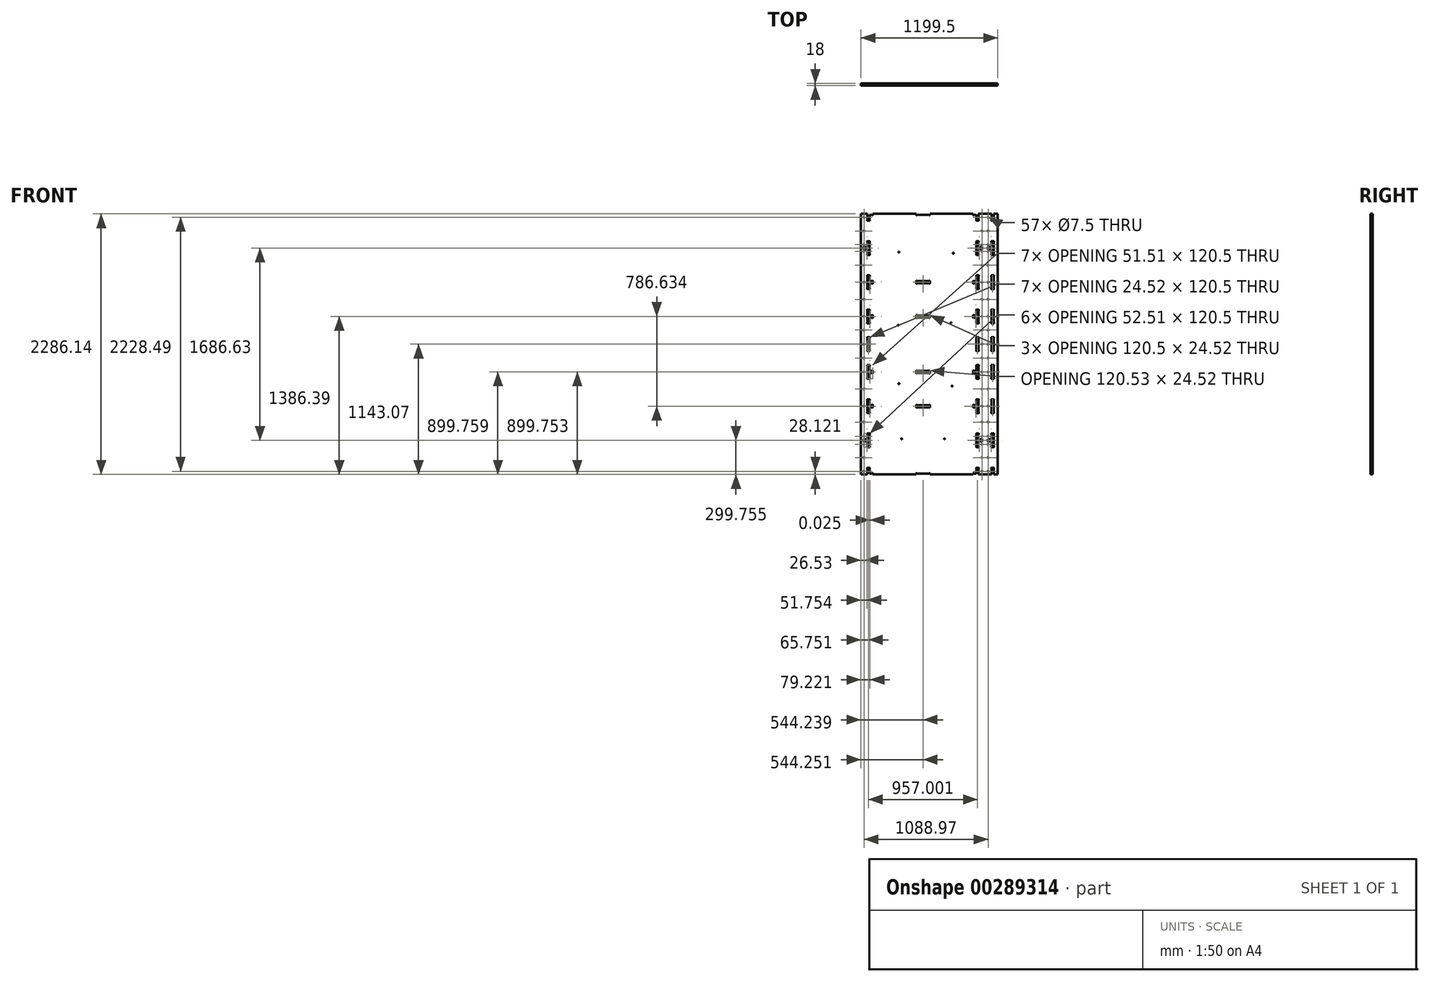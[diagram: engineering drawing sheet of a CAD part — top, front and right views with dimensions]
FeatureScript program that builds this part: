
annotation { "Feature Type Name" : "Feature", "Feature Type Description" : "" }
export const myFeature = defineFeature(function(context is Context, id is Id, definition is map)
    precondition{}
    {
        {
            var Q0;
            Q0=qCreatedBy(makeId("Front.planeOp"),FACE);
            var sketch = newSketch(context, id + "F0", { "sketchPlane" : qUnion([Q0])});
            skLineSegment(sketch, "E0", {"start": v(-600, -1200) * mm, "end": v(600, -1200) * mm});
            skLineSegment(sketch, "E1", {"start": v(600, -1200) * mm, "end": v(600, 1200) * mm});
            skLineSegment(sketch, "E2", {"start": v(600, 1200) * mm, "end": v(-600, 1200) * mm});
            skLineSegment(sketch, "E3", {"start": v(-600, 1200) * mm, "end": v(-600, -1200) * mm});
            skLineSegment(sketch, "E4", {"start": v(-600, -1086.14) * mm, "end": v(-543.5, -1086.14) * mm});
            skLineSegment(sketch, "E5", {"start": v(-543.5, -1086.14) * mm, "end": v(-543.5, -1032.4) * mm});
            skLineSegment(sketch, "E6", {"start": v(-543.5, -1032.4) * mm, "end": v(-543.5, -1032.17) * mm});
            skLineSegment(sketch, "E7", {"start": v(-543.5, -1032.17) * mm, "end": v(-543.73, -1032.16) * mm});
            skArc(sketch, "E8", {"start": v(-543.73, -1032.16) * mm, "mid": v(-546.5, -1029.04) * mm, "end": v(-543.5, -1026.14) * mm});
            skLineSegment(sketch, "E9", {"start": v(-543.5, -1026.14) * mm, "end": v(-525, -1026.14) * mm});
            skArc(sketch, "E10", {"start": v(-525, -1026.14) * mm, "mid": v(-521.98, -1029.03) * mm, "end": v(-524.77, -1032.16) * mm});
            skLineSegment(sketch, "E11", {"start": v(-524.77, -1032.16) * mm, "end": v(-525, -1032.17) * mm});
            skLineSegment(sketch, "E12", {"start": v(-525, -1032.17) * mm, "end": v(-525, -1032.4) * mm});
            skLineSegment(sketch, "E13", {"start": v(-525, -1032.4) * mm, "end": v(-525, -1077.14) * mm});
            skLineSegment(sketch, "E14", {"start": v(-525, -1077.14) * mm, "end": v(-501.27, -1077.14) * mm});
            skLineSegment(sketch, "E15", {"start": v(-501.27, -1077.14) * mm, "end": v(-501.04, -1077.14) * mm});
            skLineSegment(sketch, "E16", {"start": v(-501.04, -1077.14) * mm, "end": v(-501.02, -1076.9) * mm});
            skArc(sketch, "E17", {"start": v(-501.02, -1076.9) * mm, "mid": v(-497.9, -1074.13) * mm, "end": v(-495, -1077.14) * mm});
            skLineSegment(sketch, "E18", {"start": v(-495, -1077.14) * mm, "end": v(-495, -1086.14) * mm});
            skLineSegment(sketch, "E19", {"start": v(-495, -1086.14) * mm, "end": v(-116, -1086.14) * mm});
            skLineSegment(sketch, "E20", {"start": v(-116, -1086.14) * mm, "end": v(-116, -1077.14) * mm});
            skArc(sketch, "E21", {"start": v(-116, -1077.14) * mm, "mid": v(-113.1, -1074.12) * mm, "end": v(-109.98, -1076.9) * mm});
            skLineSegment(sketch, "E22", {"start": v(-109.98, -1076.9) * mm, "end": v(-109.96, -1077.14) * mm});
            skLineSegment(sketch, "E23", {"start": v(-109.96, -1077.14) * mm, "end": v(-109.73, -1077.14) * mm});
            skLineSegment(sketch, "E24", {"start": v(-109.73, -1077.14) * mm, "end": v(-1.77, -1077.14) * mm});
            skLineSegment(sketch, "E25", {"start": v(-1.77, -1077.14) * mm, "end": v(-1.54, -1077.14) * mm});
            skLineSegment(sketch, "E26", {"start": v(-1.54, -1077.14) * mm, "end": v(-1.52, -1076.9) * mm});
            skArc(sketch, "E27", {"start": v(-1.52, -1076.9) * mm, "mid": v(1.6, -1074.13) * mm, "end": v(4.5, -1077.14) * mm});
            skLineSegment(sketch, "E28", {"start": v(4.5, -1077.14) * mm, "end": v(4.5, -1086.14) * mm});
            skLineSegment(sketch, "E29", {"start": v(4.5, -1086.14) * mm, "end": v(383.5, -1086.14) * mm});
            skLineSegment(sketch, "E30", {"start": v(383.5, -1086.14) * mm, "end": v(383.5, -1077.14) * mm});
            skArc(sketch, "E31", {"start": v(383.5, -1077.14) * mm, "mid": v(386.4, -1074.12) * mm, "end": v(389.52, -1076.9) * mm});
            skLineSegment(sketch, "E32", {"start": v(389.52, -1076.9) * mm, "end": v(389.54, -1077.14) * mm});
            skLineSegment(sketch, "E33", {"start": v(389.54, -1077.14) * mm, "end": v(389.77, -1077.14) * mm});
            skLineSegment(sketch, "E34", {"start": v(389.77, -1077.14) * mm, "end": v(413.5, -1077.14) * mm});
            skLineSegment(sketch, "E35", {"start": v(413.5, -1077.14) * mm, "end": v(413.5, -1032.4) * mm});
            skLineSegment(sketch, "E36", {"start": v(413.5, -1032.4) * mm, "end": v(413.5, -1032.18) * mm});
            skLineSegment(sketch, "E37", {"start": v(413.5, -1032.18) * mm, "end": v(413.27, -1032.16) * mm});
            skArc(sketch, "E38", {"start": v(413.27, -1032.16) * mm, "mid": v(410.5, -1029.04) * mm, "end": v(413.5, -1026.14) * mm});
            skLineSegment(sketch, "E39", {"start": v(413.5, -1026.14) * mm, "end": v(432, -1026.14) * mm});
            skArc(sketch, "E40", {"start": v(432, -1026.14) * mm, "mid": v(435.02, -1029.04) * mm, "end": v(432.23, -1032.16) * mm});
            skLineSegment(sketch, "E41", {"start": v(432.23, -1032.16) * mm, "end": v(432, -1032.18) * mm});
            skLineSegment(sketch, "E42", {"start": v(432, -1032.18) * mm, "end": v(432, -1032.4) * mm});
            skLineSegment(sketch, "E43", {"start": v(432, -1032.4) * mm, "end": v(432, -1086.14) * mm});
            skLineSegment(sketch, "E44", {"start": v(432, -1086.14) * mm, "end": v(545.5, -1086.14) * mm});
            skLineSegment(sketch, "E45", {"start": v(545.5, -1086.14) * mm, "end": v(545.5, -1032.4) * mm});
            skLineSegment(sketch, "E46", {"start": v(545.5, -1032.4) * mm, "end": v(545.5, -1032.18) * mm});
            skLineSegment(sketch, "E47", {"start": v(545.5, -1032.18) * mm, "end": v(545.27, -1032.16) * mm});
            skArc(sketch, "E48", {"start": v(545.27, -1032.16) * mm, "mid": v(542.5, -1029.04) * mm, "end": v(545.5, -1026.14) * mm});
            skLineSegment(sketch, "E49", {"start": v(545.5, -1026.14) * mm, "end": v(564, -1026.14) * mm});
            skArc(sketch, "E50", {"start": v(564, -1026.14) * mm, "mid": v(567.02, -1029.04) * mm, "end": v(564.23, -1032.16) * mm});
            skLineSegment(sketch, "E51", {"start": v(564.23, -1032.16) * mm, "end": v(564, -1032.18) * mm});
            skLineSegment(sketch, "E52", {"start": v(564, -1032.18) * mm, "end": v(564, -1032.4) * mm});
            skLineSegment(sketch, "E53", {"start": v(564, -1032.4) * mm, "end": v(564, -1086.14) * mm});
            skLineSegment(sketch, "E54", {"start": v(564, -1086.14) * mm, "end": v(599.5, -1086.14) * mm});
            skLineSegment(sketch, "E55", {"start": v(599.5, -1086.14) * mm, "end": v(599.48, -336.39) * mm});
            skLineSegment(sketch, "E56", {"start": v(599.48, -336.39) * mm, "end": v(599.5, -336.28) * mm});
            skLineSegment(sketch, "E57", {"start": v(599.5, -336.28) * mm, "end": v(599.48, -64.75) * mm});
            skLineSegment(sketch, "E58", {"start": v(599.48, -64.75) * mm, "end": v(599.5, -64.64) * mm});
            skLineSegment(sketch, "E59", {"start": v(599.5, -64.64) * mm, "end": v(599.5, 1200) * mm});
            skLineSegment(sketch, "E60", {"start": v(599.5, 1200) * mm, "end": v(564, 1200) * mm});
            skLineSegment(sketch, "E61", {"start": v(564, 1200) * mm, "end": v(564, 1146.27) * mm});
            skLineSegment(sketch, "E62", {"start": v(564, 1146.27) * mm, "end": v(564, 1146.04) * mm});
            skLineSegment(sketch, "E63", {"start": v(564, 1146.04) * mm, "end": v(564.23, 1146.02) * mm});
            skArc(sketch, "E64", {"start": v(564.23, 1146.02) * mm, "mid": v(567, 1142.9) * mm, "end": v(564, 1140) * mm});
            skLineSegment(sketch, "E65", {"start": v(564, 1140) * mm, "end": v(545.5, 1140) * mm});
            skArc(sketch, "E66", {"start": v(545.5, 1140) * mm, "mid": v(542.48, 1142.9) * mm, "end": v(545.27, 1146.02) * mm});
            skLineSegment(sketch, "E67", {"start": v(545.27, 1146.02) * mm, "end": v(545.5, 1146.04) * mm});
            skLineSegment(sketch, "E68", {"start": v(545.5, 1146.04) * mm, "end": v(545.5, 1146.27) * mm});
            skLineSegment(sketch, "E69", {"start": v(545.5, 1146.27) * mm, "end": v(545.5, 1200) * mm});
            skLineSegment(sketch, "E70", {"start": v(545.5, 1200) * mm, "end": v(432, 1200) * mm});
            skLineSegment(sketch, "E71", {"start": v(432, 1200) * mm, "end": v(432, 1146.27) * mm});
            skLineSegment(sketch, "E72", {"start": v(432, 1146.27) * mm, "end": v(432, 1146.04) * mm});
            skLineSegment(sketch, "E73", {"start": v(432, 1146.04) * mm, "end": v(432.23, 1146.02) * mm});
            skArc(sketch, "E74", {"start": v(432.23, 1146.02) * mm, "mid": v(435, 1142.9) * mm, "end": v(432, 1140) * mm});
            skLineSegment(sketch, "E75", {"start": v(432, 1140) * mm, "end": v(413.5, 1140) * mm});
            skArc(sketch, "E76", {"start": v(413.5, 1140) * mm, "mid": v(410.48, 1142.9) * mm, "end": v(413.27, 1146.02) * mm});
            skLineSegment(sketch, "E77", {"start": v(413.27, 1146.02) * mm, "end": v(413.5, 1146.04) * mm});
            skLineSegment(sketch, "E78", {"start": v(413.5, 1146.04) * mm, "end": v(413.5, 1146.27) * mm});
            skLineSegment(sketch, "E79", {"start": v(413.5, 1146.27) * mm, "end": v(413.5, 1191) * mm});
            skLineSegment(sketch, "E80", {"start": v(413.5, 1191) * mm, "end": v(389.77, 1191) * mm});
            skLineSegment(sketch, "E81", {"start": v(389.77, 1191) * mm, "end": v(389.54, 1191) * mm});
            skLineSegment(sketch, "E82", {"start": v(389.54, 1191) * mm, "end": v(389.52, 1190.77) * mm});
            skArc(sketch, "E83", {"start": v(389.52, 1190.77) * mm, "mid": v(386.4, 1188) * mm, "end": v(383.5, 1191) * mm});
            skLineSegment(sketch, "E84", {"start": v(383.5, 1191) * mm, "end": v(383.5, 1200) * mm});
            skLineSegment(sketch, "E85", {"start": v(383.5, 1200) * mm, "end": v(4.5, 1200) * mm});
            skLineSegment(sketch, "E86", {"start": v(4.5, 1200) * mm, "end": v(4.5, 1191) * mm});
            skArc(sketch, "E87", {"start": v(4.5, 1191) * mm, "mid": v(1.6, 1187.98) * mm, "end": v(-1.52, 1190.77) * mm});
            skLineSegment(sketch, "E88", {"start": v(-1.52, 1190.77) * mm, "end": v(-1.54, 1191) * mm});
            skLineSegment(sketch, "E89", {"start": v(-1.54, 1191) * mm, "end": v(-1.77, 1191) * mm});
            skLineSegment(sketch, "E90", {"start": v(-1.77, 1191) * mm, "end": v(-109.73, 1191) * mm});
            skLineSegment(sketch, "E91", {"start": v(-109.73, 1191) * mm, "end": v(-109.96, 1191) * mm});
            skLineSegment(sketch, "E92", {"start": v(-109.96, 1191) * mm, "end": v(-109.98, 1190.77) * mm});
            skArc(sketch, "E93", {"start": v(-109.98, 1190.77) * mm, "mid": v(-113.1, 1188) * mm, "end": v(-116, 1191) * mm});
            skLineSegment(sketch, "E94", {"start": v(-116, 1191) * mm, "end": v(-116, 1200) * mm});
            skLineSegment(sketch, "E95", {"start": v(-116, 1200) * mm, "end": v(-495, 1200) * mm});
            skLineSegment(sketch, "E96", {"start": v(-495, 1200) * mm, "end": v(-495, 1191) * mm});
            skArc(sketch, "E97", {"start": v(-495, 1191) * mm, "mid": v(-497.9, 1187.98) * mm, "end": v(-501.02, 1190.77) * mm});
            skLineSegment(sketch, "E98", {"start": v(-501.02, 1190.77) * mm, "end": v(-501.04, 1191) * mm});
            skLineSegment(sketch, "E99", {"start": v(-501.04, 1191) * mm, "end": v(-501.27, 1191) * mm});
            skLineSegment(sketch, "E100", {"start": v(-501.27, 1191) * mm, "end": v(-525, 1191) * mm});
            skLineSegment(sketch, "E101", {"start": v(-525, 1191) * mm, "end": v(-525, 1146.27) * mm});
            skLineSegment(sketch, "E102", {"start": v(-525, 1146.27) * mm, "end": v(-525, 1146.04) * mm});
            skLineSegment(sketch, "E103", {"start": v(-525, 1146.04) * mm, "end": v(-524.77, 1146.02) * mm});
            skArc(sketch, "E104", {"start": v(-524.77, 1146.02) * mm, "mid": v(-522, 1142.9) * mm, "end": v(-525, 1140) * mm});
            skLineSegment(sketch, "E105", {"start": v(-525, 1140) * mm, "end": v(-543.5, 1140) * mm});
            skArc(sketch, "E106", {"start": v(-543.5, 1140) * mm, "mid": v(-546.52, 1142.9) * mm, "end": v(-543.73, 1146.02) * mm});
            skLineSegment(sketch, "E107", {"start": v(-543.73, 1146.02) * mm, "end": v(-543.5, 1146.04) * mm});
            skLineSegment(sketch, "E108", {"start": v(-543.5, 1146.04) * mm, "end": v(-543.5, 1146.27) * mm});
            skLineSegment(sketch, "E109", {"start": v(-543.5, 1146.27) * mm, "end": v(-543.5, 1200) * mm});
            skLineSegment(sketch, "E110", {"start": v(545.5, 2.7) * mm, "end": v(545.5, 111.16) * mm});
            skArc(sketch, "E111", {"start": v(545.5, 111.16) * mm, "mid": v(542.5, 114.17) * mm, "end": v(545.5, 117.18) * mm});
            skLineSegment(sketch, "E112", {"start": v(545.5, 117.18) * mm, "end": v(564, 117.18) * mm});
            skArc(sketch, "E113", {"start": v(564, 117.18) * mm, "mid": v(567.01, 114.17) * mm, "end": v(564, 111.16) * mm});
            skLineSegment(sketch, "E114", {"start": v(564, 111.16) * mm, "end": v(564, 2.7) * mm});
            skArc(sketch, "E115", {"start": v(564, 2.7) * mm, "mid": v(567.01, -0.3) * mm, "end": v(564, -3.32) * mm});
            skLineSegment(sketch, "E116", {"start": v(564, -3.32) * mm, "end": v(545.5, -3.32) * mm});
            skArc(sketch, "E117", {"start": v(545.5, -3.32) * mm, "mid": v(542.5, -0.3) * mm, "end": v(545.5, 2.7) * mm});
            skLineSegment(sketch, "E118", {"start": v(563.98, -132.16) * mm, "end": v(564, -240.62) * mm});
            skArc(sketch, "E119", {"start": v(564, -240.62) * mm, "mid": v(567.01, -243.63) * mm, "end": v(564, -246.64) * mm});
            skLineSegment(sketch, "E120", {"start": v(564, -246.64) * mm, "end": v(545.5, -246.63) * mm});
            skArc(sketch, "E121", {"start": v(545.5, -246.63) * mm, "mid": v(542.5, -243.62) * mm, "end": v(545.5, -240.61) * mm});
            skLineSegment(sketch, "E122", {"start": v(545.5, -240.61) * mm, "end": v(545.5, -132.16) * mm});
            skArc(sketch, "E123", {"start": v(545.5, -132.16) * mm, "mid": v(542.5, -129.15) * mm, "end": v(545.5, -126.14) * mm});
            skLineSegment(sketch, "E124", {"start": v(545.5, -126.14) * mm, "end": v(563.98, -126.14) * mm});
            skArc(sketch, "E125", {"start": v(563.98, -126.14) * mm, "mid": v(566.99, -129.15) * mm, "end": v(563.98, -132.16) * mm});
            skLineSegment(sketch, "E126", {"start": v(564, -432.15) * mm, "end": v(564, -540.61) * mm});
            skArc(sketch, "E127", {"start": v(564, -540.61) * mm, "mid": v(567.01, -543.62) * mm, "end": v(564, -546.63) * mm});
            skLineSegment(sketch, "E128", {"start": v(564, -546.63) * mm, "end": v(545.5, -546.63) * mm});
            skArc(sketch, "E129", {"start": v(545.5, -546.63) * mm, "mid": v(542.5, -543.62) * mm, "end": v(545.5, -540.61) * mm});
            skLineSegment(sketch, "E130", {"start": v(545.5, -540.61) * mm, "end": v(545.5, -432.15) * mm});
            skArc(sketch, "E131", {"start": v(545.5, -432.15) * mm, "mid": v(542.5, -429.14) * mm, "end": v(545.5, -426.13) * mm});
            skLineSegment(sketch, "E132", {"start": v(545.5, -426.13) * mm, "end": v(564, -426.13) * mm});
            skArc(sketch, "E133", {"start": v(564, -426.13) * mm, "mid": v(567.01, -429.14) * mm, "end": v(564, -432.15) * mm});
            skLineSegment(sketch, "E134", {"start": v(514.5, -795.63) * mm, "end": v(514.5, -777.13) * mm});
            skArc(sketch, "E135", {"start": v(514.5, -777.13) * mm, "mid": v(517.5, -774.12) * mm, "end": v(520.52, -777.13) * mm});
            skLineSegment(sketch, "E136", {"start": v(520.52, -777.13) * mm, "end": v(545.5, -777.13) * mm});
            skLineSegment(sketch, "E137", {"start": v(545.5, -777.13) * mm, "end": v(545.5, -732.15) * mm});
            skArc(sketch, "E138", {"start": v(545.5, -732.15) * mm, "mid": v(542.49, -729.14) * mm, "end": v(545.5, -726.13) * mm});
            skLineSegment(sketch, "E139", {"start": v(545.5, -726.13) * mm, "end": v(564, -726.13) * mm});
            skArc(sketch, "E140", {"start": v(564, -726.13) * mm, "mid": v(567, -729.14) * mm, "end": v(564, -732.15) * mm});
            skLineSegment(sketch, "E141", {"start": v(564, -732.15) * mm, "end": v(564, -840.61) * mm});
            skArc(sketch, "E142", {"start": v(564, -840.61) * mm, "mid": v(567, -843.62) * mm, "end": v(564, -846.63) * mm});
            skLineSegment(sketch, "E143", {"start": v(564, -846.63) * mm, "end": v(545.5, -846.63) * mm});
            skArc(sketch, "E144", {"start": v(545.5, -846.63) * mm, "mid": v(542.49, -843.62) * mm, "end": v(545.5, -840.61) * mm});
            skLineSegment(sketch, "E145", {"start": v(545.5, -840.61) * mm, "end": v(545.5, -795.63) * mm});
            skLineSegment(sketch, "E146", {"start": v(545.5, -795.63) * mm, "end": v(520.52, -795.63) * mm});
            skArc(sketch, "E147", {"start": v(520.52, -795.63) * mm, "mid": v(517.5, -798.64) * mm, "end": v(514.5, -795.63) * mm});
            skLineSegment(sketch, "E148", {"start": v(432, -795.63) * mm, "end": v(432, -840.61) * mm});
            skArc(sketch, "E149", {"start": v(432, -840.61) * mm, "mid": v(435.01, -843.62) * mm, "end": v(432, -846.63) * mm});
            skLineSegment(sketch, "E150", {"start": v(432, -846.63) * mm, "end": v(413.5, -846.63) * mm});
            skArc(sketch, "E151", {"start": v(413.5, -846.63) * mm, "mid": v(410.5, -843.62) * mm, "end": v(413.5, -840.61) * mm});
            skLineSegment(sketch, "E152", {"start": v(413.5, -840.61) * mm, "end": v(413.5, -732.15) * mm});
            skArc(sketch, "E153", {"start": v(413.5, -732.15) * mm, "mid": v(410.5, -729.14) * mm, "end": v(413.5, -726.13) * mm});
            skLineSegment(sketch, "E154", {"start": v(413.5, -726.13) * mm, "end": v(432, -726.13) * mm});
            skArc(sketch, "E155", {"start": v(432, -726.13) * mm, "mid": v(435.01, -729.14) * mm, "end": v(432, -732.15) * mm});
            skLineSegment(sketch, "E156", {"start": v(432, -732.15) * mm, "end": v(432, -777.13) * mm});
            skLineSegment(sketch, "E157", {"start": v(432, -777.13) * mm, "end": v(456.98, -777.13) * mm});
            skArc(sketch, "E158", {"start": v(456.98, -777.13) * mm, "mid": v(459.99, -774.12) * mm, "end": v(463, -777.13) * mm});
            skLineSegment(sketch, "E159", {"start": v(463, -777.13) * mm, "end": v(463, -795.63) * mm});
            skArc(sketch, "E160", {"start": v(463, -795.63) * mm, "mid": v(459.99, -798.64) * mm, "end": v(456.98, -795.63) * mm});
            skLineSegment(sketch, "E161", {"start": v(456.98, -795.63) * mm, "end": v(432, -795.63) * mm});
            skLineSegment(sketch, "E162", {"start": v(432, 840) * mm, "end": v(413.5, 840) * mm});
            skArc(sketch, "E163", {"start": v(413.5, 840) * mm, "mid": v(410.5, 843) * mm, "end": v(413.5, 846.02) * mm});
            skLineSegment(sketch, "E164", {"start": v(413.5, 846.02) * mm, "end": v(413.5, 954.48) * mm});
            skArc(sketch, "E165", {"start": v(413.5, 954.48) * mm, "mid": v(410.5, 957.49) * mm, "end": v(413.5, 960.5) * mm});
            skLineSegment(sketch, "E166", {"start": v(413.5, 960.5) * mm, "end": v(432, 960.5) * mm});
            skArc(sketch, "E167", {"start": v(432, 960.5) * mm, "mid": v(435.01, 957.49) * mm, "end": v(432, 954.48) * mm});
            skLineSegment(sketch, "E168", {"start": v(432, 954.48) * mm, "end": v(432, 909.5) * mm});
            skLineSegment(sketch, "E169", {"start": v(432, 909.5) * mm, "end": v(456.98, 909.5) * mm});
            skArc(sketch, "E170", {"start": v(456.98, 909.5) * mm, "mid": v(459.99, 912.5) * mm, "end": v(463, 909.5) * mm});
            skLineSegment(sketch, "E171", {"start": v(463, 909.5) * mm, "end": v(463, 891) * mm});
            skArc(sketch, "E172", {"start": v(463, 891) * mm, "mid": v(459.99, 887.99) * mm, "end": v(456.98, 891) * mm});
            skLineSegment(sketch, "E173", {"start": v(456.98, 891) * mm, "end": v(432, 891) * mm});
            skLineSegment(sketch, "E174", {"start": v(432, 891) * mm, "end": v(432, 846.02) * mm});
            skArc(sketch, "E175", {"start": v(432, 846.02) * mm, "mid": v(435.01, 843) * mm, "end": v(432, 840) * mm});
            skLineSegment(sketch, "E176", {"start": v(564, 654.48) * mm, "end": v(564, 546.02) * mm});
            skArc(sketch, "E177", {"start": v(564, 546.02) * mm, "mid": v(567.01, 543) * mm, "end": v(564, 540) * mm});
            skLineSegment(sketch, "E178", {"start": v(564, 540) * mm, "end": v(545.5, 540) * mm});
            skArc(sketch, "E179", {"start": v(545.5, 540) * mm, "mid": v(542.5, 543) * mm, "end": v(545.5, 546.02) * mm});
            skLineSegment(sketch, "E180", {"start": v(545.5, 546.02) * mm, "end": v(545.5, 654.48) * mm});
            skArc(sketch, "E181", {"start": v(545.5, 654.48) * mm, "mid": v(542.5, 657.49) * mm, "end": v(545.5, 660.5) * mm});
            skLineSegment(sketch, "E182", {"start": v(545.5, 660.5) * mm, "end": v(564, 660.5) * mm});
            skArc(sketch, "E183", {"start": v(564, 660.5) * mm, "mid": v(567.01, 657.49) * mm, "end": v(564, 654.48) * mm});
            skLineSegment(sketch, "E184", {"start": v(564, 354.48) * mm, "end": v(564, 246.02) * mm});
            skArc(sketch, "E185", {"start": v(564, 246.02) * mm, "mid": v(567.01, 243) * mm, "end": v(564, 240) * mm});
            skLineSegment(sketch, "E186", {"start": v(564, 240) * mm, "end": v(545.5, 240) * mm});
            skArc(sketch, "E187", {"start": v(545.5, 240) * mm, "mid": v(542.5, 243) * mm, "end": v(545.5, 246.02) * mm});
            skLineSegment(sketch, "E188", {"start": v(545.5, 246.02) * mm, "end": v(545.5, 354.48) * mm});
            skArc(sketch, "E189", {"start": v(545.5, 354.48) * mm, "mid": v(542.5, 357.49) * mm, "end": v(545.5, 360.5) * mm});
            skLineSegment(sketch, "E190", {"start": v(545.5, 360.5) * mm, "end": v(564, 360.5) * mm});
            skArc(sketch, "E191", {"start": v(564, 360.5) * mm, "mid": v(567.01, 357.49) * mm, "end": v(564, 354.48) * mm});
            skLineSegment(sketch, "E192", {"start": v(413.5, 309.5) * mm, "end": v(413.5, 354.48) * mm});
            skArc(sketch, "E193", {"start": v(413.5, 354.48) * mm, "mid": v(410.5, 357.49) * mm, "end": v(413.5, 360.5) * mm});
            skLineSegment(sketch, "E194", {"start": v(413.5, 360.5) * mm, "end": v(432, 360.5) * mm});
            skArc(sketch, "E195", {"start": v(432, 360.5) * mm, "mid": v(435.01, 357.49) * mm, "end": v(432, 354.48) * mm});
            skLineSegment(sketch, "E196", {"start": v(432, 354.48) * mm, "end": v(432, 246.02) * mm});
            skArc(sketch, "E197", {"start": v(432, 246.02) * mm, "mid": v(435.01, 243) * mm, "end": v(432, 240) * mm});
            skLineSegment(sketch, "E198", {"start": v(432, 240) * mm, "end": v(413.5, 240) * mm});
            skArc(sketch, "E199", {"start": v(413.5, 240) * mm, "mid": v(410.5, 243) * mm, "end": v(413.5, 246.02) * mm});
            skLineSegment(sketch, "E200", {"start": v(413.5, 246.02) * mm, "end": v(413.5, 291) * mm});
            skLineSegment(sketch, "E201", {"start": v(413.5, 291) * mm, "end": v(389.52, 291) * mm});
            skArc(sketch, "E202", {"start": v(389.52, 291) * mm, "mid": v(386.51, 287.99) * mm, "end": v(383.5, 291) * mm});
            skLineSegment(sketch, "E203", {"start": v(383.5, 291) * mm, "end": v(383.5, 309.5) * mm});
            skArc(sketch, "E204", {"start": v(383.5, 309.5) * mm, "mid": v(386.51, 312.5) * mm, "end": v(389.52, 309.5) * mm});
            skLineSegment(sketch, "E205", {"start": v(389.52, 309.5) * mm, "end": v(413.5, 309.5) * mm});
            skLineSegment(sketch, "E206", {"start": v(432, 111.16) * mm, "end": v(432, 2.7) * mm});
            skArc(sketch, "E207", {"start": v(432, 2.7) * mm, "mid": v(435.01, -0.31) * mm, "end": v(432, -3.32) * mm});
            skLineSegment(sketch, "E208", {"start": v(432, -3.32) * mm, "end": v(413.5, -3.32) * mm});
            skArc(sketch, "E209", {"start": v(413.5, -3.32) * mm, "mid": v(410.5, -0.31) * mm, "end": v(413.5, 2.7) * mm});
            skLineSegment(sketch, "E210", {"start": v(413.5, 2.7) * mm, "end": v(413.5, 111.16) * mm});
            skArc(sketch, "E211", {"start": v(413.5, 111.16) * mm, "mid": v(410.5, 114.17) * mm, "end": v(413.5, 117.18) * mm});
            skLineSegment(sketch, "E212", {"start": v(413.5, 117.18) * mm, "end": v(432, 117.18) * mm});
            skArc(sketch, "E213", {"start": v(432, 117.18) * mm, "mid": v(435.01, 114.17) * mm, "end": v(432, 111.16) * mm});
            skLineSegment(sketch, "E214", {"start": v(413.48, -195.64) * mm, "end": v(389.52, -195.64) * mm});
            skArc(sketch, "E215", {"start": v(389.52, -195.64) * mm, "mid": v(386.51, -198.65) * mm, "end": v(383.5, -195.63) * mm});
            skLineSegment(sketch, "E216", {"start": v(383.5, -195.63) * mm, "end": v(383.5, -177.14) * mm});
            skArc(sketch, "E217", {"start": v(383.5, -177.14) * mm, "mid": v(386.51, -174.13) * mm, "end": v(389.52, -177.14) * mm});
            skLineSegment(sketch, "E218", {"start": v(389.52, -177.14) * mm, "end": v(413.5, -177.14) * mm});
            skLineSegment(sketch, "E219", {"start": v(413.5, -177.14) * mm, "end": v(413.48, -132.15) * mm});
            skArc(sketch, "E220", {"start": v(413.48, -132.15) * mm, "mid": v(410.47, -129.15) * mm, "end": v(413.48, -126.13) * mm});
            skLineSegment(sketch, "E221", {"start": v(413.48, -126.13) * mm, "end": v(431.98, -126.14) * mm});
            skArc(sketch, "E222", {"start": v(431.98, -126.14) * mm, "mid": v(434.99, -129.15) * mm, "end": v(431.98, -132.16) * mm});
            skLineSegment(sketch, "E223", {"start": v(431.98, -132.16) * mm, "end": v(432, -240.62) * mm});
            skArc(sketch, "E224", {"start": v(432, -240.62) * mm, "mid": v(435.01, -243.63) * mm, "end": v(432, -246.64) * mm});
            skLineSegment(sketch, "E225", {"start": v(432, -246.64) * mm, "end": v(413.5, -246.63) * mm});
            skArc(sketch, "E226", {"start": v(413.5, -246.63) * mm, "mid": v(410.49, -243.63) * mm, "end": v(413.5, -240.61) * mm});
            skLineSegment(sketch, "E227", {"start": v(413.5, -240.61) * mm, "end": v(413.48, -195.64) * mm});
            skLineSegment(sketch, "E228", {"start": v(383.5, -495.64) * mm, "end": v(383.5, -477.14) * mm});
            skArc(sketch, "E229", {"start": v(383.5, -477.14) * mm, "mid": v(386.51, -474.13) * mm, "end": v(389.52, -477.14) * mm});
            skLineSegment(sketch, "E230", {"start": v(389.52, -477.14) * mm, "end": v(413.5, -477.14) * mm});
            skLineSegment(sketch, "E231", {"start": v(413.5, -477.14) * mm, "end": v(413.5, -432.15) * mm});
            skArc(sketch, "E232", {"start": v(413.5, -432.15) * mm, "mid": v(410.5, -429.14) * mm, "end": v(413.5, -426.13) * mm});
            skLineSegment(sketch, "E233", {"start": v(413.5, -426.13) * mm, "end": v(432, -426.13) * mm});
            skArc(sketch, "E234", {"start": v(432, -426.13) * mm, "mid": v(435.01, -429.14) * mm, "end": v(432, -432.15) * mm});
            skLineSegment(sketch, "E235", {"start": v(432, -432.15) * mm, "end": v(432, -540.61) * mm});
            skArc(sketch, "E236", {"start": v(432, -540.61) * mm, "mid": v(435.01, -543.62) * mm, "end": v(432, -546.63) * mm});
            skLineSegment(sketch, "E237", {"start": v(432, -546.63) * mm, "end": v(413.5, -546.63) * mm});
            skArc(sketch, "E238", {"start": v(413.5, -546.63) * mm, "mid": v(410.5, -543.62) * mm, "end": v(413.5, -540.61) * mm});
            skLineSegment(sketch, "E239", {"start": v(413.5, -540.61) * mm, "end": v(413.5, -495.64) * mm});
            skLineSegment(sketch, "E240", {"start": v(413.5, -495.64) * mm, "end": v(389.52, -495.64) * mm});
            skArc(sketch, "E241", {"start": v(389.52, -495.64) * mm, "mid": v(386.51, -498.65) * mm, "end": v(383.5, -495.64) * mm});
            skLineSegment(sketch, "E242", {"start": v(-1.52, -495.64) * mm, "end": v(-109.98, -495.64) * mm});
            skArc(sketch, "E243", {"start": v(-109.98, -495.64) * mm, "mid": v(-112.99, -498.65) * mm, "end": v(-116, -495.64) * mm});
            skLineSegment(sketch, "E244", {"start": v(-116, -495.64) * mm, "end": v(-116, -477.14) * mm});
            skArc(sketch, "E245", {"start": v(-116, -477.14) * mm, "mid": v(-112.99, -474.13) * mm, "end": v(-109.98, -477.14) * mm});
            skLineSegment(sketch, "E246", {"start": v(-109.98, -477.14) * mm, "end": v(-1.52, -477.14) * mm});
            skArc(sketch, "E247", {"start": v(-1.52, -477.14) * mm, "mid": v(1.5, -474.13) * mm, "end": v(4.5, -477.14) * mm});
            skLineSegment(sketch, "E248", {"start": v(4.5, -477.14) * mm, "end": v(4.5, -495.64) * mm});
            skArc(sketch, "E249", {"start": v(4.5, -495.64) * mm, "mid": v(1.5, -498.65) * mm, "end": v(-1.52, -495.64) * mm});
            skLineSegment(sketch, "E250", {"start": v(-543.5, -777.13) * mm, "end": v(-543.5, -732.16) * mm});
            skArc(sketch, "E251", {"start": v(-543.5, -732.16) * mm, "mid": v(-546.5, -729.15) * mm, "end": v(-543.5, -726.14) * mm});
            skLineSegment(sketch, "E252", {"start": v(-543.5, -726.14) * mm, "end": v(-525, -726.14) * mm});
            skArc(sketch, "E253", {"start": v(-525, -726.14) * mm, "mid": v(-521.99, -729.15) * mm, "end": v(-525, -732.16) * mm});
            skLineSegment(sketch, "E254", {"start": v(-525, -732.16) * mm, "end": v(-525, -840.62) * mm});
            skArc(sketch, "E255", {"start": v(-525, -840.62) * mm, "mid": v(-521.99, -843.63) * mm, "end": v(-525, -846.64) * mm});
            skLineSegment(sketch, "E256", {"start": v(-525, -846.64) * mm, "end": v(-543.5, -846.64) * mm});
            skArc(sketch, "E257", {"start": v(-543.5, -846.64) * mm, "mid": v(-546.5, -843.63) * mm, "end": v(-543.5, -840.62) * mm});
            skLineSegment(sketch, "E258", {"start": v(-543.5, -840.62) * mm, "end": v(-543.5, -795.63) * mm});
            skLineSegment(sketch, "E259", {"start": v(-543.5, -795.63) * mm, "end": v(-568.48, -795.63) * mm});
            skArc(sketch, "E260", {"start": v(-568.48, -795.63) * mm, "mid": v(-571.5, -798.64) * mm, "end": v(-574.5, -795.63) * mm});
            skLineSegment(sketch, "E261", {"start": v(-574.5, -795.63) * mm, "end": v(-574.5, -777.13) * mm});
            skArc(sketch, "E262", {"start": v(-574.5, -777.13) * mm, "mid": v(-571.5, -774.12) * mm, "end": v(-568.48, -777.13) * mm});
            skLineSegment(sketch, "E263", {"start": v(-568.48, -777.13) * mm, "end": v(-543.5, -777.13) * mm});
            skLineSegment(sketch, "E264", {"start": v(-543.5, 891) * mm, "end": v(-568.48, 891) * mm});
            skArc(sketch, "E265", {"start": v(-568.48, 891) * mm, "mid": v(-571.5, 887.99) * mm, "end": v(-574.5, 891) * mm});
            skLineSegment(sketch, "E266", {"start": v(-574.5, 891) * mm, "end": v(-574.5, 909.5) * mm});
            skArc(sketch, "E267", {"start": v(-574.5, 909.5) * mm, "mid": v(-571.5, 912.5) * mm, "end": v(-568.48, 909.5) * mm});
            skLineSegment(sketch, "E268", {"start": v(-568.48, 909.5) * mm, "end": v(-543.5, 909.5) * mm});
            skLineSegment(sketch, "E269", {"start": v(-543.5, 909.5) * mm, "end": v(-543.5, 954.48) * mm});
            skArc(sketch, "E270", {"start": v(-543.5, 954.48) * mm, "mid": v(-546.5, 957.5) * mm, "end": v(-543.5, 960.5) * mm});
            skLineSegment(sketch, "E271", {"start": v(-543.5, 960.5) * mm, "end": v(-525, 960.5) * mm});
            skArc(sketch, "E272", {"start": v(-525, 960.5) * mm, "mid": v(-521.99, 957.49) * mm, "end": v(-525, 954.48) * mm});
            skLineSegment(sketch, "E273", {"start": v(-525, 954.48) * mm, "end": v(-525, 846.02) * mm});
            skArc(sketch, "E274", {"start": v(-525, 846.02) * mm, "mid": v(-521.99, 843) * mm, "end": v(-525, 840) * mm});
            skLineSegment(sketch, "E275", {"start": v(-525, 840) * mm, "end": v(-543.5, 840) * mm});
            skArc(sketch, "E276", {"start": v(-543.5, 840) * mm, "mid": v(-546.5, 843) * mm, "end": v(-543.5, 846.02) * mm});
            skLineSegment(sketch, "E277", {"start": v(-543.5, 846.02) * mm, "end": v(-543.5, 891) * mm});
            skLineSegment(sketch, "E278", {"start": v(-1.52, 591) * mm, "end": v(-109.98, 591) * mm});
            skArc(sketch, "E279", {"start": v(-109.98, 591) * mm, "mid": v(-112.99, 587.99) * mm, "end": v(-116, 591) * mm});
            skLineSegment(sketch, "E280", {"start": v(-116, 591) * mm, "end": v(-116, 609.5) * mm});
            skArc(sketch, "E281", {"start": v(-116, 609.5) * mm, "mid": v(-112.99, 612.5) * mm, "end": v(-109.98, 609.5) * mm});
            skLineSegment(sketch, "E282", {"start": v(-109.98, 609.5) * mm, "end": v(-1.52, 609.5) * mm});
            skArc(sketch, "E283", {"start": v(-1.52, 609.5) * mm, "mid": v(1.5, 612.5) * mm, "end": v(4.5, 609.5) * mm});
            skLineSegment(sketch, "E284", {"start": v(4.5, 609.5) * mm, "end": v(4.5, 591) * mm});
            skArc(sketch, "E285", {"start": v(4.5, 591) * mm, "mid": v(1.5, 587.99) * mm, "end": v(-1.52, 591) * mm});
            skLineSegment(sketch, "E286", {"start": v(-109.98, 309.5) * mm, "end": v(-1.52, 309.5) * mm});
            skArc(sketch, "E287", {"start": v(-1.52, 309.5) * mm, "mid": v(1.5, 312.5) * mm, "end": v(4.5, 309.5) * mm});
            skLineSegment(sketch, "E288", {"start": v(4.5, 309.5) * mm, "end": v(4.5, 291) * mm});
            skArc(sketch, "E289", {"start": v(4.5, 291) * mm, "mid": v(1.5, 287.99) * mm, "end": v(-1.52, 291) * mm});
            skLineSegment(sketch, "E290", {"start": v(-1.52, 291) * mm, "end": v(-109.98, 291) * mm});
            skArc(sketch, "E291", {"start": v(-109.98, 291) * mm, "mid": v(-112.99, 287.99) * mm, "end": v(-116, 291) * mm});
            skLineSegment(sketch, "E292", {"start": v(-116, 291) * mm, "end": v(-116, 309.5) * mm});
            skArc(sketch, "E293", {"start": v(-116, 309.5) * mm, "mid": v(-112.99, 312.5) * mm, "end": v(-109.98, 309.5) * mm});
            skLineSegment(sketch, "E294", {"start": v(-116, -195.63) * mm, "end": v(-116.02, -177.13) * mm});
            skArc(sketch, "E295", {"start": v(-116.02, -177.13) * mm, "mid": v(-113.01, -174.12) * mm, "end": v(-110, -177.13) * mm});
            skLineSegment(sketch, "E296", {"start": v(-110, -177.13) * mm, "end": v(-1.54, -177.14) * mm});
            skArc(sketch, "E297", {"start": v(-1.54, -177.14) * mm, "mid": v(1.47, -174.13) * mm, "end": v(4.48, -177.14) * mm});
            skLineSegment(sketch, "E298", {"start": v(4.48, -177.14) * mm, "end": v(4.5, -195.64) * mm});
            skArc(sketch, "E299", {"start": v(4.5, -195.64) * mm, "mid": v(1.5, -198.65) * mm, "end": v(-1.52, -195.64) * mm});
            skLineSegment(sketch, "E300", {"start": v(-1.52, -195.64) * mm, "end": v(-109.98, -195.63) * mm});
            skArc(sketch, "E301", {"start": v(-109.98, -195.63) * mm, "mid": v(-112.99, -198.64) * mm, "end": v(-116, -195.63) * mm});
            skLineSegment(sketch, "E302", {"start": v(-543.5, -540.61) * mm, "end": v(-543.5, -432.15) * mm});
            skArc(sketch, "E303", {"start": v(-543.5, -432.15) * mm, "mid": v(-546.5, -429.14) * mm, "end": v(-543.5, -426.13) * mm});
            skLineSegment(sketch, "E304", {"start": v(-543.5, -426.13) * mm, "end": v(-525, -426.13) * mm});
            skArc(sketch, "E305", {"start": v(-525, -426.13) * mm, "mid": v(-521.99, -429.14) * mm, "end": v(-525, -432.15) * mm});
            skLineSegment(sketch, "E306", {"start": v(-525, -432.15) * mm, "end": v(-525, -477.14) * mm});
            skLineSegment(sketch, "E307", {"start": v(-525, -477.14) * mm, "end": v(-501.02, -477.14) * mm});
            skArc(sketch, "E308", {"start": v(-501.02, -477.14) * mm, "mid": v(-498, -474.13) * mm, "end": v(-495, -477.14) * mm});
            skLineSegment(sketch, "E309", {"start": v(-495, -477.14) * mm, "end": v(-495, -495.63) * mm});
            skArc(sketch, "E310", {"start": v(-495, -495.63) * mm, "mid": v(-498, -498.64) * mm, "end": v(-501.02, -495.63) * mm});
            skLineSegment(sketch, "E311", {"start": v(-501.02, -495.63) * mm, "end": v(-525, -495.63) * mm});
            skLineSegment(sketch, "E312", {"start": v(-525, -495.63) * mm, "end": v(-525, -540.61) * mm});
            skArc(sketch, "E313", {"start": v(-525, -540.61) * mm, "mid": v(-521.99, -543.62) * mm, "end": v(-525, -546.63) * mm});
            skLineSegment(sketch, "E314", {"start": v(-525, -546.63) * mm, "end": v(-543.5, -546.63) * mm});
            skArc(sketch, "E315", {"start": v(-543.5, -546.63) * mm, "mid": v(-546.5, -543.62) * mm, "end": v(-543.5, -540.61) * mm});
            skLineSegment(sketch, "E316", {"start": v(-543.5, 546.02) * mm, "end": v(-543.5, 654.48) * mm});
            skArc(sketch, "E317", {"start": v(-543.5, 654.48) * mm, "mid": v(-546.5, 657.49) * mm, "end": v(-543.5, 660.5) * mm});
            skLineSegment(sketch, "E318", {"start": v(-543.5, 660.5) * mm, "end": v(-525, 660.5) * mm});
            skArc(sketch, "E319", {"start": v(-525, 660.5) * mm, "mid": v(-521.99, 657.49) * mm, "end": v(-525, 654.48) * mm});
            skLineSegment(sketch, "E320", {"start": v(-525, 654.48) * mm, "end": v(-525, 609.5) * mm});
            skLineSegment(sketch, "E321", {"start": v(-525, 609.5) * mm, "end": v(-501.02, 609.5) * mm});
            skArc(sketch, "E322", {"start": v(-501.02, 609.5) * mm, "mid": v(-498, 612.5) * mm, "end": v(-495, 609.5) * mm});
            skLineSegment(sketch, "E323", {"start": v(-495, 609.5) * mm, "end": v(-495, 591) * mm});
            skArc(sketch, "E324", {"start": v(-495, 591) * mm, "mid": v(-498, 587.99) * mm, "end": v(-501.02, 591) * mm});
            skLineSegment(sketch, "E325", {"start": v(-501.02, 591) * mm, "end": v(-525, 591) * mm});
            skLineSegment(sketch, "E326", {"start": v(-525, 591) * mm, "end": v(-525, 546.02) * mm});
            skArc(sketch, "E327", {"start": v(-525, 546.02) * mm, "mid": v(-521.99, 543) * mm, "end": v(-525, 540) * mm});
            skLineSegment(sketch, "E328", {"start": v(-525, 540) * mm, "end": v(-543.5, 540) * mm});
            skArc(sketch, "E329", {"start": v(-543.5, 540) * mm, "mid": v(-546.5, 543) * mm, "end": v(-543.5, 546.02) * mm});
            skLineSegment(sketch, "E330", {"start": v(-543.5, 246.02) * mm, "end": v(-543.5, 354.48) * mm});
            skArc(sketch, "E331", {"start": v(-543.5, 354.48) * mm, "mid": v(-546.5, 357.49) * mm, "end": v(-543.5, 360.5) * mm});
            skLineSegment(sketch, "E332", {"start": v(-543.5, 360.5) * mm, "end": v(-525.27, 360.5) * mm});
            skLineSegment(sketch, "E333", {"start": v(-525.27, 360.5) * mm, "end": v(-525, 360.5) * mm});
            skArc(sketch, "E334", {"start": v(-525, 360.5) * mm, "mid": v(-521.99, 357.49) * mm, "end": v(-525, 354.48) * mm});
            skLineSegment(sketch, "E335", {"start": v(-525, 354.48) * mm, "end": v(-525, 309.5) * mm});
            skLineSegment(sketch, "E336", {"start": v(-525, 309.5) * mm, "end": v(-501.02, 309.5) * mm});
            skArc(sketch, "E337", {"start": v(-501.02, 309.5) * mm, "mid": v(-498, 312.5) * mm, "end": v(-495, 309.5) * mm});
            skLineSegment(sketch, "E338", {"start": v(-495, 309.5) * mm, "end": v(-495, 291) * mm});
            skArc(sketch, "E339", {"start": v(-495, 291) * mm, "mid": v(-498, 287.99) * mm, "end": v(-501.02, 291) * mm});
            skLineSegment(sketch, "E340", {"start": v(-501.02, 291) * mm, "end": v(-525, 291) * mm});
            skLineSegment(sketch, "E341", {"start": v(-525, 291) * mm, "end": v(-525, 246.02) * mm});
            skArc(sketch, "E342", {"start": v(-525, 246.02) * mm, "mid": v(-521.99, 243) * mm, "end": v(-525, 240) * mm});
            skLineSegment(sketch, "E343", {"start": v(-525, 240) * mm, "end": v(-543.5, 240) * mm});
            skArc(sketch, "E344", {"start": v(-543.5, 240) * mm, "mid": v(-546.5, 243) * mm, "end": v(-543.5, 246.02) * mm});
            skLineSegment(sketch, "E345", {"start": v(-543.5, 2.7) * mm, "end": v(-543.5, 111.16) * mm});
            skArc(sketch, "E346", {"start": v(-543.5, 111.16) * mm, "mid": v(-546.5, 114.17) * mm, "end": v(-543.5, 117.18) * mm});
            skLineSegment(sketch, "E347", {"start": v(-543.5, 117.18) * mm, "end": v(-525, 117.18) * mm});
            skArc(sketch, "E348", {"start": v(-525, 117.18) * mm, "mid": v(-521.99, 114.17) * mm, "end": v(-525, 111.16) * mm});
            skLineSegment(sketch, "E349", {"start": v(-525, 111.16) * mm, "end": v(-525, 2.7) * mm});
            skArc(sketch, "E350", {"start": v(-525, 2.7) * mm, "mid": v(-521.99, -0.3) * mm, "end": v(-525, -3.32) * mm});
            skLineSegment(sketch, "E351", {"start": v(-525, -3.32) * mm, "end": v(-543.5, -3.32) * mm});
            skArc(sketch, "E352", {"start": v(-543.5, -3.32) * mm, "mid": v(-546.5, -0.3) * mm, "end": v(-543.5, 2.7) * mm});
            skLineSegment(sketch, "E353", {"start": v(413.5, 591) * mm, "end": v(389.52, 591) * mm});
            skArc(sketch, "E354", {"start": v(389.52, 591) * mm, "mid": v(386.51, 587.99) * mm, "end": v(383.5, 591) * mm});
            skLineSegment(sketch, "E355", {"start": v(383.5, 591) * mm, "end": v(383.5, 609.5) * mm});
            skArc(sketch, "E356", {"start": v(383.5, 609.5) * mm, "mid": v(386.51, 612.5) * mm, "end": v(389.52, 609.5) * mm});
            skLineSegment(sketch, "E357", {"start": v(389.52, 609.5) * mm, "end": v(413.5, 609.5) * mm});
            skLineSegment(sketch, "E358", {"start": v(413.5, 609.5) * mm, "end": v(413.5, 654.48) * mm});
            skArc(sketch, "E359", {"start": v(413.5, 654.48) * mm, "mid": v(410.5, 657.49) * mm, "end": v(413.5, 660.5) * mm});
            skLineSegment(sketch, "E360", {"start": v(413.5, 660.5) * mm, "end": v(432, 660.5) * mm});
            skArc(sketch, "E361", {"start": v(432, 660.5) * mm, "mid": v(435.01, 657.49) * mm, "end": v(432, 654.48) * mm});
            skLineSegment(sketch, "E362", {"start": v(432, 654.48) * mm, "end": v(432, 546.02) * mm});
            skArc(sketch, "E363", {"start": v(432, 546.02) * mm, "mid": v(435.01, 543) * mm, "end": v(432, 540) * mm});
            skLineSegment(sketch, "E364", {"start": v(432, 540) * mm, "end": v(413.5, 540) * mm});
            skArc(sketch, "E365", {"start": v(413.5, 540) * mm, "mid": v(410.5, 543) * mm, "end": v(413.5, 546.02) * mm});
            skLineSegment(sketch, "E366", {"start": v(413.5, 546.02) * mm, "end": v(413.5, 591) * mm});
            skLineSegment(sketch, "E367", {"start": v(-543.5, -240.61) * mm, "end": v(-543.52, -132.15) * mm});
            skArc(sketch, "E368", {"start": v(-543.52, -132.15) * mm, "mid": v(-546.53, -129.14) * mm, "end": v(-543.52, -126.13) * mm});
            skLineSegment(sketch, "E369", {"start": v(-543.52, -126.13) * mm, "end": v(-525.02, -126.14) * mm});
            skArc(sketch, "E370", {"start": v(-525.02, -126.14) * mm, "mid": v(-522.01, -129.15) * mm, "end": v(-525.02, -132.16) * mm});
            skLineSegment(sketch, "E371", {"start": v(-525.02, -132.16) * mm, "end": v(-525, -177.13) * mm});
            skLineSegment(sketch, "E372", {"start": v(-525, -177.13) * mm, "end": v(-501.04, -177.14) * mm});
            skArc(sketch, "E373", {"start": v(-501.04, -177.14) * mm, "mid": v(-498.03, -174.13) * mm, "end": v(-495.02, -177.14) * mm});
            skLineSegment(sketch, "E374", {"start": v(-495.02, -177.14) * mm, "end": v(-495.02, -195.63) * mm});
            skArc(sketch, "E375", {"start": v(-495.02, -195.63) * mm, "mid": v(-498.03, -198.64) * mm, "end": v(-501.04, -195.63) * mm});
            skLineSegment(sketch, "E376", {"start": v(-501.04, -195.63) * mm, "end": v(-525, -195.63) * mm});
            skLineSegment(sketch, "E377", {"start": v(-525, -195.63) * mm, "end": v(-525, -240.61) * mm});
            skArc(sketch, "E378", {"start": v(-525, -240.61) * mm, "mid": v(-521.99, -243.62) * mm, "end": v(-525, -246.63) * mm});
            skLineSegment(sketch, "E379", {"start": v(-525, -246.63) * mm, "end": v(-525.27, -246.63) * mm});
            skLineSegment(sketch, "E380", {"start": v(-525.27, -246.63) * mm, "end": v(-543.5, -246.63) * mm});
            skArc(sketch, "E381", {"start": v(-543.5, -246.63) * mm, "mid": v(-546.51, -243.62) * mm, "end": v(-543.5, -240.61) * mm});
            skLineSegment(sketch, "E382", {"start": v(514.5, 891) * mm, "end": v(514.5, 909.5) * mm});
            skArc(sketch, "E383", {"start": v(514.5, 909.5) * mm, "mid": v(517.5, 912.5) * mm, "end": v(520.52, 909.5) * mm});
            skLineSegment(sketch, "E384", {"start": v(520.52, 909.5) * mm, "end": v(545.5, 909.5) * mm});
            skLineSegment(sketch, "E385", {"start": v(545.5, 909.5) * mm, "end": v(545.5, 954.48) * mm});
            skArc(sketch, "E386", {"start": v(545.5, 954.48) * mm, "mid": v(542.5, 957.49) * mm, "end": v(545.5, 960.5) * mm});
            skLineSegment(sketch, "E387", {"start": v(545.5, 960.5) * mm, "end": v(564, 960.5) * mm});
            skArc(sketch, "E388", {"start": v(564, 960.5) * mm, "mid": v(567.01, 957.49) * mm, "end": v(564, 954.48) * mm});
            skLineSegment(sketch, "E389", {"start": v(564, 954.48) * mm, "end": v(564, 846.02) * mm});
            skArc(sketch, "E390", {"start": v(564, 846.02) * mm, "mid": v(567.01, 843) * mm, "end": v(564, 840) * mm});
            skLineSegment(sketch, "E391", {"start": v(564, 840) * mm, "end": v(545.5, 840) * mm});
            skArc(sketch, "E392", {"start": v(545.5, 840) * mm, "mid": v(542.5, 843) * mm, "end": v(545.5, 846.02) * mm});
            skLineSegment(sketch, "E393", {"start": v(545.5, 846.02) * mm, "end": v(545.5, 891) * mm});
            skLineSegment(sketch, "E394", {"start": v(545.5, 891) * mm, "end": v(520.52, 891) * mm});
            skArc(sketch, "E395", {"start": v(520.52, 891) * mm, "mid": v(517.5, 887.99) * mm, "end": v(514.5, 891) * mm});
            skLineSegment(sketch, "E396", {"start": v(76.75, 77.3) * mm, "end": v(76.75, 37.31) * mm});
            skLineSegment(sketch, "E397", {"start": v(76.75, 37.31) * mm, "end": v(51.88, 37.31) * mm});
            skLineSegment(sketch, "E398", {"start": v(76.75, 56.42) * mm, "end": v(53.68, 56.42) * mm});
            skLineSegment(sketch, "E399", {"start": v(19.59, 77.28) * mm, "end": v(43.08, 77.28) * mm});
            skLineSegment(sketch, "E400", {"start": v(43.08, 77.28) * mm, "end": v(43.08, 37.33) * mm});
            skLineSegment(sketch, "E401", {"start": v(4.43, 77.84) * mm, "end": v(4.85, 77.84) * mm});
            skLineSegment(sketch, "E402", {"start": v(4.85, 77.84) * mm, "end": v(5.26, 77.84) * mm});
            skLineSegment(sketch, "E403", {"start": v(5.26, 77.84) * mm, "end": v(5.68, 77.82) * mm});
            skLineSegment(sketch, "E404", {"start": v(5.68, 77.82) * mm, "end": v(6.1, 77.79) * mm});
            skLineSegment(sketch, "E405", {"start": v(6.1, 77.79) * mm, "end": v(6.51, 77.75) * mm});
            skLineSegment(sketch, "E406", {"start": v(6.51, 77.75) * mm, "end": v(6.93, 77.7) * mm});
            skLineSegment(sketch, "E407", {"start": v(6.93, 77.7) * mm, "end": v(7.34, 77.64) * mm});
            skLineSegment(sketch, "E408", {"start": v(7.34, 77.64) * mm, "end": v(7.75, 77.57) * mm});
            skLineSegment(sketch, "E409", {"start": v(7.75, 77.57) * mm, "end": v(8.16, 77.5) * mm});
            skLineSegment(sketch, "E410", {"start": v(8.16, 77.5) * mm, "end": v(8.56, 77.4) * mm});
            skLineSegment(sketch, "E411", {"start": v(8.56, 77.4) * mm, "end": v(8.96, 77.3) * mm});
            skLineSegment(sketch, "E412", {"start": v(8.96, 77.3) * mm, "end": v(9.36, 77.2) * mm});
            skLineSegment(sketch, "E413", {"start": v(9.36, 77.2) * mm, "end": v(9.76, 77.08) * mm});
            skLineSegment(sketch, "E414", {"start": v(9.76, 77.08) * mm, "end": v(10.15, 76.95) * mm});
            skLineSegment(sketch, "E415", {"start": v(10.15, 76.95) * mm, "end": v(10.54, 76.8) * mm});
            skLineSegment(sketch, "E416", {"start": v(10.54, 76.8) * mm, "end": v(10.93, 76.66) * mm});
            skLineSegment(sketch, "E417", {"start": v(10.93, 76.66) * mm, "end": v(11.31, 76.5) * mm});
            skLineSegment(sketch, "E418", {"start": v(11.31, 76.5) * mm, "end": v(11.69, 76.33) * mm});
            skLineSegment(sketch, "E419", {"start": v(11.69, 76.33) * mm, "end": v(12.06, 76.16) * mm});
            skLineSegment(sketch, "E420", {"start": v(12.06, 76.16) * mm, "end": v(12.43, 75.97) * mm});
            skLineSegment(sketch, "E421", {"start": v(12.43, 75.97) * mm, "end": v(12.8, 75.78) * mm});
            skLineSegment(sketch, "E422", {"start": v(12.8, 75.78) * mm, "end": v(13.16, 75.57) * mm});
            skLineSegment(sketch, "E423", {"start": v(13.16, 75.57) * mm, "end": v(13.51, 75.36) * mm});
            skLineSegment(sketch, "E424", {"start": v(13.51, 75.36) * mm, "end": v(13.86, 75.14) * mm});
            skLineSegment(sketch, "E425", {"start": v(13.86, 75.14) * mm, "end": v(14.21, 74.9) * mm});
            skLineSegment(sketch, "E426", {"start": v(14.21, 74.9) * mm, "end": v(14.55, 74.67) * mm});
            skLineSegment(sketch, "E427", {"start": v(14.55, 74.67) * mm, "end": v(14.88, 74.42) * mm});
            skLineSegment(sketch, "E428", {"start": v(14.88, 74.42) * mm, "end": v(15.21, 74.16) * mm});
            skLineSegment(sketch, "E429", {"start": v(15.21, 74.16) * mm, "end": v(15.53, 73.9) * mm});
            skLineSegment(sketch, "E430", {"start": v(15.53, 73.9) * mm, "end": v(15.85, 73.62) * mm});
            skLineSegment(sketch, "E431", {"start": v(15.85, 73.62) * mm, "end": v(16.16, 73.34) * mm});
            skLineSegment(sketch, "E432", {"start": v(16.16, 73.34) * mm, "end": v(16.46, 73.04) * mm});
            skLineSegment(sketch, "E433", {"start": v(16.46, 73.04) * mm, "end": v(16.81, 72.66) * mm});
            skLineSegment(sketch, "E434", {"start": v(16.81, 72.66) * mm, "end": v(17.15, 72.28) * mm});
            skLineSegment(sketch, "E435", {"start": v(17.15, 72.28) * mm, "end": v(17.48, 71.88) * mm});
            skLineSegment(sketch, "E436", {"start": v(17.48, 71.88) * mm, "end": v(17.8, 71.48) * mm});
            skLineSegment(sketch, "E437", {"start": v(17.8, 71.48) * mm, "end": v(18.1, 71.07) * mm});
            skLineSegment(sketch, "E438", {"start": v(18.1, 71.07) * mm, "end": v(18.4, 70.65) * mm});
            skLineSegment(sketch, "E439", {"start": v(18.4, 70.65) * mm, "end": v(18.69, 70.23) * mm});
            skLineSegment(sketch, "E440", {"start": v(18.69, 70.23) * mm, "end": v(18.96, 69.8) * mm});
            skLineSegment(sketch, "E441", {"start": v(18.96, 69.8) * mm, "end": v(19.23, 69.36) * mm});
            skLineSegment(sketch, "E442", {"start": v(19.23, 69.36) * mm, "end": v(19.48, 68.91) * mm});
            skLineSegment(sketch, "E443", {"start": v(19.48, 68.91) * mm, "end": v(19.73, 68.47) * mm});
            skLineSegment(sketch, "E444", {"start": v(19.73, 68.47) * mm, "end": v(19.96, 68.01) * mm});
            skLineSegment(sketch, "E445", {"start": v(19.96, 68.01) * mm, "end": v(20.18, 67.55) * mm});
            skLineSegment(sketch, "E446", {"start": v(20.18, 67.55) * mm, "end": v(20.39, 67.09) * mm});
            skLineSegment(sketch, "E447", {"start": v(20.39, 67.09) * mm, "end": v(20.58, 66.62) * mm});
            skLineSegment(sketch, "E448", {"start": v(20.58, 66.62) * mm, "end": v(20.77, 66.14) * mm});
            skLineSegment(sketch, "E449", {"start": v(20.77, 66.14) * mm, "end": v(20.94, 65.66) * mm});
            skLineSegment(sketch, "E450", {"start": v(20.94, 65.66) * mm, "end": v(21.1, 65.18) * mm});
            skLineSegment(sketch, "E451", {"start": v(21.1, 65.18) * mm, "end": v(21.25, 64.7) * mm});
            skLineSegment(sketch, "E452", {"start": v(21.25, 64.7) * mm, "end": v(21.4, 64.2) * mm});
            skLineSegment(sketch, "E453", {"start": v(21.4, 64.2) * mm, "end": v(21.52, 63.7) * mm});
            skLineSegment(sketch, "E454", {"start": v(21.52, 63.7) * mm, "end": v(21.63, 63.21) * mm});
            skLineSegment(sketch, "E455", {"start": v(21.63, 63.21) * mm, "end": v(21.73, 62.71) * mm});
            skLineSegment(sketch, "E456", {"start": v(21.73, 62.71) * mm, "end": v(21.82, 62.2) * mm});
            skLineSegment(sketch, "E457", {"start": v(21.82, 62.2) * mm, "end": v(21.9, 61.7) * mm});
            skLineSegment(sketch, "E458", {"start": v(21.9, 61.7) * mm, "end": v(21.97, 61.2) * mm});
            skLineSegment(sketch, "E459", {"start": v(21.97, 61.2) * mm, "end": v(22.02, 60.69) * mm});
            skLineSegment(sketch, "E460", {"start": v(22.02, 60.69) * mm, "end": v(22.06, 60.17) * mm});
            skLineSegment(sketch, "E461", {"start": v(22.06, 60.17) * mm, "end": v(22.08, 59.66) * mm});
            skLineSegment(sketch, "E462", {"start": v(22.08, 59.66) * mm, "end": v(22.1, 59.15) * mm});
            skLineSegment(sketch, "E463", {"start": v(22.1, 59.15) * mm, "end": v(22.1, 58.63) * mm});
            skLineSegment(sketch, "E464", {"start": v(22.1, 58.63) * mm, "end": v(22.09, 58.11) * mm});
            skLineSegment(sketch, "E465", {"start": v(22.09, 58.11) * mm, "end": v(22.1, 57.55) * mm});
            skLineSegment(sketch, "E466", {"start": v(22.1, 57.55) * mm, "end": v(22.1, 57) * mm});
            skLineSegment(sketch, "E467", {"start": v(22.1, 57) * mm, "end": v(22.1, 56.43) * mm});
            skLineSegment(sketch, "E468", {"start": v(22.1, 56.43) * mm, "end": v(22.07, 55.88) * mm});
            skLineSegment(sketch, "E469", {"start": v(22.07, 55.88) * mm, "end": v(22.03, 55.32) * mm});
            skLineSegment(sketch, "E470", {"start": v(22.03, 55.32) * mm, "end": v(21.97, 54.77) * mm});
            skLineSegment(sketch, "E471", {"start": v(21.97, 54.77) * mm, "end": v(21.9, 54.21) * mm});
            skLineSegment(sketch, "E472", {"start": v(21.9, 54.21) * mm, "end": v(21.82, 53.67) * mm});
            skLineSegment(sketch, "E473", {"start": v(21.82, 53.67) * mm, "end": v(21.73, 53.12) * mm});
            skLineSegment(sketch, "E474", {"start": v(21.73, 53.12) * mm, "end": v(21.62, 52.58) * mm});
            skLineSegment(sketch, "E475", {"start": v(21.62, 52.58) * mm, "end": v(21.5, 52.04) * mm});
            skLineSegment(sketch, "E476", {"start": v(21.5, 52.04) * mm, "end": v(21.36, 51.5) * mm});
            skLineSegment(sketch, "E477", {"start": v(21.36, 51.5) * mm, "end": v(21.2, 50.97) * mm});
            skLineSegment(sketch, "E478", {"start": v(21.2, 50.97) * mm, "end": v(21.05, 50.44) * mm});
            skLineSegment(sketch, "E479", {"start": v(21.05, 50.44) * mm, "end": v(20.87, 49.91) * mm});
            skLineSegment(sketch, "E480", {"start": v(20.87, 49.91) * mm, "end": v(20.68, 49.4) * mm});
            skLineSegment(sketch, "E481", {"start": v(20.68, 49.4) * mm, "end": v(20.48, 48.88) * mm});
            skLineSegment(sketch, "E482", {"start": v(20.48, 48.88) * mm, "end": v(20.27, 48.37) * mm});
            skLineSegment(sketch, "E483", {"start": v(20.27, 48.37) * mm, "end": v(20.04, 47.86) * mm});
            skLineSegment(sketch, "E484", {"start": v(20.04, 47.86) * mm, "end": v(19.8, 47.36) * mm});
            skLineSegment(sketch, "E485", {"start": v(19.8, 47.36) * mm, "end": v(19.55, 46.87) * mm});
            skLineSegment(sketch, "E486", {"start": v(19.55, 46.87) * mm, "end": v(19.29, 46.38) * mm});
            skLineSegment(sketch, "E487", {"start": v(19.29, 46.38) * mm, "end": v(19.01, 45.9) * mm});
            skLineSegment(sketch, "E488", {"start": v(19.01, 45.9) * mm, "end": v(18.73, 45.43) * mm});
            skLineSegment(sketch, "E489", {"start": v(18.73, 45.43) * mm, "end": v(18.43, 44.96) * mm});
            skLineSegment(sketch, "E490", {"start": v(18.43, 44.96) * mm, "end": v(18.11, 44.5) * mm});
            skLineSegment(sketch, "E491", {"start": v(18.11, 44.5) * mm, "end": v(17.79, 44.05) * mm});
            skLineSegment(sketch, "E492", {"start": v(17.79, 44.05) * mm, "end": v(17.45, 43.6) * mm});
            skLineSegment(sketch, "E493", {"start": v(17.45, 43.6) * mm, "end": v(17.1, 43.17) * mm});
            skLineSegment(sketch, "E494", {"start": v(17.1, 43.17) * mm, "end": v(16.75, 42.74) * mm});
            skLineSegment(sketch, "E495", {"start": v(16.75, 42.74) * mm, "end": v(16.38, 42.32) * mm});
            skLineSegment(sketch, "E496", {"start": v(16.38, 42.32) * mm, "end": v(16, 41.9) * mm});
            skLineSegment(sketch, "E497", {"start": v(16, 41.9) * mm, "end": v(15.71, 41.62) * mm});
            skLineSegment(sketch, "E498", {"start": v(15.71, 41.62) * mm, "end": v(15.42, 41.33) * mm});
            skLineSegment(sketch, "E499", {"start": v(15.42, 41.33) * mm, "end": v(15.12, 41.06) * mm});
            skLineSegment(sketch, "E500", {"start": v(15.12, 41.06) * mm, "end": v(14.81, 40.8) * mm});
            skLineSegment(sketch, "E501", {"start": v(14.81, 40.8) * mm, "end": v(14.5, 40.54) * mm});
            skLineSegment(sketch, "E502", {"start": v(14.5, 40.54) * mm, "end": v(14.18, 40.29) * mm});
            skLineSegment(sketch, "E503", {"start": v(14.18, 40.29) * mm, "end": v(13.86, 40.05) * mm});
            skLineSegment(sketch, "E504", {"start": v(13.86, 40.05) * mm, "end": v(13.53, 39.82) * mm});
            skLineSegment(sketch, "E505", {"start": v(13.53, 39.82) * mm, "end": v(13.2, 39.6) * mm});
            skLineSegment(sketch, "E506", {"start": v(13.2, 39.6) * mm, "end": v(12.85, 39.38) * mm});
            skLineSegment(sketch, "E507", {"start": v(12.85, 39.38) * mm, "end": v(12.5, 39.17) * mm});
            skLineSegment(sketch, "E508", {"start": v(12.5, 39.17) * mm, "end": v(12.16, 38.98) * mm});
            skLineSegment(sketch, "E509", {"start": v(12.16, 38.98) * mm, "end": v(11.8, 38.8) * mm});
            skLineSegment(sketch, "E510", {"start": v(11.8, 38.8) * mm, "end": v(11.44, 38.61) * mm});
            skLineSegment(sketch, "E511", {"start": v(11.44, 38.61) * mm, "end": v(11.08, 38.44) * mm});
            skLineSegment(sketch, "E512", {"start": v(11.08, 38.44) * mm, "end": v(10.71, 38.29) * mm});
            skLineSegment(sketch, "E513", {"start": v(10.71, 38.29) * mm, "end": v(10.34, 38.14) * mm});
            skLineSegment(sketch, "E514", {"start": v(10.34, 38.14) * mm, "end": v(9.96, 38) * mm});
            skLineSegment(sketch, "E515", {"start": v(9.96, 38) * mm, "end": v(9.58, 37.87) * mm});
            skLineSegment(sketch, "E516", {"start": v(9.58, 37.87) * mm, "end": v(9.2, 37.74) * mm});
            skLineSegment(sketch, "E517", {"start": v(9.2, 37.74) * mm, "end": v(8.81, 37.63) * mm});
            skLineSegment(sketch, "E518", {"start": v(8.81, 37.63) * mm, "end": v(8.43, 37.53) * mm});
            skLineSegment(sketch, "E519", {"start": v(8.43, 37.53) * mm, "end": v(8.03, 37.44) * mm});
            skLineSegment(sketch, "E520", {"start": v(8.03, 37.44) * mm, "end": v(7.64, 37.36) * mm});
            skLineSegment(sketch, "E521", {"start": v(7.64, 37.36) * mm, "end": v(7.24, 37.29) * mm});
            skLineSegment(sketch, "E522", {"start": v(7.24, 37.29) * mm, "end": v(6.84, 37.23) * mm});
            skLineSegment(sketch, "E523", {"start": v(6.84, 37.23) * mm, "end": v(6.44, 37.18) * mm});
            skLineSegment(sketch, "E524", {"start": v(6.44, 37.18) * mm, "end": v(6.04, 37.14) * mm});
            skLineSegment(sketch, "E525", {"start": v(6.04, 37.14) * mm, "end": v(5.64, 37.1) * mm});
            skLineSegment(sketch, "E526", {"start": v(5.64, 37.1) * mm, "end": v(5.23, 37.09) * mm});
            skLineSegment(sketch, "E527", {"start": v(5.23, 37.09) * mm, "end": v(4.83, 37.08) * mm});
            skLineSegment(sketch, "E528", {"start": v(4.83, 37.08) * mm, "end": v(4.42, 37.08) * mm});
            skLineSegment(sketch, "E529", {"start": v(4.42, 37.08) * mm, "end": v(4, 37.08) * mm});
            skLineSegment(sketch, "E530", {"start": v(4, 37.08) * mm, "end": v(3.6, 37.1) * mm});
            skLineSegment(sketch, "E531", {"start": v(3.6, 37.1) * mm, "end": v(3.18, 37.12) * mm});
            skLineSegment(sketch, "E532", {"start": v(3.18, 37.12) * mm, "end": v(2.77, 37.16) * mm});
            skLineSegment(sketch, "E533", {"start": v(2.77, 37.16) * mm, "end": v(2.36, 37.2) * mm});
            skLineSegment(sketch, "E534", {"start": v(2.36, 37.2) * mm, "end": v(1.95, 37.26) * mm});
            skLineSegment(sketch, "E535", {"start": v(1.95, 37.26) * mm, "end": v(1.55, 37.33) * mm});
            skLineSegment(sketch, "E536", {"start": v(1.55, 37.33) * mm, "end": v(1.15, 37.4) * mm});
            skLineSegment(sketch, "E537", {"start": v(1.15, 37.4) * mm, "end": v(0.75, 37.5) * mm});
            skLineSegment(sketch, "E538", {"start": v(0.75, 37.5) * mm, "end": v(0.35, 37.6) * mm});
            skLineSegment(sketch, "E539", {"start": v(0.35, 37.6) * mm, "end": v(-0.04, 37.7) * mm});
            skLineSegment(sketch, "E540", {"start": v(-0.04, 37.7) * mm, "end": v(-0.43, 37.82) * mm});
            skLineSegment(sketch, "E541", {"start": v(-0.43, 37.82) * mm, "end": v(-0.82, 37.94) * mm});
            skLineSegment(sketch, "E542", {"start": v(-0.82, 37.94) * mm, "end": v(-1.2, 38.08) * mm});
            skLineSegment(sketch, "E543", {"start": v(-1.2, 38.08) * mm, "end": v(-1.59, 38.23) * mm});
            skLineSegment(sketch, "E544", {"start": v(-1.59, 38.23) * mm, "end": v(-1.96, 38.39) * mm});
            skLineSegment(sketch, "E545", {"start": v(-1.96, 38.39) * mm, "end": v(-2.34, 38.55) * mm});
            skLineSegment(sketch, "E546", {"start": v(-2.34, 38.55) * mm, "end": v(-2.7, 38.73) * mm});
            skLineSegment(sketch, "E547", {"start": v(-2.7, 38.73) * mm, "end": v(-3.07, 38.91) * mm});
            skLineSegment(sketch, "E548", {"start": v(-3.07, 38.91) * mm, "end": v(-3.43, 39.1) * mm});
            skLineSegment(sketch, "E549", {"start": v(-3.43, 39.1) * mm, "end": v(-3.78, 39.31) * mm});
            skLineSegment(sketch, "E550", {"start": v(-3.78, 39.31) * mm, "end": v(-4.13, 39.52) * mm});
            skLineSegment(sketch, "E551", {"start": v(-4.13, 39.52) * mm, "end": v(-4.47, 39.74) * mm});
            skLineSegment(sketch, "E552", {"start": v(-4.47, 39.74) * mm, "end": v(-4.8, 39.97) * mm});
            skLineSegment(sketch, "E553", {"start": v(-4.8, 39.97) * mm, "end": v(-5.14, 40.21) * mm});
            skLineSegment(sketch, "E554", {"start": v(-5.14, 40.21) * mm, "end": v(-5.47, 40.46) * mm});
            skLineSegment(sketch, "E555", {"start": v(-5.47, 40.46) * mm, "end": v(-5.79, 40.72) * mm});
            skLineSegment(sketch, "E556", {"start": v(-5.79, 40.72) * mm, "end": v(-6.1, 40.98) * mm});
            skLineSegment(sketch, "E557", {"start": v(-6.1, 40.98) * mm, "end": v(-6.4, 41.26) * mm});
            skLineSegment(sketch, "E558", {"start": v(-6.4, 41.26) * mm, "end": v(-6.71, 41.54) * mm});
            skLineSegment(sketch, "E559", {"start": v(-6.71, 41.54) * mm, "end": v(-7, 41.83) * mm});
            skLineSegment(sketch, "E560", {"start": v(-7, 41.83) * mm, "end": v(-7.3, 42.13) * mm});
            skLineSegment(sketch, "E561", {"start": v(-7.3, 42.13) * mm, "end": v(-7.66, 42.54) * mm});
            skLineSegment(sketch, "E562", {"start": v(-7.66, 42.54) * mm, "end": v(-8.02, 42.96) * mm});
            skLineSegment(sketch, "E563", {"start": v(-8.02, 42.96) * mm, "end": v(-8.37, 43.38) * mm});
            skLineSegment(sketch, "E564", {"start": v(-8.37, 43.38) * mm, "end": v(-8.7, 43.82) * mm});
            skLineSegment(sketch, "E565", {"start": v(-8.7, 43.82) * mm, "end": v(-9.03, 44.26) * mm});
            skLineSegment(sketch, "E566", {"start": v(-9.03, 44.26) * mm, "end": v(-9.34, 44.7) * mm});
            skLineSegment(sketch, "E567", {"start": v(-9.34, 44.7) * mm, "end": v(-9.64, 45.16) * mm});
            skLineSegment(sketch, "E568", {"start": v(-9.64, 45.16) * mm, "end": v(-9.93, 45.63) * mm});
            skLineSegment(sketch, "E569", {"start": v(-9.93, 45.63) * mm, "end": v(-10.21, 46.1) * mm});
            skLineSegment(sketch, "E570", {"start": v(-10.21, 46.1) * mm, "end": v(-10.48, 46.57) * mm});
            skLineSegment(sketch, "E571", {"start": v(-10.48, 46.57) * mm, "end": v(-10.73, 47.05) * mm});
            skLineSegment(sketch, "E572", {"start": v(-10.73, 47.05) * mm, "end": v(-10.97, 47.54) * mm});
            skLineSegment(sketch, "E573", {"start": v(-10.97, 47.54) * mm, "end": v(-11.2, 48.04) * mm});
            skLineSegment(sketch, "E574", {"start": v(-11.2, 48.04) * mm, "end": v(-11.42, 48.53) * mm});
            skLineSegment(sketch, "E575", {"start": v(-11.42, 48.53) * mm, "end": v(-11.63, 49.04) * mm});
            skLineSegment(sketch, "E576", {"start": v(-11.63, 49.04) * mm, "end": v(-11.82, 49.55) * mm});
            skLineSegment(sketch, "E577", {"start": v(-11.82, 49.55) * mm, "end": v(-12, 50.06) * mm});
            skLineSegment(sketch, "E578", {"start": v(-12, 50.06) * mm, "end": v(-12.17, 50.58) * mm});
            skLineSegment(sketch, "E579", {"start": v(-12.17, 50.58) * mm, "end": v(-12.32, 51.1) * mm});
            skLineSegment(sketch, "E580", {"start": v(-12.32, 51.1) * mm, "end": v(-12.46, 51.63) * mm});
            skLineSegment(sketch, "E581", {"start": v(-12.46, 51.63) * mm, "end": v(-12.6, 52.15) * mm});
            skLineSegment(sketch, "E582", {"start": v(-12.6, 52.15) * mm, "end": v(-12.7, 52.69) * mm});
            skLineSegment(sketch, "E583", {"start": v(-12.7, 52.69) * mm, "end": v(-12.8, 53.22) * mm});
            skLineSegment(sketch, "E584", {"start": v(-12.8, 53.22) * mm, "end": v(-12.9, 53.76) * mm});
            skLineSegment(sketch, "E585", {"start": v(-12.9, 53.76) * mm, "end": v(-12.97, 54.3) * mm});
            skLineSegment(sketch, "E586", {"start": v(-12.97, 54.3) * mm, "end": v(-13.04, 54.84) * mm});
            skLineSegment(sketch, "E587", {"start": v(-13.04, 54.84) * mm, "end": v(-13.09, 55.4) * mm});
            skLineSegment(sketch, "E588", {"start": v(-13.09, 55.4) * mm, "end": v(-13.12, 55.94) * mm});
            skLineSegment(sketch, "E589", {"start": v(-13.12, 55.94) * mm, "end": v(-13.14, 56.49) * mm});
            skLineSegment(sketch, "E590", {"start": v(-13.14, 56.49) * mm, "end": v(-13.15, 57.04) * mm});
            skLineSegment(sketch, "E591", {"start": v(-13.15, 57.04) * mm, "end": v(-13.15, 57.59) * mm});
            skLineSegment(sketch, "E592", {"start": v(-13.15, 57.59) * mm, "end": v(-13.13, 58.14) * mm});
            skLineSegment(sketch, "E593", {"start": v(-13.13, 58.14) * mm, "end": v(-13.13, 58.65) * mm});
            skLineSegment(sketch, "E594", {"start": v(-13.13, 58.65) * mm, "end": v(-13.13, 59.17) * mm});
            skLineSegment(sketch, "E595", {"start": v(-13.13, 59.17) * mm, "end": v(-13.11, 59.68) * mm});
            skLineSegment(sketch, "E596", {"start": v(-13.11, 59.68) * mm, "end": v(-13.08, 60.2) * mm});
            skLineSegment(sketch, "E597", {"start": v(-13.08, 60.2) * mm, "end": v(-13.04, 60.7) * mm});
            skLineSegment(sketch, "E598", {"start": v(-13.04, 60.7) * mm, "end": v(-12.98, 61.2) * mm});
            skLineSegment(sketch, "E599", {"start": v(-12.98, 61.2) * mm, "end": v(-12.91, 61.71) * mm});
            skLineSegment(sketch, "E600", {"start": v(-12.91, 61.71) * mm, "end": v(-12.83, 62.22) * mm});
            skLineSegment(sketch, "E601", {"start": v(-12.83, 62.22) * mm, "end": v(-12.74, 62.72) * mm});
            skLineSegment(sketch, "E602", {"start": v(-12.74, 62.72) * mm, "end": v(-12.63, 63.21) * mm});
            skLineSegment(sketch, "E603", {"start": v(-12.63, 63.21) * mm, "end": v(-12.51, 63.7) * mm});
            skLineSegment(sketch, "E604", {"start": v(-12.51, 63.7) * mm, "end": v(-12.38, 64.2) * mm});
            skLineSegment(sketch, "E605", {"start": v(-12.38, 64.2) * mm, "end": v(-12.24, 64.69) * mm});
            skLineSegment(sketch, "E606", {"start": v(-12.24, 64.69) * mm, "end": v(-12.09, 65.17) * mm});
            skLineSegment(sketch, "E607", {"start": v(-12.09, 65.17) * mm, "end": v(-11.92, 65.65) * mm});
            skLineSegment(sketch, "E608", {"start": v(-11.92, 65.65) * mm, "end": v(-11.74, 66.12) * mm});
            skLineSegment(sketch, "E609", {"start": v(-11.74, 66.12) * mm, "end": v(-11.55, 66.6) * mm});
            skLineSegment(sketch, "E610", {"start": v(-11.55, 66.6) * mm, "end": v(-11.35, 67.06) * mm});
            skLineSegment(sketch, "E611", {"start": v(-11.35, 67.06) * mm, "end": v(-11.14, 67.52) * mm});
            skLineSegment(sketch, "E612", {"start": v(-11.14, 67.52) * mm, "end": v(-10.91, 67.97) * mm});
            skLineSegment(sketch, "E613", {"start": v(-10.91, 67.97) * mm, "end": v(-10.68, 68.42) * mm});
            skLineSegment(sketch, "E614", {"start": v(-10.68, 68.42) * mm, "end": v(-10.43, 68.87) * mm});
            skLineSegment(sketch, "E615", {"start": v(-10.43, 68.87) * mm, "end": v(-10.17, 69.3) * mm});
            skLineSegment(sketch, "E616", {"start": v(-10.17, 69.3) * mm, "end": v(-9.9, 69.74) * mm});
            skLineSegment(sketch, "E617", {"start": v(-9.9, 69.74) * mm, "end": v(-9.62, 70.16) * mm});
            skLineSegment(sketch, "E618", {"start": v(-9.62, 70.16) * mm, "end": v(-9.33, 70.58) * mm});
            skLineSegment(sketch, "E619", {"start": v(-9.33, 70.58) * mm, "end": v(-9.03, 71) * mm});
            skLineSegment(sketch, "E620", {"start": v(-9.03, 71) * mm, "end": v(-8.72, 71.4) * mm});
            skLineSegment(sketch, "E621", {"start": v(-8.72, 71.4) * mm, "end": v(-8.4, 71.8) * mm});
            skLineSegment(sketch, "E622", {"start": v(-8.4, 71.8) * mm, "end": v(-8.06, 72.19) * mm});
            skLineSegment(sketch, "E623", {"start": v(-8.06, 72.19) * mm, "end": v(-7.72, 72.57) * mm});
            skLineSegment(sketch, "E624", {"start": v(-7.72, 72.57) * mm, "end": v(-7.36, 72.94) * mm});
            skLineSegment(sketch, "E625", {"start": v(-7.36, 72.94) * mm, "end": v(-7.07, 73.23) * mm});
            skLineSegment(sketch, "E626", {"start": v(-7.07, 73.23) * mm, "end": v(-6.77, 73.52) * mm});
            skLineSegment(sketch, "E627", {"start": v(-6.77, 73.52) * mm, "end": v(-6.46, 73.8) * mm});
            skLineSegment(sketch, "E628", {"start": v(-6.46, 73.8) * mm, "end": v(-6.15, 74.06) * mm});
            skLineSegment(sketch, "E629", {"start": v(-6.15, 74.06) * mm, "end": v(-5.83, 74.31) * mm});
            skLineSegment(sketch, "E630", {"start": v(-5.83, 74.31) * mm, "end": v(-5.5, 74.56) * mm});
            skLineSegment(sketch, "E631", {"start": v(-5.5, 74.56) * mm, "end": v(-5.17, 74.8) * mm});
            skLineSegment(sketch, "E632", {"start": v(-5.17, 74.8) * mm, "end": v(-4.84, 75.04) * mm});
            skLineSegment(sketch, "E633", {"start": v(-4.84, 75.04) * mm, "end": v(-4.5, 75.26) * mm});
            skLineSegment(sketch, "E634", {"start": v(-4.5, 75.26) * mm, "end": v(-4.15, 75.48) * mm});
            skLineSegment(sketch, "E635", {"start": v(-4.15, 75.48) * mm, "end": v(-3.8, 75.68) * mm});
            skLineSegment(sketch, "E636", {"start": v(-3.8, 75.68) * mm, "end": v(-3.44, 75.88) * mm});
            skLineSegment(sketch, "E637", {"start": v(-3.44, 75.88) * mm, "end": v(-3.07, 76.07) * mm});
            skLineSegment(sketch, "E638", {"start": v(-3.07, 76.07) * mm, "end": v(-2.7, 76.25) * mm});
            skLineSegment(sketch, "E639", {"start": v(-2.7, 76.25) * mm, "end": v(-2.34, 76.42) * mm});
            skLineSegment(sketch, "E640", {"start": v(-2.34, 76.42) * mm, "end": v(-1.96, 76.58) * mm});
            skLineSegment(sketch, "E641", {"start": v(-1.96, 76.58) * mm, "end": v(-1.59, 76.73) * mm});
            skLineSegment(sketch, "E642", {"start": v(-1.59, 76.73) * mm, "end": v(-1.2, 76.88) * mm});
            skLineSegment(sketch, "E643", {"start": v(-1.2, 76.88) * mm, "end": v(-0.82, 77) * mm});
            skLineSegment(sketch, "E644", {"start": v(-0.82, 77) * mm, "end": v(-0.43, 77.13) * mm});
            skLineSegment(sketch, "E645", {"start": v(-0.43, 77.13) * mm, "end": v(-0.04, 77.25) * mm});
            skLineSegment(sketch, "E646", {"start": v(-0.04, 77.25) * mm, "end": v(0.36, 77.35) * mm});
            skLineSegment(sketch, "E647", {"start": v(0.36, 77.35) * mm, "end": v(0.76, 77.44) * mm});
            skLineSegment(sketch, "E648", {"start": v(0.76, 77.44) * mm, "end": v(1.16, 77.53) * mm});
            skLineSegment(sketch, "E649", {"start": v(1.16, 77.53) * mm, "end": v(1.56, 77.6) * mm});
            skLineSegment(sketch, "E650", {"start": v(1.56, 77.6) * mm, "end": v(1.96, 77.67) * mm});
            skLineSegment(sketch, "E651", {"start": v(1.96, 77.67) * mm, "end": v(2.37, 77.72) * mm});
            skLineSegment(sketch, "E652", {"start": v(2.37, 77.72) * mm, "end": v(2.78, 77.77) * mm});
            skLineSegment(sketch, "E653", {"start": v(2.78, 77.77) * mm, "end": v(3.19, 77.8) * mm});
            skLineSegment(sketch, "E654", {"start": v(3.19, 77.8) * mm, "end": v(3.6, 77.82) * mm});
            skLineSegment(sketch, "E655", {"start": v(3.6, 77.82) * mm, "end": v(4.01, 77.84) * mm});
            skLineSegment(sketch, "E656", {"start": v(4.01, 77.84) * mm, "end": v(4.43, 77.84) * mm});
            skLineSegment(sketch, "E657", {"start": v(-39.82, 77.84) * mm, "end": v(-39.4, 77.84) * mm});
            skLineSegment(sketch, "E658", {"start": v(-39.4, 77.84) * mm, "end": v(-38.98, 77.84) * mm});
            skLineSegment(sketch, "E659", {"start": v(-38.98, 77.84) * mm, "end": v(-38.56, 77.82) * mm});
            skLineSegment(sketch, "E660", {"start": v(-38.56, 77.82) * mm, "end": v(-38.15, 77.79) * mm});
            skLineSegment(sketch, "E661", {"start": v(-38.15, 77.79) * mm, "end": v(-37.73, 77.75) * mm});
            skLineSegment(sketch, "E662", {"start": v(-37.73, 77.75) * mm, "end": v(-37.32, 77.7) * mm});
            skLineSegment(sketch, "E663", {"start": v(-37.32, 77.7) * mm, "end": v(-36.9, 77.64) * mm});
            skLineSegment(sketch, "E664", {"start": v(-36.9, 77.64) * mm, "end": v(-36.5, 77.57) * mm});
            skLineSegment(sketch, "E665", {"start": v(-36.5, 77.57) * mm, "end": v(-36.09, 77.5) * mm});
            skLineSegment(sketch, "E666", {"start": v(-36.09, 77.5) * mm, "end": v(-35.68, 77.4) * mm});
            skLineSegment(sketch, "E667", {"start": v(-35.68, 77.4) * mm, "end": v(-35.28, 77.3) * mm});
            skLineSegment(sketch, "E668", {"start": v(-35.28, 77.3) * mm, "end": v(-34.88, 77.2) * mm});
            skLineSegment(sketch, "E669", {"start": v(-34.88, 77.2) * mm, "end": v(-34.49, 77.08) * mm});
            skLineSegment(sketch, "E670", {"start": v(-34.49, 77.08) * mm, "end": v(-34.1, 76.95) * mm});
            skLineSegment(sketch, "E671", {"start": v(-34.1, 76.95) * mm, "end": v(-33.7, 76.8) * mm});
            skLineSegment(sketch, "E672", {"start": v(-33.7, 76.8) * mm, "end": v(-33.32, 76.66) * mm});
            skLineSegment(sketch, "E673", {"start": v(-33.32, 76.66) * mm, "end": v(-32.93, 76.5) * mm});
            skLineSegment(sketch, "E674", {"start": v(-32.93, 76.5) * mm, "end": v(-32.56, 76.33) * mm});
            skLineSegment(sketch, "E675", {"start": v(-32.56, 76.33) * mm, "end": v(-32.18, 76.16) * mm});
            skLineSegment(sketch, "E676", {"start": v(-32.18, 76.16) * mm, "end": v(-31.81, 75.97) * mm});
            skLineSegment(sketch, "E677", {"start": v(-31.81, 75.97) * mm, "end": v(-31.45, 75.78) * mm});
            skLineSegment(sketch, "E678", {"start": v(-31.45, 75.78) * mm, "end": v(-31.09, 75.57) * mm});
            skLineSegment(sketch, "E679", {"start": v(-31.09, 75.57) * mm, "end": v(-30.73, 75.36) * mm});
            skLineSegment(sketch, "E680", {"start": v(-30.73, 75.36) * mm, "end": v(-30.38, 75.14) * mm});
            skLineSegment(sketch, "E681", {"start": v(-30.38, 75.14) * mm, "end": v(-30.04, 74.9) * mm});
            skLineSegment(sketch, "E682", {"start": v(-30.04, 74.9) * mm, "end": v(-29.7, 74.67) * mm});
            skLineSegment(sketch, "E683", {"start": v(-29.7, 74.67) * mm, "end": v(-29.36, 74.42) * mm});
            skLineSegment(sketch, "E684", {"start": v(-29.36, 74.42) * mm, "end": v(-29.03, 74.16) * mm});
            skLineSegment(sketch, "E685", {"start": v(-29.03, 74.16) * mm, "end": v(-28.71, 73.9) * mm});
            skLineSegment(sketch, "E686", {"start": v(-28.71, 73.9) * mm, "end": v(-28.4, 73.62) * mm});
            skLineSegment(sketch, "E687", {"start": v(-28.4, 73.62) * mm, "end": v(-28.09, 73.34) * mm});
            skLineSegment(sketch, "E688", {"start": v(-28.09, 73.34) * mm, "end": v(-27.78, 73.04) * mm});
            skLineSegment(sketch, "E689", {"start": v(-27.78, 73.04) * mm, "end": v(-27.43, 72.66) * mm});
            skLineSegment(sketch, "E690", {"start": v(-27.43, 72.66) * mm, "end": v(-27.1, 72.28) * mm});
            skLineSegment(sketch, "E691", {"start": v(-27.1, 72.28) * mm, "end": v(-26.77, 71.88) * mm});
            skLineSegment(sketch, "E692", {"start": v(-26.77, 71.88) * mm, "end": v(-26.45, 71.48) * mm});
            skLineSegment(sketch, "E693", {"start": v(-26.45, 71.48) * mm, "end": v(-26.14, 71.07) * mm});
            skLineSegment(sketch, "E694", {"start": v(-26.14, 71.07) * mm, "end": v(-25.84, 70.65) * mm});
            skLineSegment(sketch, "E695", {"start": v(-25.84, 70.65) * mm, "end": v(-25.56, 70.23) * mm});
            skLineSegment(sketch, "E696", {"start": v(-25.56, 70.23) * mm, "end": v(-25.28, 69.8) * mm});
            skLineSegment(sketch, "E697", {"start": v(-25.28, 69.8) * mm, "end": v(-25.02, 69.36) * mm});
            skLineSegment(sketch, "E698", {"start": v(-25.02, 69.36) * mm, "end": v(-24.76, 68.91) * mm});
            skLineSegment(sketch, "E699", {"start": v(-24.76, 68.91) * mm, "end": v(-24.52, 68.47) * mm});
            skLineSegment(sketch, "E700", {"start": v(-24.52, 68.47) * mm, "end": v(-24.29, 68.01) * mm});
            skLineSegment(sketch, "E701", {"start": v(-24.29, 68.01) * mm, "end": v(-24.07, 67.55) * mm});
            skLineSegment(sketch, "E702", {"start": v(-24.07, 67.55) * mm, "end": v(-23.86, 67.09) * mm});
            skLineSegment(sketch, "E703", {"start": v(-23.86, 67.09) * mm, "end": v(-23.66, 66.62) * mm});
            skLineSegment(sketch, "E704", {"start": v(-23.66, 66.62) * mm, "end": v(-23.48, 66.14) * mm});
            skLineSegment(sketch, "E705", {"start": v(-23.48, 66.14) * mm, "end": v(-23.3, 65.66) * mm});
            skLineSegment(sketch, "E706", {"start": v(-23.3, 65.66) * mm, "end": v(-23.14, 65.18) * mm});
            skLineSegment(sketch, "E707", {"start": v(-23.14, 65.18) * mm, "end": v(-23, 64.7) * mm});
            skLineSegment(sketch, "E708", {"start": v(-23, 64.7) * mm, "end": v(-22.85, 64.2) * mm});
            skLineSegment(sketch, "E709", {"start": v(-22.85, 64.2) * mm, "end": v(-22.73, 63.7) * mm});
            skLineSegment(sketch, "E710", {"start": v(-22.73, 63.7) * mm, "end": v(-22.61, 63.21) * mm});
            skLineSegment(sketch, "E711", {"start": v(-22.61, 63.21) * mm, "end": v(-22.51, 62.71) * mm});
            skLineSegment(sketch, "E712", {"start": v(-22.51, 62.71) * mm, "end": v(-22.42, 62.2) * mm});
            skLineSegment(sketch, "E713", {"start": v(-22.42, 62.2) * mm, "end": v(-22.34, 61.7) * mm});
            skLineSegment(sketch, "E714", {"start": v(-22.34, 61.7) * mm, "end": v(-22.28, 61.2) * mm});
            skLineSegment(sketch, "E715", {"start": v(-22.28, 61.2) * mm, "end": v(-22.23, 60.69) * mm});
            skLineSegment(sketch, "E716", {"start": v(-22.23, 60.69) * mm, "end": v(-22.19, 60.17) * mm});
            skLineSegment(sketch, "E717", {"start": v(-22.19, 60.17) * mm, "end": v(-22.16, 59.66) * mm});
            skLineSegment(sketch, "E718", {"start": v(-22.16, 59.66) * mm, "end": v(-22.15, 59.15) * mm});
            skLineSegment(sketch, "E719", {"start": v(-22.15, 59.15) * mm, "end": v(-22.15, 58.63) * mm});
            skLineSegment(sketch, "E720", {"start": v(-22.15, 58.63) * mm, "end": v(-22.16, 58.11) * mm});
            skLineSegment(sketch, "E721", {"start": v(-22.16, 58.11) * mm, "end": v(-22.14, 57.55) * mm});
            skLineSegment(sketch, "E722", {"start": v(-22.14, 57.55) * mm, "end": v(-22.14, 57) * mm});
            skLineSegment(sketch, "E723", {"start": v(-22.14, 57) * mm, "end": v(-22.15, 56.43) * mm});
            skLineSegment(sketch, "E724", {"start": v(-22.15, 56.43) * mm, "end": v(-22.18, 55.88) * mm});
            skLineSegment(sketch, "E725", {"start": v(-22.18, 55.88) * mm, "end": v(-22.22, 55.32) * mm});
            skLineSegment(sketch, "E726", {"start": v(-22.22, 55.32) * mm, "end": v(-22.27, 54.77) * mm});
            skLineSegment(sketch, "E727", {"start": v(-22.27, 54.77) * mm, "end": v(-22.34, 54.21) * mm});
            skLineSegment(sketch, "E728", {"start": v(-22.34, 54.21) * mm, "end": v(-22.42, 53.67) * mm});
            skLineSegment(sketch, "E729", {"start": v(-22.42, 53.67) * mm, "end": v(-22.52, 53.12) * mm});
            skLineSegment(sketch, "E730", {"start": v(-22.52, 53.12) * mm, "end": v(-22.63, 52.58) * mm});
            skLineSegment(sketch, "E731", {"start": v(-22.63, 52.58) * mm, "end": v(-22.75, 52.04) * mm});
            skLineSegment(sketch, "E732", {"start": v(-22.75, 52.04) * mm, "end": v(-22.89, 51.5) * mm});
            skLineSegment(sketch, "E733", {"start": v(-22.89, 51.5) * mm, "end": v(-23.04, 50.97) * mm});
            skLineSegment(sketch, "E734", {"start": v(-23.04, 50.97) * mm, "end": v(-23.2, 50.44) * mm});
            skLineSegment(sketch, "E735", {"start": v(-23.2, 50.44) * mm, "end": v(-23.37, 49.91) * mm});
            skLineSegment(sketch, "E736", {"start": v(-23.37, 49.91) * mm, "end": v(-23.56, 49.4) * mm});
            skLineSegment(sketch, "E737", {"start": v(-23.56, 49.4) * mm, "end": v(-23.76, 48.88) * mm});
            skLineSegment(sketch, "E738", {"start": v(-23.76, 48.88) * mm, "end": v(-23.98, 48.37) * mm});
            skLineSegment(sketch, "E739", {"start": v(-23.98, 48.37) * mm, "end": v(-24.2, 47.86) * mm});
            skLineSegment(sketch, "E740", {"start": v(-24.2, 47.86) * mm, "end": v(-24.44, 47.36) * mm});
            skLineSegment(sketch, "E741", {"start": v(-24.44, 47.36) * mm, "end": v(-24.7, 46.87) * mm});
            skLineSegment(sketch, "E742", {"start": v(-24.7, 46.87) * mm, "end": v(-24.96, 46.38) * mm});
            skLineSegment(sketch, "E743", {"start": v(-24.96, 46.38) * mm, "end": v(-25.23, 45.9) * mm});
            skLineSegment(sketch, "E744", {"start": v(-25.23, 45.9) * mm, "end": v(-25.52, 45.43) * mm});
            skLineSegment(sketch, "E745", {"start": v(-25.52, 45.43) * mm, "end": v(-25.82, 44.96) * mm});
            skLineSegment(sketch, "E746", {"start": v(-25.82, 44.96) * mm, "end": v(-26.13, 44.5) * mm});
            skLineSegment(sketch, "E747", {"start": v(-26.13, 44.5) * mm, "end": v(-26.46, 44.05) * mm});
            skLineSegment(sketch, "E748", {"start": v(-26.46, 44.05) * mm, "end": v(-26.8, 43.6) * mm});
            skLineSegment(sketch, "E749", {"start": v(-26.8, 43.6) * mm, "end": v(-27.14, 43.17) * mm});
            skLineSegment(sketch, "E750", {"start": v(-27.14, 43.17) * mm, "end": v(-27.5, 42.74) * mm});
            skLineSegment(sketch, "E751", {"start": v(-27.5, 42.74) * mm, "end": v(-27.87, 42.32) * mm});
            skLineSegment(sketch, "E752", {"start": v(-27.87, 42.32) * mm, "end": v(-28.25, 41.9) * mm});
            skLineSegment(sketch, "E753", {"start": v(-28.25, 41.9) * mm, "end": v(-28.53, 41.62) * mm});
            skLineSegment(sketch, "E754", {"start": v(-28.53, 41.62) * mm, "end": v(-28.83, 41.33) * mm});
            skLineSegment(sketch, "E755", {"start": v(-28.83, 41.33) * mm, "end": v(-29.13, 41.06) * mm});
            skLineSegment(sketch, "E756", {"start": v(-29.13, 41.06) * mm, "end": v(-29.43, 40.8) * mm});
            skLineSegment(sketch, "E757", {"start": v(-29.43, 40.8) * mm, "end": v(-29.74, 40.54) * mm});
            skLineSegment(sketch, "E758", {"start": v(-29.74, 40.54) * mm, "end": v(-30.06, 40.29) * mm});
            skLineSegment(sketch, "E759", {"start": v(-30.06, 40.29) * mm, "end": v(-30.39, 40.05) * mm});
            skLineSegment(sketch, "E760", {"start": v(-30.39, 40.05) * mm, "end": v(-30.72, 39.82) * mm});
            skLineSegment(sketch, "E761", {"start": v(-30.72, 39.82) * mm, "end": v(-31.05, 39.6) * mm});
            skLineSegment(sketch, "E762", {"start": v(-31.05, 39.6) * mm, "end": v(-31.4, 39.38) * mm});
            skLineSegment(sketch, "E763", {"start": v(-31.4, 39.38) * mm, "end": v(-31.74, 39.17) * mm});
            skLineSegment(sketch, "E764", {"start": v(-31.74, 39.17) * mm, "end": v(-32.09, 38.98) * mm});
            skLineSegment(sketch, "E765", {"start": v(-32.09, 38.98) * mm, "end": v(-32.44, 38.8) * mm});
            skLineSegment(sketch, "E766", {"start": v(-32.44, 38.8) * mm, "end": v(-32.8, 38.61) * mm});
            skLineSegment(sketch, "E767", {"start": v(-32.8, 38.61) * mm, "end": v(-33.17, 38.44) * mm});
            skLineSegment(sketch, "E768", {"start": v(-33.17, 38.44) * mm, "end": v(-33.54, 38.29) * mm});
            skLineSegment(sketch, "E769", {"start": v(-33.54, 38.29) * mm, "end": v(-33.9, 38.14) * mm});
            skLineSegment(sketch, "E770", {"start": v(-33.9, 38.14) * mm, "end": v(-34.28, 38) * mm});
            skLineSegment(sketch, "E771", {"start": v(-34.28, 38) * mm, "end": v(-34.66, 37.87) * mm});
            skLineSegment(sketch, "E772", {"start": v(-34.66, 37.87) * mm, "end": v(-35.05, 37.74) * mm});
            skLineSegment(sketch, "E773", {"start": v(-35.05, 37.74) * mm, "end": v(-35.43, 37.63) * mm});
            skLineSegment(sketch, "E774", {"start": v(-35.43, 37.63) * mm, "end": v(-35.82, 37.53) * mm});
            skLineSegment(sketch, "E775", {"start": v(-35.82, 37.53) * mm, "end": v(-36.21, 37.44) * mm});
            skLineSegment(sketch, "E776", {"start": v(-36.21, 37.44) * mm, "end": v(-36.6, 37.36) * mm});
            skLineSegment(sketch, "E777", {"start": v(-36.6, 37.36) * mm, "end": v(-37, 37.29) * mm});
            skLineSegment(sketch, "E778", {"start": v(-37, 37.29) * mm, "end": v(-37.4, 37.23) * mm});
            skLineSegment(sketch, "E779", {"start": v(-37.4, 37.23) * mm, "end": v(-37.8, 37.18) * mm});
            skLineSegment(sketch, "E780", {"start": v(-37.8, 37.18) * mm, "end": v(-38.2, 37.14) * mm});
            skLineSegment(sketch, "E781", {"start": v(-38.2, 37.14) * mm, "end": v(-38.6, 37.1) * mm});
            skLineSegment(sketch, "E782", {"start": v(-38.6, 37.1) * mm, "end": v(-39.01, 37.09) * mm});
            skLineSegment(sketch, "E783", {"start": v(-39.01, 37.09) * mm, "end": v(-39.42, 37.08) * mm});
            skLineSegment(sketch, "E784", {"start": v(-39.42, 37.08) * mm, "end": v(-39.83, 37.08) * mm});
            skLineSegment(sketch, "E785", {"start": v(-39.83, 37.08) * mm, "end": v(-40.24, 37.08) * mm});
            skLineSegment(sketch, "E786", {"start": v(-40.24, 37.08) * mm, "end": v(-40.65, 37.1) * mm});
            skLineSegment(sketch, "E787", {"start": v(-40.65, 37.1) * mm, "end": v(-41.07, 37.12) * mm});
            skLineSegment(sketch, "E788", {"start": v(-41.07, 37.12) * mm, "end": v(-41.48, 37.16) * mm});
            skLineSegment(sketch, "E789", {"start": v(-41.48, 37.16) * mm, "end": v(-41.89, 37.2) * mm});
            skLineSegment(sketch, "E790", {"start": v(-41.89, 37.2) * mm, "end": v(-42.3, 37.26) * mm});
            skLineSegment(sketch, "E791", {"start": v(-42.3, 37.26) * mm, "end": v(-42.7, 37.33) * mm});
            skLineSegment(sketch, "E792", {"start": v(-42.7, 37.33) * mm, "end": v(-43.1, 37.4) * mm});
            skLineSegment(sketch, "E793", {"start": v(-43.1, 37.4) * mm, "end": v(-43.5, 37.5) * mm});
            skLineSegment(sketch, "E794", {"start": v(-43.5, 37.5) * mm, "end": v(-43.9, 37.6) * mm});
            skLineSegment(sketch, "E795", {"start": v(-43.9, 37.6) * mm, "end": v(-44.29, 37.7) * mm});
            skLineSegment(sketch, "E796", {"start": v(-44.29, 37.7) * mm, "end": v(-44.68, 37.82) * mm});
            skLineSegment(sketch, "E797", {"start": v(-44.68, 37.82) * mm, "end": v(-45.07, 37.94) * mm});
            skLineSegment(sketch, "E798", {"start": v(-45.07, 37.94) * mm, "end": v(-45.45, 38.08) * mm});
            skLineSegment(sketch, "E799", {"start": v(-45.45, 38.08) * mm, "end": v(-45.83, 38.23) * mm});
            skLineSegment(sketch, "E800", {"start": v(-45.83, 38.23) * mm, "end": v(-46.2, 38.39) * mm});
            skLineSegment(sketch, "E801", {"start": v(-46.2, 38.39) * mm, "end": v(-46.58, 38.55) * mm});
            skLineSegment(sketch, "E802", {"start": v(-46.58, 38.55) * mm, "end": v(-46.95, 38.73) * mm});
            skLineSegment(sketch, "E803", {"start": v(-46.95, 38.73) * mm, "end": v(-47.31, 38.91) * mm});
            skLineSegment(sketch, "E804", {"start": v(-47.31, 38.91) * mm, "end": v(-47.67, 39.1) * mm});
            skLineSegment(sketch, "E805", {"start": v(-47.67, 39.1) * mm, "end": v(-48.02, 39.31) * mm});
            skLineSegment(sketch, "E806", {"start": v(-48.02, 39.31) * mm, "end": v(-48.37, 39.52) * mm});
            skLineSegment(sketch, "E807", {"start": v(-48.37, 39.52) * mm, "end": v(-48.72, 39.74) * mm});
            skLineSegment(sketch, "E808", {"start": v(-48.72, 39.74) * mm, "end": v(-49.05, 39.97) * mm});
            skLineSegment(sketch, "E809", {"start": v(-49.05, 39.97) * mm, "end": v(-49.39, 40.21) * mm});
            skLineSegment(sketch, "E810", {"start": v(-49.39, 40.21) * mm, "end": v(-49.71, 40.46) * mm});
            skLineSegment(sketch, "E811", {"start": v(-49.71, 40.46) * mm, "end": v(-50.03, 40.72) * mm});
            skLineSegment(sketch, "E812", {"start": v(-50.03, 40.72) * mm, "end": v(-50.35, 40.98) * mm});
            skLineSegment(sketch, "E813", {"start": v(-50.35, 40.98) * mm, "end": v(-50.66, 41.26) * mm});
            skLineSegment(sketch, "E814", {"start": v(-50.66, 41.26) * mm, "end": v(-50.96, 41.54) * mm});
            skLineSegment(sketch, "E815", {"start": v(-50.96, 41.54) * mm, "end": v(-51.25, 41.83) * mm});
            skLineSegment(sketch, "E816", {"start": v(-51.25, 41.83) * mm, "end": v(-51.54, 42.13) * mm});
            skLineSegment(sketch, "E817", {"start": v(-51.54, 42.13) * mm, "end": v(-51.9, 42.54) * mm});
            skLineSegment(sketch, "E818", {"start": v(-51.9, 42.54) * mm, "end": v(-52.27, 42.96) * mm});
            skLineSegment(sketch, "E819", {"start": v(-52.27, 42.96) * mm, "end": v(-52.61, 43.38) * mm});
            skLineSegment(sketch, "E820", {"start": v(-52.61, 43.38) * mm, "end": v(-52.95, 43.82) * mm});
            skLineSegment(sketch, "E821", {"start": v(-52.95, 43.82) * mm, "end": v(-53.27, 44.26) * mm});
            skLineSegment(sketch, "E822", {"start": v(-53.27, 44.26) * mm, "end": v(-53.59, 44.7) * mm});
            skLineSegment(sketch, "E823", {"start": v(-53.59, 44.7) * mm, "end": v(-53.89, 45.16) * mm});
            skLineSegment(sketch, "E824", {"start": v(-53.89, 45.16) * mm, "end": v(-54.18, 45.63) * mm});
            skLineSegment(sketch, "E825", {"start": v(-54.18, 45.63) * mm, "end": v(-54.46, 46.1) * mm});
            skLineSegment(sketch, "E826", {"start": v(-54.46, 46.1) * mm, "end": v(-54.72, 46.57) * mm});
            skLineSegment(sketch, "E827", {"start": v(-54.72, 46.57) * mm, "end": v(-54.98, 47.05) * mm});
            skLineSegment(sketch, "E828", {"start": v(-54.98, 47.05) * mm, "end": v(-55.22, 47.54) * mm});
            skLineSegment(sketch, "E829", {"start": v(-55.22, 47.54) * mm, "end": v(-55.45, 48.04) * mm});
            skLineSegment(sketch, "E830", {"start": v(-55.45, 48.04) * mm, "end": v(-55.67, 48.53) * mm});
            skLineSegment(sketch, "E831", {"start": v(-55.67, 48.53) * mm, "end": v(-55.87, 49.04) * mm});
            skLineSegment(sketch, "E832", {"start": v(-55.87, 49.04) * mm, "end": v(-56.06, 49.55) * mm});
            skLineSegment(sketch, "E833", {"start": v(-56.06, 49.55) * mm, "end": v(-56.24, 50.06) * mm});
            skLineSegment(sketch, "E834", {"start": v(-56.24, 50.06) * mm, "end": v(-56.41, 50.58) * mm});
            skLineSegment(sketch, "E835", {"start": v(-56.41, 50.58) * mm, "end": v(-56.57, 51.1) * mm});
            skLineSegment(sketch, "E836", {"start": v(-56.57, 51.1) * mm, "end": v(-56.7, 51.63) * mm});
            skLineSegment(sketch, "E837", {"start": v(-56.7, 51.63) * mm, "end": v(-56.84, 52.15) * mm});
            skLineSegment(sketch, "E838", {"start": v(-56.84, 52.15) * mm, "end": v(-56.95, 52.69) * mm});
            skLineSegment(sketch, "E839", {"start": v(-56.95, 52.69) * mm, "end": v(-57.05, 53.22) * mm});
            skLineSegment(sketch, "E840", {"start": v(-57.05, 53.22) * mm, "end": v(-57.14, 53.76) * mm});
            skLineSegment(sketch, "E841", {"start": v(-57.14, 53.76) * mm, "end": v(-57.22, 54.3) * mm});
            skLineSegment(sketch, "E842", {"start": v(-57.22, 54.3) * mm, "end": v(-57.28, 54.84) * mm});
            skLineSegment(sketch, "E843", {"start": v(-57.28, 54.84) * mm, "end": v(-57.33, 55.4) * mm});
            skLineSegment(sketch, "E844", {"start": v(-57.33, 55.4) * mm, "end": v(-57.37, 55.94) * mm});
            skLineSegment(sketch, "E845", {"start": v(-57.37, 55.94) * mm, "end": v(-57.39, 56.49) * mm});
            skLineSegment(sketch, "E846", {"start": v(-57.39, 56.49) * mm, "end": v(-57.4, 57.04) * mm});
            skLineSegment(sketch, "E847", {"start": v(-57.4, 57.04) * mm, "end": v(-57.4, 57.59) * mm});
            skLineSegment(sketch, "E848", {"start": v(-57.4, 57.59) * mm, "end": v(-57.37, 58.14) * mm});
            skLineSegment(sketch, "E849", {"start": v(-57.37, 58.14) * mm, "end": v(-57.38, 58.65) * mm});
            skLineSegment(sketch, "E850", {"start": v(-57.38, 58.65) * mm, "end": v(-57.38, 59.17) * mm});
            skLineSegment(sketch, "E851", {"start": v(-57.38, 59.17) * mm, "end": v(-57.36, 59.68) * mm});
            skLineSegment(sketch, "E852", {"start": v(-57.36, 59.68) * mm, "end": v(-57.33, 60.2) * mm});
            skLineSegment(sketch, "E853", {"start": v(-57.33, 60.2) * mm, "end": v(-57.28, 60.7) * mm});
            skLineSegment(sketch, "E854", {"start": v(-57.28, 60.7) * mm, "end": v(-57.23, 61.2) * mm});
            skLineSegment(sketch, "E855", {"start": v(-57.23, 61.2) * mm, "end": v(-57.16, 61.71) * mm});
            skLineSegment(sketch, "E856", {"start": v(-57.16, 61.71) * mm, "end": v(-57.08, 62.22) * mm});
            skLineSegment(sketch, "E857", {"start": v(-57.08, 62.22) * mm, "end": v(-56.98, 62.72) * mm});
            skLineSegment(sketch, "E858", {"start": v(-56.98, 62.72) * mm, "end": v(-56.88, 63.21) * mm});
            skLineSegment(sketch, "E859", {"start": v(-56.88, 63.21) * mm, "end": v(-56.76, 63.7) * mm});
            skLineSegment(sketch, "E860", {"start": v(-56.76, 63.7) * mm, "end": v(-56.63, 64.2) * mm});
            skLineSegment(sketch, "E861", {"start": v(-56.63, 64.2) * mm, "end": v(-56.49, 64.69) * mm});
            skLineSegment(sketch, "E862", {"start": v(-56.49, 64.69) * mm, "end": v(-56.33, 65.17) * mm});
            skLineSegment(sketch, "E863", {"start": v(-56.33, 65.17) * mm, "end": v(-56.17, 65.65) * mm});
            skLineSegment(sketch, "E864", {"start": v(-56.17, 65.65) * mm, "end": v(-55.99, 66.12) * mm});
            skLineSegment(sketch, "E865", {"start": v(-55.99, 66.12) * mm, "end": v(-55.8, 66.6) * mm});
            skLineSegment(sketch, "E866", {"start": v(-55.8, 66.6) * mm, "end": v(-55.6, 67.06) * mm});
            skLineSegment(sketch, "E867", {"start": v(-55.6, 67.06) * mm, "end": v(-55.38, 67.52) * mm});
            skLineSegment(sketch, "E868", {"start": v(-55.38, 67.52) * mm, "end": v(-55.16, 67.97) * mm});
            skLineSegment(sketch, "E869", {"start": v(-55.16, 67.97) * mm, "end": v(-54.92, 68.42) * mm});
            skLineSegment(sketch, "E870", {"start": v(-54.92, 68.42) * mm, "end": v(-54.68, 68.87) * mm});
            skLineSegment(sketch, "E871", {"start": v(-54.68, 68.87) * mm, "end": v(-54.42, 69.3) * mm});
            skLineSegment(sketch, "E872", {"start": v(-54.42, 69.3) * mm, "end": v(-54.15, 69.74) * mm});
            skLineSegment(sketch, "E873", {"start": v(-54.15, 69.74) * mm, "end": v(-53.87, 70.16) * mm});
            skLineSegment(sketch, "E874", {"start": v(-53.87, 70.16) * mm, "end": v(-53.58, 70.58) * mm});
            skLineSegment(sketch, "E875", {"start": v(-53.58, 70.58) * mm, "end": v(-53.28, 71) * mm});
            skLineSegment(sketch, "E876", {"start": v(-53.28, 71) * mm, "end": v(-52.96, 71.4) * mm});
            skLineSegment(sketch, "E877", {"start": v(-52.96, 71.4) * mm, "end": v(-52.64, 71.8) * mm});
            skLineSegment(sketch, "E878", {"start": v(-52.64, 71.8) * mm, "end": v(-52.3, 72.19) * mm});
            skLineSegment(sketch, "E879", {"start": v(-52.3, 72.19) * mm, "end": v(-51.96, 72.57) * mm});
            skLineSegment(sketch, "E880", {"start": v(-51.96, 72.57) * mm, "end": v(-51.6, 72.94) * mm});
            skLineSegment(sketch, "E881", {"start": v(-51.6, 72.94) * mm, "end": v(-51.31, 73.23) * mm});
            skLineSegment(sketch, "E882", {"start": v(-51.31, 73.23) * mm, "end": v(-51.01, 73.52) * mm});
            skLineSegment(sketch, "E883", {"start": v(-51.01, 73.52) * mm, "end": v(-50.7, 73.8) * mm});
            skLineSegment(sketch, "E884", {"start": v(-50.7, 73.8) * mm, "end": v(-50.4, 74.06) * mm});
            skLineSegment(sketch, "E885", {"start": v(-50.4, 74.06) * mm, "end": v(-50.07, 74.31) * mm});
            skLineSegment(sketch, "E886", {"start": v(-50.07, 74.31) * mm, "end": v(-49.75, 74.56) * mm});
            skLineSegment(sketch, "E887", {"start": v(-49.75, 74.56) * mm, "end": v(-49.42, 74.8) * mm});
            skLineSegment(sketch, "E888", {"start": v(-49.42, 74.8) * mm, "end": v(-49.08, 75.04) * mm});
            skLineSegment(sketch, "E889", {"start": v(-49.08, 75.04) * mm, "end": v(-48.74, 75.26) * mm});
            skLineSegment(sketch, "E890", {"start": v(-48.74, 75.26) * mm, "end": v(-48.4, 75.48) * mm});
            skLineSegment(sketch, "E891", {"start": v(-48.4, 75.48) * mm, "end": v(-48.04, 75.68) * mm});
            skLineSegment(sketch, "E892", {"start": v(-48.04, 75.68) * mm, "end": v(-47.68, 75.88) * mm});
            skLineSegment(sketch, "E893", {"start": v(-47.68, 75.88) * mm, "end": v(-47.32, 76.07) * mm});
            skLineSegment(sketch, "E894", {"start": v(-47.32, 76.07) * mm, "end": v(-46.95, 76.25) * mm});
            skLineSegment(sketch, "E895", {"start": v(-46.95, 76.25) * mm, "end": v(-46.58, 76.42) * mm});
            skLineSegment(sketch, "E896", {"start": v(-46.58, 76.42) * mm, "end": v(-46.2, 76.58) * mm});
            skLineSegment(sketch, "E897", {"start": v(-46.2, 76.58) * mm, "end": v(-45.83, 76.73) * mm});
            skLineSegment(sketch, "E898", {"start": v(-45.83, 76.73) * mm, "end": v(-45.45, 76.88) * mm});
            skLineSegment(sketch, "E899", {"start": v(-45.45, 76.88) * mm, "end": v(-45.06, 77) * mm});
            skLineSegment(sketch, "E900", {"start": v(-45.06, 77) * mm, "end": v(-44.67, 77.13) * mm});
            skLineSegment(sketch, "E901", {"start": v(-44.67, 77.13) * mm, "end": v(-44.28, 77.25) * mm});
            skLineSegment(sketch, "E902", {"start": v(-44.28, 77.25) * mm, "end": v(-43.89, 77.35) * mm});
            skLineSegment(sketch, "E903", {"start": v(-43.89, 77.35) * mm, "end": v(-43.5, 77.44) * mm});
            skLineSegment(sketch, "E904", {"start": v(-43.5, 77.44) * mm, "end": v(-43.09, 77.53) * mm});
            skLineSegment(sketch, "E905", {"start": v(-43.09, 77.53) * mm, "end": v(-42.69, 77.6) * mm});
            skLineSegment(sketch, "E906", {"start": v(-42.69, 77.6) * mm, "end": v(-42.28, 77.67) * mm});
            skLineSegment(sketch, "E907", {"start": v(-42.28, 77.67) * mm, "end": v(-41.88, 77.72) * mm});
            skLineSegment(sketch, "E908", {"start": v(-41.88, 77.72) * mm, "end": v(-41.47, 77.77) * mm});
            skLineSegment(sketch, "E909", {"start": v(-41.47, 77.77) * mm, "end": v(-41.06, 77.8) * mm});
            skLineSegment(sketch, "E910", {"start": v(-41.06, 77.8) * mm, "end": v(-40.65, 77.82) * mm});
            skLineSegment(sketch, "E911", {"start": v(-40.65, 77.82) * mm, "end": v(-40.23, 77.84) * mm});
            skLineSegment(sketch, "E912", {"start": v(-40.23, 77.84) * mm, "end": v(-39.82, 77.84) * mm});
            skLineSegment(sketch, "E913", {"start": v(-66.4, 77.28) * mm, "end": v(-66.4, 37.32) * mm});
            skLineSegment(sketch, "E914", {"start": v(-66.4, 37.32) * mm, "end": v(-83.95, 37.32) * mm});
            skLineSegment(sketch, "E915", {"start": v(-83.95, 37.32) * mm, "end": v(-84.45, 37.32) * mm});
            skLineSegment(sketch, "E916", {"start": v(-84.45, 37.32) * mm, "end": v(-84.94, 37.35) * mm});
            skLineSegment(sketch, "E917", {"start": v(-84.94, 37.35) * mm, "end": v(-85.43, 37.4) * mm});
            skLineSegment(sketch, "E918", {"start": v(-85.43, 37.4) * mm, "end": v(-85.9, 37.48) * mm});
            skLineSegment(sketch, "E919", {"start": v(-85.9, 37.48) * mm, "end": v(-86.39, 37.59) * mm});
            skLineSegment(sketch, "E920", {"start": v(-86.39, 37.59) * mm, "end": v(-86.86, 37.72) * mm});
            skLineSegment(sketch, "E921", {"start": v(-86.86, 37.72) * mm, "end": v(-87.32, 37.87) * mm});
            skLineSegment(sketch, "E922", {"start": v(-87.32, 37.87) * mm, "end": v(-87.78, 38.04) * mm});
            skLineSegment(sketch, "E923", {"start": v(-87.78, 38.04) * mm, "end": v(-88.22, 38.24) * mm});
            skLineSegment(sketch, "E924", {"start": v(-88.22, 38.24) * mm, "end": v(-88.66, 38.46) * mm});
            skLineSegment(sketch, "E925", {"start": v(-88.66, 38.46) * mm, "end": v(-89.08, 38.7) * mm});
            skLineSegment(sketch, "E926", {"start": v(-89.08, 38.7) * mm, "end": v(-89.5, 38.96) * mm});
            skLineSegment(sketch, "E927", {"start": v(-89.5, 38.96) * mm, "end": v(-89.89, 39.24) * mm});
            skLineSegment(sketch, "E928", {"start": v(-89.89, 39.24) * mm, "end": v(-90.27, 39.55) * mm});
            skLineSegment(sketch, "E929", {"start": v(-90.27, 39.55) * mm, "end": v(-90.64, 39.88) * mm});
            skLineSegment(sketch, "E930", {"start": v(-90.64, 39.88) * mm, "end": v(-91, 40.22) * mm});
            skLineSegment(sketch, "E931", {"start": v(-91, 40.22) * mm, "end": v(-91.34, 40.57) * mm});
            skLineSegment(sketch, "E932", {"start": v(-91.34, 40.57) * mm, "end": v(-91.66, 40.94) * mm});
            skLineSegment(sketch, "E933", {"start": v(-91.66, 40.94) * mm, "end": v(-91.96, 41.32) * mm});
            skLineSegment(sketch, "E934", {"start": v(-91.96, 41.32) * mm, "end": v(-92.24, 41.72) * mm});
            skLineSegment(sketch, "E935", {"start": v(-92.24, 41.72) * mm, "end": v(-92.5, 42.12) * mm});
            skLineSegment(sketch, "E936", {"start": v(-92.5, 42.12) * mm, "end": v(-92.74, 42.54) * mm});
            skLineSegment(sketch, "E937", {"start": v(-92.74, 42.54) * mm, "end": v(-92.96, 42.97) * mm});
            skLineSegment(sketch, "E938", {"start": v(-92.96, 42.97) * mm, "end": v(-93.16, 43.41) * mm});
            skLineSegment(sketch, "E939", {"start": v(-93.16, 43.41) * mm, "end": v(-93.33, 43.86) * mm});
            skLineSegment(sketch, "E940", {"start": v(-93.33, 43.86) * mm, "end": v(-93.48, 44.32) * mm});
            skLineSegment(sketch, "E941", {"start": v(-93.48, 44.32) * mm, "end": v(-93.61, 44.79) * mm});
            skLineSegment(sketch, "E942", {"start": v(-93.61, 44.79) * mm, "end": v(-93.72, 45.26) * mm});
            skLineSegment(sketch, "E943", {"start": v(-93.72, 45.26) * mm, "end": v(-93.8, 45.74) * mm});
            skLineSegment(sketch, "E944", {"start": v(-93.8, 45.74) * mm, "end": v(-93.87, 46.22) * mm});
            skLineSegment(sketch, "E945", {"start": v(-93.87, 46.22) * mm, "end": v(-93.9, 46.7) * mm});
            skLineSegment(sketch, "E946", {"start": v(-93.9, 46.7) * mm, "end": v(-93.91, 47.2) * mm});
            skLineSegment(sketch, "E947", {"start": v(-93.91, 47.2) * mm, "end": v(-93.92, 47.7) * mm});
            skLineSegment(sketch, "E948", {"start": v(-93.92, 47.7) * mm, "end": v(-93.9, 48.2) * mm});
            skLineSegment(sketch, "E949", {"start": v(-93.9, 48.2) * mm, "end": v(-93.84, 48.7) * mm});
            skLineSegment(sketch, "E950", {"start": v(-93.84, 48.7) * mm, "end": v(-93.77, 49.18) * mm});
            skLineSegment(sketch, "E951", {"start": v(-93.77, 49.18) * mm, "end": v(-93.67, 49.67) * mm});
            skLineSegment(sketch, "E952", {"start": v(-93.67, 49.67) * mm, "end": v(-93.55, 50.15) * mm});
            skLineSegment(sketch, "E953", {"start": v(-93.55, 50.15) * mm, "end": v(-93.4, 50.62) * mm});
            skLineSegment(sketch, "E954", {"start": v(-93.4, 50.62) * mm, "end": v(-93.24, 51.09) * mm});
            skLineSegment(sketch, "E955", {"start": v(-93.24, 51.09) * mm, "end": v(-93.04, 51.54) * mm});
            skLineSegment(sketch, "E956", {"start": v(-93.04, 51.54) * mm, "end": v(-92.83, 51.99) * mm});
            skLineSegment(sketch, "E957", {"start": v(-92.83, 51.99) * mm, "end": v(-92.59, 52.42) * mm});
            skLineSegment(sketch, "E958", {"start": v(-92.59, 52.42) * mm, "end": v(-92.33, 52.84) * mm});
            skLineSegment(sketch, "E959", {"start": v(-92.33, 52.84) * mm, "end": v(-92.05, 53.25) * mm});
            skLineSegment(sketch, "E960", {"start": v(-92.05, 53.25) * mm, "end": v(-91.74, 53.65) * mm});
            skLineSegment(sketch, "E961", {"start": v(-91.74, 53.65) * mm, "end": v(-91.42, 54.03) * mm});
            skLineSegment(sketch, "E962", {"start": v(-91.42, 54.03) * mm, "end": v(-91.08, 54.4) * mm});
            skLineSegment(sketch, "E963", {"start": v(-91.08, 54.4) * mm, "end": v(-90.72, 54.74) * mm});
            skLineSegment(sketch, "E964", {"start": v(-90.72, 54.74) * mm, "end": v(-90.34, 55.06) * mm});
            skLineSegment(sketch, "E965", {"start": v(-90.34, 55.06) * mm, "end": v(-89.95, 55.36) * mm});
            skLineSegment(sketch, "E966", {"start": v(-89.95, 55.36) * mm, "end": v(-89.54, 55.65) * mm});
            skLineSegment(sketch, "E967", {"start": v(-89.54, 55.65) * mm, "end": v(-89.13, 55.9) * mm});
            skLineSegment(sketch, "E968", {"start": v(-89.13, 55.9) * mm, "end": v(-88.7, 56.15) * mm});
            skLineSegment(sketch, "E969", {"start": v(-88.7, 56.15) * mm, "end": v(-88.26, 56.37) * mm});
            skLineSegment(sketch, "E970", {"start": v(-88.26, 56.37) * mm, "end": v(-87.8, 56.56) * mm});
            skLineSegment(sketch, "E971", {"start": v(-87.8, 56.56) * mm, "end": v(-87.35, 56.74) * mm});
            skLineSegment(sketch, "E972", {"start": v(-87.35, 56.74) * mm, "end": v(-86.88, 56.89) * mm});
            skLineSegment(sketch, "E973", {"start": v(-86.88, 56.89) * mm, "end": v(-86.4, 57.02) * mm});
            skLineSegment(sketch, "E974", {"start": v(-86.4, 57.02) * mm, "end": v(-85.92, 57.12) * mm});
            skLineSegment(sketch, "E975", {"start": v(-85.92, 57.12) * mm, "end": v(-85.44, 57.2) * mm});
            skLineSegment(sketch, "E976", {"start": v(-85.44, 57.2) * mm, "end": v(-84.95, 57.25) * mm});
            skLineSegment(sketch, "E977", {"start": v(-84.95, 57.25) * mm, "end": v(-84.45, 57.28) * mm});
            skLineSegment(sketch, "E978", {"start": v(-84.45, 57.28) * mm, "end": v(-83.95, 57.3) * mm});
            skLineSegment(sketch, "E979", {"start": v(-83.95, 57.3) * mm, "end": v(-66.4, 57.3) * mm});
            skLineSegment(sketch, "E980", {"start": v(-83.95, 57.3) * mm, "end": v(-84.36, 57.3) * mm});
            skLineSegment(sketch, "E981", {"start": v(-84.36, 57.3) * mm, "end": v(-84.77, 57.31) * mm});
            skLineSegment(sketch, "E982", {"start": v(-84.77, 57.31) * mm, "end": v(-85.17, 57.36) * mm});
            skLineSegment(sketch, "E983", {"start": v(-85.17, 57.36) * mm, "end": v(-85.57, 57.42) * mm});
            skLineSegment(sketch, "E984", {"start": v(-85.57, 57.42) * mm, "end": v(-85.97, 57.5) * mm});
            skLineSegment(sketch, "E985", {"start": v(-85.97, 57.5) * mm, "end": v(-86.36, 57.61) * mm});
            skLineSegment(sketch, "E986", {"start": v(-86.36, 57.61) * mm, "end": v(-86.75, 57.73) * mm});
            skLineSegment(sketch, "E987", {"start": v(-86.75, 57.73) * mm, "end": v(-87.12, 57.88) * mm});
            skLineSegment(sketch, "E988", {"start": v(-87.12, 57.88) * mm, "end": v(-87.5, 58.04) * mm});
            skLineSegment(sketch, "E989", {"start": v(-87.5, 58.04) * mm, "end": v(-87.86, 58.22) * mm});
            skLineSegment(sketch, "E990", {"start": v(-87.86, 58.22) * mm, "end": v(-88.2, 58.42) * mm});
            skLineSegment(sketch, "E991", {"start": v(-88.2, 58.42) * mm, "end": v(-88.55, 58.63) * mm});
            skLineSegment(sketch, "E992", {"start": v(-88.55, 58.63) * mm, "end": v(-88.88, 58.87) * mm});
            skLineSegment(sketch, "E993", {"start": v(-88.88, 58.87) * mm, "end": v(-89.2, 59.12) * mm});
            skLineSegment(sketch, "E994", {"start": v(-89.2, 59.12) * mm, "end": v(-89.5, 59.39) * mm});
            skLineSegment(sketch, "E995", {"start": v(-89.5, 59.39) * mm, "end": v(-89.8, 59.67) * mm});
            skLineSegment(sketch, "E996", {"start": v(-89.8, 59.67) * mm, "end": v(-90.14, 60.17) * mm});
            skLineSegment(sketch, "E997", {"start": v(-90.14, 60.17) * mm, "end": v(-90.46, 60.69) * mm});
            skLineSegment(sketch, "E998", {"start": v(-90.46, 60.69) * mm, "end": v(-90.76, 61.21) * mm});
            skLineSegment(sketch, "E999", {"start": v(-90.76, 61.21) * mm, "end": v(-91.02, 61.75) * mm});
            skLineSegment(sketch, "E1000", {"start": v(-91.02, 61.75) * mm, "end": v(-91.27, 62.3) * mm});
            skLineSegment(sketch, "E1001", {"start": v(-91.27, 62.3) * mm, "end": v(-91.49, 62.85) * mm});
            skLineSegment(sketch, "E1002", {"start": v(-91.49, 62.85) * mm, "end": v(-91.68, 63.42) * mm});
            skLineSegment(sketch, "E1003", {"start": v(-91.68, 63.42) * mm, "end": v(-91.85, 64) * mm});
            skLineSegment(sketch, "E1004", {"start": v(-91.85, 64) * mm, "end": v(-92, 64.58) * mm});
            skLineSegment(sketch, "E1005", {"start": v(-92, 64.58) * mm, "end": v(-92.11, 65.16) * mm});
            skLineSegment(sketch, "E1006", {"start": v(-92.11, 65.16) * mm, "end": v(-92.2, 65.76) * mm});
            skLineSegment(sketch, "E1007", {"start": v(-92.2, 65.76) * mm, "end": v(-92.27, 66.35) * mm});
            skLineSegment(sketch, "E1008", {"start": v(-92.27, 66.35) * mm, "end": v(-92.3, 66.95) * mm});
            skLineSegment(sketch, "E1009", {"start": v(-92.3, 66.95) * mm, "end": v(-92.32, 67.55) * mm});
            skLineSegment(sketch, "E1010", {"start": v(-92.32, 67.55) * mm, "end": v(-92.3, 68.16) * mm});
            skLineSegment(sketch, "E1011", {"start": v(-92.3, 68.16) * mm, "end": v(-92.26, 68.76) * mm});
            skLineSegment(sketch, "E1012", {"start": v(-92.26, 68.76) * mm, "end": v(-92.26, 69.3) * mm});
            skLineSegment(sketch, "E1013", {"start": v(-92.26, 69.3) * mm, "end": v(-92.26, 69.84) * mm});
            skLineSegment(sketch, "E1014", {"start": v(-92.26, 69.84) * mm, "end": v(-92.27, 70.37) * mm});
            skLineSegment(sketch, "E1015", {"start": v(-92.27, 70.37) * mm, "end": v(-92.3, 70.91) * mm});
            skLineSegment(sketch, "E1016", {"start": v(-92.3, 70.91) * mm, "end": v(-92.32, 71.45) * mm});
            skLineSegment(sketch, "E1017", {"start": v(-92.32, 71.45) * mm, "end": v(-92.36, 71.99) * mm});
            skLineSegment(sketch, "E1018", {"start": v(-92.36, 71.99) * mm, "end": v(-92.41, 72.52) * mm});
            skLineSegment(sketch, "E1019", {"start": v(-92.41, 72.52) * mm, "end": v(-92.47, 73.06) * mm});
            skLineSegment(sketch, "E1020", {"start": v(-92.47, 73.06) * mm, "end": v(-92.54, 73.6) * mm});
            skLineSegment(sketch, "E1021", {"start": v(-92.54, 73.6) * mm, "end": v(-92.62, 74.12) * mm});
            skLineSegment(sketch, "E1022", {"start": v(-92.62, 74.12) * mm, "end": v(-92.71, 74.65) * mm});
            skLineSegment(sketch, "E1023", {"start": v(-92.71, 74.65) * mm, "end": v(-92.8, 75.18) * mm});
            skLineSegment(sketch, "E1024", {"start": v(-92.8, 75.18) * mm, "end": v(-92.92, 75.71) * mm});
            skLineSegment(sketch, "E1025", {"start": v(-92.92, 75.71) * mm, "end": v(-93.03, 76.24) * mm});
            skLineSegment(sketch, "E1026", {"start": v(-93.03, 76.24) * mm, "end": v(-93.16, 76.76) * mm});
            skLineSegment(sketch, "E1027", {"start": v(-93.16, 76.76) * mm, "end": v(-93.3, 77.28) * mm});
            skLineSegment(sketch, "E1028", {"start": v(-131.3, 45.92) * mm, "end": v(-131.46, 45.4) * mm});
            skLineSegment(sketch, "E1029", {"start": v(-131.46, 45.4) * mm, "end": v(-131.64, 44.9) * mm});
            skLineSegment(sketch, "E1030", {"start": v(-131.64, 44.9) * mm, "end": v(-131.85, 44.4) * mm});
            skLineSegment(sketch, "E1031", {"start": v(-131.85, 44.4) * mm, "end": v(-132.07, 43.9) * mm});
            skLineSegment(sketch, "E1032", {"start": v(-132.07, 43.9) * mm, "end": v(-132.3, 43.43) * mm});
            skLineSegment(sketch, "E1033", {"start": v(-132.3, 43.43) * mm, "end": v(-132.57, 42.97) * mm});
            skLineSegment(sketch, "E1034", {"start": v(-132.57, 42.97) * mm, "end": v(-132.84, 42.52) * mm});
            skLineSegment(sketch, "E1035", {"start": v(-132.84, 42.52) * mm, "end": v(-133.14, 42.08) * mm});
            skLineSegment(sketch, "E1036", {"start": v(-133.14, 42.08) * mm, "end": v(-133.45, 41.65) * mm});
            skLineSegment(sketch, "E1037", {"start": v(-133.45, 41.65) * mm, "end": v(-133.77, 41.24) * mm});
            skLineSegment(sketch, "E1038", {"start": v(-133.77, 41.24) * mm, "end": v(-134.11, 40.85) * mm});
            skLineSegment(sketch, "E1039", {"start": v(-134.11, 40.85) * mm, "end": v(-134.47, 40.46) * mm});
            skLineSegment(sketch, "E1040", {"start": v(-134.47, 40.46) * mm, "end": v(-134.84, 40.1) * mm});
            skLineSegment(sketch, "E1041", {"start": v(-134.84, 40.1) * mm, "end": v(-135.23, 39.75) * mm});
            skLineSegment(sketch, "E1042", {"start": v(-135.23, 39.75) * mm, "end": v(-135.63, 39.4) * mm});
            skLineSegment(sketch, "E1043", {"start": v(-135.63, 39.4) * mm, "end": v(-136.04, 39.09) * mm});
            skLineSegment(sketch, "E1044", {"start": v(-136.04, 39.09) * mm, "end": v(-136.46, 38.79) * mm});
            skLineSegment(sketch, "E1045", {"start": v(-136.46, 38.79) * mm, "end": v(-136.9, 38.5) * mm});
            skLineSegment(sketch, "E1046", {"start": v(-136.9, 38.5) * mm, "end": v(-137.34, 38.23) * mm});
            skLineSegment(sketch, "E1047", {"start": v(-137.34, 38.23) * mm, "end": v(-137.8, 37.98) * mm});
            skLineSegment(sketch, "E1048", {"start": v(-137.8, 37.98) * mm, "end": v(-138.27, 37.74) * mm});
            skLineSegment(sketch, "E1049", {"start": v(-138.27, 37.74) * mm, "end": v(-138.75, 37.53) * mm});
            skLineSegment(sketch, "E1050", {"start": v(-138.75, 37.53) * mm, "end": v(-139.23, 37.33) * mm});
            skLineSegment(sketch, "E1051", {"start": v(-139.23, 37.33) * mm, "end": v(-139.73, 37.16) * mm});
            skLineSegment(sketch, "E1052", {"start": v(-139.73, 37.16) * mm, "end": v(-140.23, 37) * mm});
            skLineSegment(sketch, "E1053", {"start": v(-140.23, 37) * mm, "end": v(-140.74, 36.86) * mm});
            skLineSegment(sketch, "E1054", {"start": v(-140.74, 36.86) * mm, "end": v(-141.26, 36.74) * mm});
            skLineSegment(sketch, "E1055", {"start": v(-141.26, 36.74) * mm, "end": v(-141.78, 36.65) * mm});
            skLineSegment(sketch, "E1056", {"start": v(-141.78, 36.65) * mm, "end": v(-142.31, 36.57) * mm});
            skLineSegment(sketch, "E1057", {"start": v(-142.31, 36.57) * mm, "end": v(-142.85, 36.52) * mm});
            skLineSegment(sketch, "E1058", {"start": v(-142.85, 36.52) * mm, "end": v(-143.4, 36.49) * mm});
            skLineSegment(sketch, "E1059", {"start": v(-143.4, 36.49) * mm, "end": v(-143.94, 36.48) * mm});
            skLineSegment(sketch, "E1060", {"start": v(-143.94, 36.48) * mm, "end": v(-144.58, 36.5) * mm});
            skLineSegment(sketch, "E1061", {"start": v(-144.58, 36.5) * mm, "end": v(-145.21, 36.53) * mm});
            skLineSegment(sketch, "E1062", {"start": v(-145.21, 36.53) * mm, "end": v(-145.83, 36.59) * mm});
            skLineSegment(sketch, "E1063", {"start": v(-145.83, 36.59) * mm, "end": v(-146.45, 36.67) * mm});
            skLineSegment(sketch, "E1064", {"start": v(-146.45, 36.67) * mm, "end": v(-147.05, 36.77) * mm});
            skLineSegment(sketch, "E1065", {"start": v(-147.05, 36.77) * mm, "end": v(-147.64, 36.9) * mm});
            skLineSegment(sketch, "E1066", {"start": v(-147.64, 36.9) * mm, "end": v(-148.22, 37.04) * mm});
            skLineSegment(sketch, "E1067", {"start": v(-148.22, 37.04) * mm, "end": v(-148.78, 37.2) * mm});
            skLineSegment(sketch, "E1068", {"start": v(-148.78, 37.2) * mm, "end": v(-149.34, 37.4) * mm});
            skLineSegment(sketch, "E1069", {"start": v(-149.34, 37.4) * mm, "end": v(-149.87, 37.6) * mm});
            skLineSegment(sketch, "E1070", {"start": v(-149.87, 37.6) * mm, "end": v(-150.4, 37.82) * mm});
            skLineSegment(sketch, "E1071", {"start": v(-150.4, 37.82) * mm, "end": v(-150.9, 38.06) * mm});
            skLineSegment(sketch, "E1072", {"start": v(-150.9, 38.06) * mm, "end": v(-151.39, 38.32) * mm});
            skLineSegment(sketch, "E1073", {"start": v(-151.39, 38.32) * mm, "end": v(-151.86, 38.6) * mm});
            skLineSegment(sketch, "E1074", {"start": v(-151.86, 38.6) * mm, "end": v(-152.31, 38.9) * mm});
            skLineSegment(sketch, "E1075", {"start": v(-152.31, 38.9) * mm, "end": v(-152.74, 39.2) * mm});
            skLineSegment(sketch, "E1076", {"start": v(-152.74, 39.2) * mm, "end": v(-153.15, 39.52) * mm});
            skLineSegment(sketch, "E1077", {"start": v(-153.15, 39.52) * mm, "end": v(-153.55, 39.86) * mm});
            skLineSegment(sketch, "E1078", {"start": v(-153.55, 39.86) * mm, "end": v(-153.92, 40.2) * mm});
            skLineSegment(sketch, "E1079", {"start": v(-153.92, 40.2) * mm, "end": v(-154.26, 40.57) * mm});
            skLineSegment(sketch, "E1080", {"start": v(-154.26, 40.57) * mm, "end": v(-154.59, 40.95) * mm});
            skLineSegment(sketch, "E1081", {"start": v(-154.59, 40.95) * mm, "end": v(-154.89, 41.34) * mm});
            skLineSegment(sketch, "E1082", {"start": v(-154.89, 41.34) * mm, "end": v(-155.16, 41.74) * mm});
            skLineSegment(sketch, "E1083", {"start": v(-155.16, 41.74) * mm, "end": v(-155.41, 42.15) * mm});
            skLineSegment(sketch, "E1084", {"start": v(-155.41, 42.15) * mm, "end": v(-155.63, 42.57) * mm});
            skLineSegment(sketch, "E1085", {"start": v(-155.63, 42.57) * mm, "end": v(-155.83, 43) * mm});
            skLineSegment(sketch, "E1086", {"start": v(-155.83, 43) * mm, "end": v(-156, 43.44) * mm});
            skLineSegment(sketch, "E1087", {"start": v(-156, 43.44) * mm, "end": v(-156.07, 43.66) * mm});
            skLineSegment(sketch, "E1088", {"start": v(-156.07, 43.66) * mm, "end": v(-156.14, 43.89) * mm});
            skLineSegment(sketch, "E1089", {"start": v(-156.14, 43.89) * mm, "end": v(-156.2, 44.12) * mm});
            skLineSegment(sketch, "E1090", {"start": v(-156.2, 44.12) * mm, "end": v(-156.25, 44.35) * mm});
            skLineSegment(sketch, "E1091", {"start": v(-156.25, 44.35) * mm, "end": v(-156.3, 44.58) * mm});
            skLineSegment(sketch, "E1092", {"start": v(-156.3, 44.58) * mm, "end": v(-156.33, 44.81) * mm});
            skLineSegment(sketch, "E1093", {"start": v(-156.33, 44.81) * mm, "end": v(-156.35, 45.05) * mm});
            skLineSegment(sketch, "E1094", {"start": v(-156.35, 45.05) * mm, "end": v(-156.37, 45.28) * mm});
            skLineSegment(sketch, "E1095", {"start": v(-156.37, 45.28) * mm, "end": v(-156.39, 45.52) * mm});
            skLineSegment(sketch, "E1096", {"start": v(-156.39, 45.52) * mm, "end": v(-156.4, 45.76) * mm});
            skLineSegment(sketch, "E1097", {"start": v(-156.4, 45.76) * mm, "end": v(-156.39, 46.02) * mm});
            skLineSegment(sketch, "E1098", {"start": v(-156.39, 46.02) * mm, "end": v(-156.37, 46.27) * mm});
            skLineSegment(sketch, "E1099", {"start": v(-156.37, 46.27) * mm, "end": v(-156.35, 46.52) * mm});
            skLineSegment(sketch, "E1100", {"start": v(-156.35, 46.52) * mm, "end": v(-156.32, 46.77) * mm});
            skLineSegment(sketch, "E1101", {"start": v(-156.32, 46.77) * mm, "end": v(-156.28, 47.02) * mm});
            skLineSegment(sketch, "E1102", {"start": v(-156.28, 47.02) * mm, "end": v(-156.23, 47.27) * mm});
            skLineSegment(sketch, "E1103", {"start": v(-156.23, 47.27) * mm, "end": v(-156.18, 47.52) * mm});
            skLineSegment(sketch, "E1104", {"start": v(-156.18, 47.52) * mm, "end": v(-156.11, 47.76) * mm});
            skLineSegment(sketch, "E1105", {"start": v(-156.11, 47.76) * mm, "end": v(-156.04, 48) * mm});
            skLineSegment(sketch, "E1106", {"start": v(-156.04, 48) * mm, "end": v(-155.96, 48.24) * mm});
            skLineSegment(sketch, "E1107", {"start": v(-155.96, 48.24) * mm, "end": v(-155.88, 48.48) * mm});
            skLineSegment(sketch, "E1108", {"start": v(-155.88, 48.48) * mm, "end": v(-155.78, 48.7) * mm});
            skLineSegment(sketch, "E1109", {"start": v(-155.78, 48.7) * mm, "end": v(-155.68, 48.94) * mm});
            skLineSegment(sketch, "E1110", {"start": v(-155.68, 48.94) * mm, "end": v(-155.57, 49.17) * mm});
            skLineSegment(sketch, "E1111", {"start": v(-155.57, 49.17) * mm, "end": v(-155.45, 49.4) * mm});
            skLineSegment(sketch, "E1112", {"start": v(-155.45, 49.4) * mm, "end": v(-155.33, 49.62) * mm});
            skLineSegment(sketch, "E1113", {"start": v(-155.33, 49.62) * mm, "end": v(-155.05, 50.06) * mm});
            skLineSegment(sketch, "E1114", {"start": v(-155.05, 50.06) * mm, "end": v(-154.76, 50.49) * mm});
            skLineSegment(sketch, "E1115", {"start": v(-154.76, 50.49) * mm, "end": v(-154.43, 50.9) * mm});
            skLineSegment(sketch, "E1116", {"start": v(-154.43, 50.9) * mm, "end": v(-154.08, 51.3) * mm});
            skLineSegment(sketch, "E1117", {"start": v(-154.08, 51.3) * mm, "end": v(-153.7, 51.7) * mm});
            skLineSegment(sketch, "E1118", {"start": v(-153.7, 51.7) * mm, "end": v(-153.3, 52.07) * mm});
            skLineSegment(sketch, "E1119", {"start": v(-153.3, 52.07) * mm, "end": v(-152.87, 52.43) * mm});
            skLineSegment(sketch, "E1120", {"start": v(-152.87, 52.43) * mm, "end": v(-152.42, 52.77) * mm});
            skLineSegment(sketch, "E1121", {"start": v(-152.42, 52.77) * mm, "end": v(-151.95, 53.1) * mm});
            skLineSegment(sketch, "E1122", {"start": v(-151.95, 53.1) * mm, "end": v(-151.46, 53.41) * mm});
            skLineSegment(sketch, "E1123", {"start": v(-151.46, 53.41) * mm, "end": v(-150.95, 53.7) * mm});
            skLineSegment(sketch, "E1124", {"start": v(-150.95, 53.7) * mm, "end": v(-150.42, 53.99) * mm});
            skLineSegment(sketch, "E1125", {"start": v(-150.42, 53.99) * mm, "end": v(-149.87, 54.24) * mm});
            skLineSegment(sketch, "E1126", {"start": v(-149.87, 54.24) * mm, "end": v(-149.3, 54.48) * mm});
            skLineSegment(sketch, "E1127", {"start": v(-149.3, 54.48) * mm, "end": v(-148.72, 54.7) * mm});
            skLineSegment(sketch, "E1128", {"start": v(-148.72, 54.7) * mm, "end": v(-148.12, 54.9) * mm});
            skLineSegment(sketch, "E1129", {"start": v(-148.12, 54.9) * mm, "end": v(-147.5, 55.08) * mm});
            skLineSegment(sketch, "E1130", {"start": v(-147.5, 55.08) * mm, "end": v(-146.87, 55.23) * mm});
            skLineSegment(sketch, "E1131", {"start": v(-146.87, 55.23) * mm, "end": v(-146.23, 55.37) * mm});
            skLineSegment(sketch, "E1132", {"start": v(-146.23, 55.37) * mm, "end": v(-145.57, 55.48) * mm});
            skLineSegment(sketch, "E1133", {"start": v(-145.57, 55.48) * mm, "end": v(-144.9, 55.57) * mm});
            skLineSegment(sketch, "E1134", {"start": v(-144.9, 55.57) * mm, "end": v(-144.23, 55.63) * mm});
            skLineSegment(sketch, "E1135", {"start": v(-144.23, 55.63) * mm, "end": v(-143.54, 55.67) * mm});
            skLineSegment(sketch, "E1136", {"start": v(-143.54, 55.67) * mm, "end": v(-142.84, 55.68) * mm});
            skLineSegment(sketch, "E1137", {"start": v(-142.84, 55.68) * mm, "end": v(-143.62, 55.7) * mm});
            skLineSegment(sketch, "E1138", {"start": v(-143.62, 55.7) * mm, "end": v(-144.38, 55.73) * mm});
            skLineSegment(sketch, "E1139", {"start": v(-144.38, 55.73) * mm, "end": v(-145.13, 55.8) * mm});
            skLineSegment(sketch, "E1140", {"start": v(-145.13, 55.8) * mm, "end": v(-145.87, 55.9) * mm});
            skLineSegment(sketch, "E1141", {"start": v(-145.87, 55.9) * mm, "end": v(-146.6, 56.01) * mm});
            skLineSegment(sketch, "E1142", {"start": v(-146.6, 56.01) * mm, "end": v(-147.3, 56.15) * mm});
            skLineSegment(sketch, "E1143", {"start": v(-147.3, 56.15) * mm, "end": v(-148, 56.32) * mm});
            skLineSegment(sketch, "E1144", {"start": v(-148, 56.32) * mm, "end": v(-148.69, 56.5) * mm});
            skLineSegment(sketch, "E1145", {"start": v(-148.69, 56.5) * mm, "end": v(-149.35, 56.72) * mm});
            skLineSegment(sketch, "E1146", {"start": v(-149.35, 56.72) * mm, "end": v(-150, 56.95) * mm});
            skLineSegment(sketch, "E1147", {"start": v(-150, 56.95) * mm, "end": v(-150.63, 57.2) * mm});
            skLineSegment(sketch, "E1148", {"start": v(-150.63, 57.2) * mm, "end": v(-151.24, 57.48) * mm});
            skLineSegment(sketch, "E1149", {"start": v(-151.24, 57.48) * mm, "end": v(-151.83, 57.78) * mm});
            skLineSegment(sketch, "E1150", {"start": v(-151.83, 57.78) * mm, "end": v(-152.4, 58.1) * mm});
            skLineSegment(sketch, "E1151", {"start": v(-152.4, 58.1) * mm, "end": v(-152.94, 58.42) * mm});
            skLineSegment(sketch, "E1152", {"start": v(-152.94, 58.42) * mm, "end": v(-153.46, 58.77) * mm});
            skLineSegment(sketch, "E1153", {"start": v(-153.46, 58.77) * mm, "end": v(-153.96, 59.14) * mm});
            skLineSegment(sketch, "E1154", {"start": v(-153.96, 59.14) * mm, "end": v(-154.43, 59.52) * mm});
            skLineSegment(sketch, "E1155", {"start": v(-154.43, 59.52) * mm, "end": v(-154.87, 59.92) * mm});
            skLineSegment(sketch, "E1156", {"start": v(-154.87, 59.92) * mm, "end": v(-155.3, 60.34) * mm});
            skLineSegment(sketch, "E1157", {"start": v(-155.3, 60.34) * mm, "end": v(-155.5, 60.55) * mm});
            skLineSegment(sketch, "E1158", {"start": v(-155.5, 60.55) * mm, "end": v(-155.68, 60.76) * mm});
            skLineSegment(sketch, "E1159", {"start": v(-155.68, 60.76) * mm, "end": v(-155.87, 60.98) * mm});
            skLineSegment(sketch, "E1160", {"start": v(-155.87, 60.98) * mm, "end": v(-156.04, 61.2) * mm});
            skLineSegment(sketch, "E1161", {"start": v(-156.04, 61.2) * mm, "end": v(-156.21, 61.43) * mm});
            skLineSegment(sketch, "E1162", {"start": v(-156.21, 61.43) * mm, "end": v(-156.38, 61.66) * mm});
            skLineSegment(sketch, "E1163", {"start": v(-156.38, 61.66) * mm, "end": v(-156.53, 61.9) * mm});
            skLineSegment(sketch, "E1164", {"start": v(-156.53, 61.9) * mm, "end": v(-156.68, 62.13) * mm});
            skLineSegment(sketch, "E1165", {"start": v(-156.68, 62.13) * mm, "end": v(-156.82, 62.37) * mm});
            skLineSegment(sketch, "E1166", {"start": v(-156.82, 62.37) * mm, "end": v(-156.95, 62.6) * mm});
            skLineSegment(sketch, "E1167", {"start": v(-156.95, 62.6) * mm, "end": v(-157.07, 62.85) * mm});
            skLineSegment(sketch, "E1168", {"start": v(-157.07, 62.85) * mm, "end": v(-157.18, 63.1) * mm});
            skLineSegment(sketch, "E1169", {"start": v(-157.18, 63.1) * mm, "end": v(-157.29, 63.35) * mm});
            skLineSegment(sketch, "E1170", {"start": v(-157.29, 63.35) * mm, "end": v(-157.38, 63.6) * mm});
            skLineSegment(sketch, "E1171", {"start": v(-157.38, 63.6) * mm, "end": v(-157.47, 63.85) * mm});
            skLineSegment(sketch, "E1172", {"start": v(-157.47, 63.85) * mm, "end": v(-157.55, 64.11) * mm});
            skLineSegment(sketch, "E1173", {"start": v(-157.55, 64.11) * mm, "end": v(-157.62, 64.37) * mm});
            skLineSegment(sketch, "E1174", {"start": v(-157.62, 64.37) * mm, "end": v(-157.68, 64.63) * mm});
            skLineSegment(sketch, "E1175", {"start": v(-157.68, 64.63) * mm, "end": v(-157.74, 64.9) * mm});
            skLineSegment(sketch, "E1176", {"start": v(-157.74, 64.9) * mm, "end": v(-157.78, 65.16) * mm});
            skLineSegment(sketch, "E1177", {"start": v(-157.78, 65.16) * mm, "end": v(-157.81, 65.43) * mm});
            skLineSegment(sketch, "E1178", {"start": v(-157.81, 65.43) * mm, "end": v(-157.84, 65.7) * mm});
            skLineSegment(sketch, "E1179", {"start": v(-157.84, 65.7) * mm, "end": v(-157.85, 65.97) * mm});
            skLineSegment(sketch, "E1180", {"start": v(-157.85, 65.97) * mm, "end": v(-157.86, 66.24) * mm});
            skLineSegment(sketch, "E1181", {"start": v(-157.86, 66.24) * mm, "end": v(-157.85, 66.54) * mm});
            skLineSegment(sketch, "E1182", {"start": v(-157.85, 66.54) * mm, "end": v(-157.84, 66.85) * mm});
            skLineSegment(sketch, "E1183", {"start": v(-157.84, 66.85) * mm, "end": v(-157.82, 67.15) * mm});
            skLineSegment(sketch, "E1184", {"start": v(-157.82, 67.15) * mm, "end": v(-157.8, 67.45) * mm});
            skLineSegment(sketch, "E1185", {"start": v(-157.8, 67.45) * mm, "end": v(-157.76, 67.75) * mm});
            skLineSegment(sketch, "E1186", {"start": v(-157.76, 67.75) * mm, "end": v(-157.72, 68.04) * mm});
            skLineSegment(sketch, "E1187", {"start": v(-157.72, 68.04) * mm, "end": v(-157.62, 68.62) * mm});
            skLineSegment(sketch, "E1188", {"start": v(-157.62, 68.62) * mm, "end": v(-157.48, 69.2) * mm});
            skLineSegment(sketch, "E1189", {"start": v(-157.48, 69.2) * mm, "end": v(-157.32, 69.76) * mm});
            skLineSegment(sketch, "E1190", {"start": v(-157.32, 69.76) * mm, "end": v(-157.14, 70.3) * mm});
            skLineSegment(sketch, "E1191", {"start": v(-157.14, 70.3) * mm, "end": v(-156.93, 70.85) * mm});
            skLineSegment(sketch, "E1192", {"start": v(-156.93, 70.85) * mm, "end": v(-156.69, 71.37) * mm});
            skLineSegment(sketch, "E1193", {"start": v(-156.69, 71.37) * mm, "end": v(-156.43, 71.88) * mm});
            skLineSegment(sketch, "E1194", {"start": v(-156.43, 71.88) * mm, "end": v(-156.14, 72.38) * mm});
            skLineSegment(sketch, "E1195", {"start": v(-156.14, 72.38) * mm, "end": v(-155.83, 72.86) * mm});
            skLineSegment(sketch, "E1196", {"start": v(-155.83, 72.86) * mm, "end": v(-155.5, 73.32) * mm});
            skLineSegment(sketch, "E1197", {"start": v(-155.5, 73.32) * mm, "end": v(-155.15, 73.77) * mm});
            skLineSegment(sketch, "E1198", {"start": v(-155.15, 73.77) * mm, "end": v(-154.78, 74.2) * mm});
            skLineSegment(sketch, "E1199", {"start": v(-154.78, 74.2) * mm, "end": v(-154.39, 74.6) * mm});
            skLineSegment(sketch, "E1200", {"start": v(-154.39, 74.6) * mm, "end": v(-153.98, 75) * mm});
            skLineSegment(sketch, "E1201", {"start": v(-153.98, 75) * mm, "end": v(-153.55, 75.37) * mm});
            skLineSegment(sketch, "E1202", {"start": v(-153.55, 75.37) * mm, "end": v(-153.1, 75.73) * mm});
            skLineSegment(sketch, "E1203", {"start": v(-153.1, 75.73) * mm, "end": v(-152.63, 76.06) * mm});
            skLineSegment(sketch, "E1204", {"start": v(-152.63, 76.06) * mm, "end": v(-152.15, 76.36) * mm});
            skLineSegment(sketch, "E1205", {"start": v(-152.15, 76.36) * mm, "end": v(-151.66, 76.65) * mm});
            skLineSegment(sketch, "E1206", {"start": v(-151.66, 76.65) * mm, "end": v(-151.15, 76.91) * mm});
            skLineSegment(sketch, "E1207", {"start": v(-151.15, 76.91) * mm, "end": v(-150.62, 77.15) * mm});
            skLineSegment(sketch, "E1208", {"start": v(-150.62, 77.15) * mm, "end": v(-150.09, 77.36) * mm});
            skLineSegment(sketch, "E1209", {"start": v(-150.09, 77.36) * mm, "end": v(-149.54, 77.55) * mm});
            skLineSegment(sketch, "E1210", {"start": v(-149.54, 77.55) * mm, "end": v(-148.97, 77.7) * mm});
            skLineSegment(sketch, "E1211", {"start": v(-148.97, 77.7) * mm, "end": v(-148.4, 77.84) * mm});
            skLineSegment(sketch, "E1212", {"start": v(-148.4, 77.84) * mm, "end": v(-147.82, 77.94) * mm});
            skLineSegment(sketch, "E1213", {"start": v(-147.82, 77.94) * mm, "end": v(-147.52, 77.98) * mm});
            skLineSegment(sketch, "E1214", {"start": v(-147.52, 77.98) * mm, "end": v(-147.23, 78.02) * mm});
            skLineSegment(sketch, "E1215", {"start": v(-147.23, 78.02) * mm, "end": v(-146.93, 78.04) * mm});
            skLineSegment(sketch, "E1216", {"start": v(-146.93, 78.04) * mm, "end": v(-146.63, 78.06) * mm});
            skLineSegment(sketch, "E1217", {"start": v(-146.63, 78.06) * mm, "end": v(-146.32, 78.08) * mm});
            skLineSegment(sketch, "E1218", {"start": v(-146.32, 78.08) * mm, "end": v(-146.02, 78.08) * mm});
            skLineSegment(sketch, "E1219", {"start": v(-146.02, 78.08) * mm, "end": v(-144.58, 78.08) * mm});
            skLineSegment(sketch, "E1220", {"start": v(-144.58, 78.08) * mm, "end": v(-143.92, 78.07) * mm});
            skLineSegment(sketch, "E1221", {"start": v(-143.92, 78.07) * mm, "end": v(-143.26, 78.03) * mm});
            skLineSegment(sketch, "E1222", {"start": v(-143.26, 78.03) * mm, "end": v(-142.61, 77.96) * mm});
            skLineSegment(sketch, "E1223", {"start": v(-142.61, 77.96) * mm, "end": v(-141.97, 77.87) * mm});
            skLineSegment(sketch, "E1224", {"start": v(-141.97, 77.87) * mm, "end": v(-141.33, 77.75) * mm});
            skLineSegment(sketch, "E1225", {"start": v(-141.33, 77.75) * mm, "end": v(-140.7, 77.6) * mm});
            skLineSegment(sketch, "E1226", {"start": v(-140.7, 77.6) * mm, "end": v(-140.08, 77.44) * mm});
            skLineSegment(sketch, "E1227", {"start": v(-140.08, 77.44) * mm, "end": v(-139.47, 77.25) * mm});
            skLineSegment(sketch, "E1228", {"start": v(-139.47, 77.25) * mm, "end": v(-138.87, 77.04) * mm});
            skLineSegment(sketch, "E1229", {"start": v(-138.87, 77.04) * mm, "end": v(-138.28, 76.8) * mm});
            skLineSegment(sketch, "E1230", {"start": v(-138.28, 76.8) * mm, "end": v(-137.7, 76.54) * mm});
            skLineSegment(sketch, "E1231", {"start": v(-137.7, 76.54) * mm, "end": v(-137.12, 76.26) * mm});
            skLineSegment(sketch, "E1232", {"start": v(-137.12, 76.26) * mm, "end": v(-136.56, 75.96) * mm});
            skLineSegment(sketch, "E1233", {"start": v(-136.56, 75.96) * mm, "end": v(-136.02, 75.64) * mm});
            skLineSegment(sketch, "E1234", {"start": v(-136.02, 75.64) * mm, "end": v(-135.49, 75.3) * mm});
            skLineSegment(sketch, "E1235", {"start": v(-135.49, 75.3) * mm, "end": v(-134.97, 74.93) * mm});
            skLineSegment(sketch, "E1236", {"start": v(-134.97, 74.93) * mm, "end": v(-134.46, 74.55) * mm});
            skLineSegment(sketch, "E1237", {"start": v(-134.46, 74.55) * mm, "end": v(-133.97, 74.14) * mm});
            skLineSegment(sketch, "E1238", {"start": v(-133.97, 74.14) * mm, "end": v(-133.5, 73.72) * mm});
            skLineSegment(sketch, "E1239", {"start": v(-133.5, 73.72) * mm, "end": v(-133.04, 73.28) * mm});
            skLineSegment(sketch, "E1240", {"start": v(-133.04, 73.28) * mm, "end": v(-132.6, 72.82) * mm});
            skLineSegment(sketch, "E1241", {"start": v(-132.6, 72.82) * mm, "end": v(-132.18, 72.34) * mm});
            skLineSegment(sketch, "E1242", {"start": v(-132.18, 72.34) * mm, "end": v(-131.77, 71.85) * mm});
            skLineSegment(sketch, "E1243", {"start": v(-131.77, 71.85) * mm, "end": v(-131.39, 71.34) * mm});
            skLineSegment(sketch, "E1244", {"start": v(-131.39, 71.34) * mm, "end": v(-131.02, 70.81) * mm});
            skLineSegment(sketch, "E1245", {"start": v(-131.02, 70.81) * mm, "end": v(-130.68, 70.27) * mm});
            skLineSegment(sketch, "E1246", {"start": v(-130.68, 70.27) * mm, "end": v(-130.35, 69.72) * mm});
            skLineSegment(sketch, "E1247", {"start": v(-130.35, 69.72) * mm, "end": v(-130.05, 69.14) * mm});
            skLineSegment(sketch, "E1248", {"start": v(-130.05, 69.14) * mm, "end": v(-129.76, 68.56) * mm});
            skLineSegment(sketch, "E1249", {"start": v(-129.76, 68.56) * mm, "end": v(-129.5, 67.96) * mm});
            skLineSegment(sketch, "E1250", {"start": v(-129.5, 67.96) * mm, "end": v(-129.27, 67.35) * mm});
            skLineSegment(sketch, "E1251", {"start": v(-129.27, 67.35) * mm, "end": v(-129.06, 66.72) * mm});
            skArc(sketch, "E1252", {"start": v(519.25, -1058.02) * mm, "mid": v(518.15, -1060.67) * mm, "end": v(515.5, -1061.77) * mm});
            skArc(sketch, "E1253", {"start": v(515.5, -1061.77) * mm, "mid": v(512.85, -1060.67) * mm, "end": v(511.75, -1058.02) * mm});
            skArc(sketch, "E1254", {"start": v(511.75, -1058.02) * mm, "mid": v(512.85, -1055.37) * mm, "end": v(515.5, -1054.27) * mm});
            skArc(sketch, "E1255", {"start": v(515.5, -1054.27) * mm, "mid": v(518.15, -1055.37) * mm, "end": v(519.25, -1058.02) * mm});
            skArc(sketch, "E1256", {"start": v(465.74, -1058.02) * mm, "mid": v(464.64, -1060.67) * mm, "end": v(462, -1061.77) * mm});
            skArc(sketch, "E1257", {"start": v(462, -1061.77) * mm, "mid": v(459.34, -1060.67) * mm, "end": v(458.24, -1058.02) * mm});
            skArc(sketch, "E1258", {"start": v(458.24, -1058.02) * mm, "mid": v(459.34, -1055.37) * mm, "end": v(462, -1054.27) * mm});
            skArc(sketch, "E1259", {"start": v(462, -1054.27) * mm, "mid": v(464.64, -1055.37) * mm, "end": v(465.74, -1058.02) * mm});
            skArc(sketch, "E1260", {"start": v(519.25, -821.4) * mm, "mid": v(518.15, -824.05) * mm, "end": v(515.5, -825.15) * mm});
            skArc(sketch, "E1261", {"start": v(515.5, -825.15) * mm, "mid": v(512.85, -824.05) * mm, "end": v(511.75, -821.4) * mm});
            skArc(sketch, "E1262", {"start": v(511.75, -821.4) * mm, "mid": v(512.85, -818.75) * mm, "end": v(515.5, -817.65) * mm});
            skArc(sketch, "E1263", {"start": v(515.5, -817.65) * mm, "mid": v(518.15, -818.75) * mm, "end": v(519.25, -821.4) * mm});
            skArc(sketch, "E1264", {"start": v(465.74, -821.4) * mm, "mid": v(464.64, -824.05) * mm, "end": v(462, -825.15) * mm});
            skArc(sketch, "E1265", {"start": v(462, -825.15) * mm, "mid": v(459.34, -824.05) * mm, "end": v(458.24, -821.4) * mm});
            skArc(sketch, "E1266", {"start": v(458.24, -821.4) * mm, "mid": v(459.34, -818.75) * mm, "end": v(462, -817.65) * mm});
            skArc(sketch, "E1267", {"start": v(462, -817.65) * mm, "mid": v(464.64, -818.75) * mm, "end": v(465.74, -821.4) * mm});
            skArc(sketch, "E1268", {"start": v(519.25, -750.89) * mm, "mid": v(518.15, -753.54) * mm, "end": v(515.5, -754.64) * mm});
            skArc(sketch, "E1269", {"start": v(515.5, -754.64) * mm, "mid": v(512.85, -753.54) * mm, "end": v(511.75, -750.89) * mm});
            skArc(sketch, "E1270", {"start": v(511.75, -750.89) * mm, "mid": v(512.85, -748.24) * mm, "end": v(515.5, -747.14) * mm});
            skArc(sketch, "E1271", {"start": v(515.5, -747.14) * mm, "mid": v(518.15, -748.24) * mm, "end": v(519.25, -750.89) * mm});
            skArc(sketch, "E1272", {"start": v(465.74, -750.89) * mm, "mid": v(464.64, -753.54) * mm, "end": v(462, -754.64) * mm});
            skArc(sketch, "E1273", {"start": v(462, -754.64) * mm, "mid": v(459.34, -753.54) * mm, "end": v(458.24, -750.89) * mm});
            skArc(sketch, "E1274", {"start": v(458.24, -750.89) * mm, "mid": v(459.34, -748.24) * mm, "end": v(462, -747.14) * mm});
            skArc(sketch, "E1275", {"start": v(462, -747.14) * mm, "mid": v(464.64, -748.24) * mm, "end": v(465.74, -750.89) * mm});
            skArc(sketch, "E1276", {"start": v(519.25, -937.85) * mm, "mid": v(518.15, -940.5) * mm, "end": v(515.5, -941.6) * mm});
            skArc(sketch, "E1277", {"start": v(515.5, -941.6) * mm, "mid": v(512.85, -940.5) * mm, "end": v(511.75, -937.85) * mm});
            skArc(sketch, "E1278", {"start": v(511.75, -937.85) * mm, "mid": v(512.85, -935.2) * mm, "end": v(515.5, -934.1) * mm});
            skArc(sketch, "E1279", {"start": v(515.5, -934.1) * mm, "mid": v(518.15, -935.2) * mm, "end": v(519.25, -937.85) * mm});
            skArc(sketch, "E1280", {"start": v(465.74, -937.85) * mm, "mid": v(464.64, -940.5) * mm, "end": v(462, -941.6) * mm});
            skArc(sketch, "E1281", {"start": v(462, -941.6) * mm, "mid": v(459.34, -940.5) * mm, "end": v(458.24, -937.85) * mm});
            skArc(sketch, "E1282", {"start": v(458.24, -937.85) * mm, "mid": v(459.34, -935.2) * mm, "end": v(462, -934.1) * mm});
            skArc(sketch, "E1283", {"start": v(462, -934.1) * mm, "mid": v(464.64, -935.2) * mm, "end": v(465.74, -937.85) * mm});
            skArc(sketch, "E1284", {"start": v(519.25, -486.24) * mm, "mid": v(518.15, -488.9) * mm, "end": v(515.5, -490) * mm});
            skArc(sketch, "E1285", {"start": v(515.5, -490) * mm, "mid": v(512.85, -488.9) * mm, "end": v(511.75, -486.24) * mm});
            skArc(sketch, "E1286", {"start": v(511.75, -486.24) * mm, "mid": v(512.85, -483.6) * mm, "end": v(515.5, -482.5) * mm});
            skArc(sketch, "E1287", {"start": v(515.5, -482.5) * mm, "mid": v(518.15, -483.6) * mm, "end": v(519.25, -486.24) * mm});
            skArc(sketch, "E1288", {"start": v(465.74, -486.24) * mm, "mid": v(464.64, -488.9) * mm, "end": v(462, -490) * mm});
            skArc(sketch, "E1289", {"start": v(462, -490) * mm, "mid": v(459.34, -488.9) * mm, "end": v(458.24, -486.24) * mm});
            skArc(sketch, "E1290", {"start": v(458.24, -486.24) * mm, "mid": v(459.34, -483.6) * mm, "end": v(462, -482.5) * mm});
            skArc(sketch, "E1291", {"start": v(462, -482.5) * mm, "mid": v(464.64, -483.6) * mm, "end": v(465.74, -486.24) * mm});
            skArc(sketch, "E1292", {"start": v(519.25, -625.89) * mm, "mid": v(518.15, -628.54) * mm, "end": v(515.5, -629.64) * mm});
            skArc(sketch, "E1293", {"start": v(515.5, -629.64) * mm, "mid": v(512.85, -628.54) * mm, "end": v(511.75, -625.89) * mm});
            skArc(sketch, "E1294", {"start": v(511.75, -625.89) * mm, "mid": v(512.85, -623.24) * mm, "end": v(515.5, -622.14) * mm});
            skArc(sketch, "E1295", {"start": v(515.5, -622.14) * mm, "mid": v(518.15, -623.24) * mm, "end": v(519.25, -625.89) * mm});
            skArc(sketch, "E1296", {"start": v(465.74, -625.89) * mm, "mid": v(464.64, -628.54) * mm, "end": v(462, -629.64) * mm});
            skArc(sketch, "E1297", {"start": v(462, -629.64) * mm, "mid": v(459.34, -628.54) * mm, "end": v(458.24, -625.89) * mm});
            skArc(sketch, "E1298", {"start": v(458.24, -625.89) * mm, "mid": v(459.34, -623.24) * mm, "end": v(462, -622.14) * mm});
            skArc(sketch, "E1299", {"start": v(462, -622.14) * mm, "mid": v(464.64, -623.24) * mm, "end": v(465.74, -625.89) * mm});
            skArc(sketch, "E1300", {"start": v(519.25, -336.24) * mm, "mid": v(518.15, -338.9) * mm, "end": v(515.5, -340) * mm});
            skArc(sketch, "E1301", {"start": v(515.5, -340) * mm, "mid": v(512.85, -338.9) * mm, "end": v(511.75, -336.24) * mm});
            skArc(sketch, "E1302", {"start": v(511.75, -336.24) * mm, "mid": v(512.85, -333.6) * mm, "end": v(515.5, -332.5) * mm});
            skArc(sketch, "E1303", {"start": v(515.5, -332.5) * mm, "mid": v(518.15, -333.6) * mm, "end": v(519.25, -336.24) * mm});
            skArc(sketch, "E1304", {"start": v(465.74, -336.24) * mm, "mid": v(464.64, -338.9) * mm, "end": v(462, -340) * mm});
            skArc(sketch, "E1305", {"start": v(462, -340) * mm, "mid": v(459.34, -338.9) * mm, "end": v(458.24, -336.24) * mm});
            skArc(sketch, "E1306", {"start": v(458.24, -336.24) * mm, "mid": v(459.34, -333.6) * mm, "end": v(462, -332.5) * mm});
            skArc(sketch, "E1307", {"start": v(462, -332.5) * mm, "mid": v(464.64, -333.6) * mm, "end": v(465.74, -336.24) * mm});
            skArc(sketch, "E1308", {"start": v(519.25, -186.24) * mm, "mid": v(518.15, -188.9) * mm, "end": v(515.5, -190) * mm});
            skArc(sketch, "E1309", {"start": v(515.5, -190) * mm, "mid": v(512.85, -188.9) * mm, "end": v(511.75, -186.24) * mm});
            skArc(sketch, "E1310", {"start": v(511.75, -186.24) * mm, "mid": v(512.85, -183.6) * mm, "end": v(515.5, -182.5) * mm});
            skArc(sketch, "E1311", {"start": v(515.5, -182.5) * mm, "mid": v(518.15, -183.6) * mm, "end": v(519.25, -186.24) * mm});
            skArc(sketch, "E1312", {"start": v(465.74, -186.24) * mm, "mid": v(464.64, -188.9) * mm, "end": v(462, -190) * mm});
            skArc(sketch, "E1313", {"start": v(462, -190) * mm, "mid": v(459.34, -188.9) * mm, "end": v(458.24, -186.24) * mm});
            skArc(sketch, "E1314", {"start": v(458.24, -186.24) * mm, "mid": v(459.34, -183.6) * mm, "end": v(462, -182.5) * mm});
            skArc(sketch, "E1315", {"start": v(462, -182.5) * mm, "mid": v(464.64, -183.6) * mm, "end": v(465.74, -186.24) * mm});
            skArc(sketch, "E1316", {"start": v(519.25, -64.78) * mm, "mid": v(518.15, -67.43) * mm, "end": v(515.5, -68.53) * mm});
            skArc(sketch, "E1317", {"start": v(515.5, -68.53) * mm, "mid": v(512.85, -67.43) * mm, "end": v(511.75, -64.78) * mm});
            skArc(sketch, "E1318", {"start": v(511.75, -64.78) * mm, "mid": v(512.85, -62.13) * mm, "end": v(515.5, -61.03) * mm});
            skArc(sketch, "E1319", {"start": v(515.5, -61.03) * mm, "mid": v(518.15, -62.13) * mm, "end": v(519.25, -64.78) * mm});
            skArc(sketch, "E1320", {"start": v(465.74, -64.78) * mm, "mid": v(464.64, -67.43) * mm, "end": v(462, -68.53) * mm});
            skArc(sketch, "E1321", {"start": v(462, -68.53) * mm, "mid": v(459.34, -67.43) * mm, "end": v(458.24, -64.78) * mm});
            skArc(sketch, "E1322", {"start": v(458.24, -64.78) * mm, "mid": v(459.34, -62.13) * mm, "end": v(462, -61.03) * mm});
            skArc(sketch, "E1323", {"start": v(462, -61.03) * mm, "mid": v(464.64, -62.13) * mm, "end": v(465.74, -64.78) * mm});
            skArc(sketch, "E1324", {"start": v(519.25, 56.91) * mm, "mid": v(518.15, 54.26) * mm, "end": v(515.5, 53.16) * mm});
            skArc(sketch, "E1325", {"start": v(515.5, 53.16) * mm, "mid": v(512.85, 54.26) * mm, "end": v(511.75, 56.91) * mm});
            skArc(sketch, "E1326", {"start": v(511.75, 56.91) * mm, "mid": v(512.85, 59.56) * mm, "end": v(515.5, 60.66) * mm});
            skArc(sketch, "E1327", {"start": v(515.5, 60.66) * mm, "mid": v(518.15, 59.56) * mm, "end": v(519.25, 56.91) * mm});
            skArc(sketch, "E1328", {"start": v(465.74, 56.91) * mm, "mid": v(464.64, 54.26) * mm, "end": v(462, 53.16) * mm});
            skArc(sketch, "E1329", {"start": v(462, 53.16) * mm, "mid": v(459.34, 54.26) * mm, "end": v(458.24, 56.91) * mm});
            skArc(sketch, "E1330", {"start": v(458.24, 56.91) * mm, "mid": v(459.34, 59.56) * mm, "end": v(462, 60.66) * mm});
            skArc(sketch, "E1331", {"start": v(462, 60.66) * mm, "mid": v(464.64, 59.56) * mm, "end": v(465.74, 56.91) * mm});
            skArc(sketch, "E1332", {"start": v(519.25, 300.23) * mm, "mid": v(518.15, 297.57) * mm, "end": v(515.5, 296.48) * mm});
            skArc(sketch, "E1333", {"start": v(515.5, 296.48) * mm, "mid": v(512.85, 297.57) * mm, "end": v(511.75, 300.23) * mm});
            skArc(sketch, "E1334", {"start": v(511.75, 300.23) * mm, "mid": v(512.85, 302.88) * mm, "end": v(515.5, 303.98) * mm});
            skArc(sketch, "E1335", {"start": v(515.5, 303.98) * mm, "mid": v(518.15, 302.88) * mm, "end": v(519.25, 300.23) * mm});
            skArc(sketch, "E1336", {"start": v(465.74, 300.23) * mm, "mid": v(464.64, 297.57) * mm, "end": v(462, 296.48) * mm});
            skArc(sketch, "E1337", {"start": v(462, 296.48) * mm, "mid": v(459.34, 297.57) * mm, "end": v(458.24, 300.23) * mm});
            skArc(sketch, "E1338", {"start": v(458.24, 300.23) * mm, "mid": v(459.34, 302.88) * mm, "end": v(462, 303.98) * mm});
            skArc(sketch, "E1339", {"start": v(462, 303.98) * mm, "mid": v(464.64, 302.88) * mm, "end": v(465.74, 300.23) * mm});
            skArc(sketch, "E1340", {"start": v(519.25, 180.68) * mm, "mid": v(518.15, 178.03) * mm, "end": v(515.5, 176.93) * mm});
            skArc(sketch, "E1341", {"start": v(515.5, 176.93) * mm, "mid": v(512.85, 178.03) * mm, "end": v(511.75, 180.68) * mm});
            skArc(sketch, "E1342", {"start": v(511.75, 180.68) * mm, "mid": v(512.85, 183.33) * mm, "end": v(515.5, 184.43) * mm});
            skArc(sketch, "E1343", {"start": v(515.5, 184.43) * mm, "mid": v(518.15, 183.33) * mm, "end": v(519.25, 180.68) * mm});
            skArc(sketch, "E1344", {"start": v(465.74, 180.68) * mm, "mid": v(464.64, 178.03) * mm, "end": v(462, 176.93) * mm});
            skArc(sketch, "E1345", {"start": v(462, 176.93) * mm, "mid": v(459.34, 178.03) * mm, "end": v(458.24, 180.68) * mm});
            skArc(sketch, "E1346", {"start": v(458.24, 180.68) * mm, "mid": v(459.34, 183.33) * mm, "end": v(462, 184.43) * mm});
            skArc(sketch, "E1347", {"start": v(462, 184.43) * mm, "mid": v(464.64, 183.33) * mm, "end": v(465.74, 180.68) * mm});
            skArc(sketch, "E1348", {"start": v(519.25, 600.29) * mm, "mid": v(518.15, 597.64) * mm, "end": v(515.5, 596.54) * mm});
            skArc(sketch, "E1349", {"start": v(515.5, 596.54) * mm, "mid": v(512.85, 597.64) * mm, "end": v(511.75, 600.29) * mm});
            skArc(sketch, "E1350", {"start": v(511.75, 600.29) * mm, "mid": v(512.85, 602.94) * mm, "end": v(515.5, 604.04) * mm});
            skArc(sketch, "E1351", {"start": v(515.5, 604.04) * mm, "mid": v(518.15, 602.94) * mm, "end": v(519.25, 600.29) * mm});
            skArc(sketch, "E1352", {"start": v(465.74, 600.29) * mm, "mid": v(464.64, 597.64) * mm, "end": v(462, 596.54) * mm});
            skArc(sketch, "E1353", {"start": v(462, 596.54) * mm, "mid": v(459.34, 597.64) * mm, "end": v(458.24, 600.29) * mm});
            skArc(sketch, "E1354", {"start": v(458.24, 600.29) * mm, "mid": v(459.34, 602.94) * mm, "end": v(462, 604.04) * mm});
            skArc(sketch, "E1355", {"start": v(462, 604.04) * mm, "mid": v(464.64, 602.94) * mm, "end": v(465.74, 600.29) * mm});
            skArc(sketch, "E1356", {"start": v(519.25, 450.29) * mm, "mid": v(518.15, 447.64) * mm, "end": v(515.5, 446.54) * mm});
            skArc(sketch, "E1357", {"start": v(515.5, 446.54) * mm, "mid": v(512.85, 447.64) * mm, "end": v(511.75, 450.29) * mm});
            skArc(sketch, "E1358", {"start": v(511.75, 450.29) * mm, "mid": v(512.85, 452.94) * mm, "end": v(515.5, 454.04) * mm});
            skArc(sketch, "E1359", {"start": v(515.5, 454.04) * mm, "mid": v(518.15, 452.94) * mm, "end": v(519.25, 450.29) * mm});
            skArc(sketch, "E1360", {"start": v(465.74, 450.29) * mm, "mid": v(464.64, 447.64) * mm, "end": v(462, 446.54) * mm});
            skArc(sketch, "E1361", {"start": v(462, 446.54) * mm, "mid": v(459.34, 447.64) * mm, "end": v(458.24, 450.29) * mm});
            skArc(sketch, "E1362", {"start": v(458.24, 450.29) * mm, "mid": v(459.34, 452.94) * mm, "end": v(462, 454.04) * mm});
            skArc(sketch, "E1363", {"start": v(462, 454.04) * mm, "mid": v(464.64, 452.94) * mm, "end": v(465.74, 450.29) * mm});
            skArc(sketch, "E1364", {"start": v(519.25, 750.29) * mm, "mid": v(518.15, 747.64) * mm, "end": v(515.5, 746.54) * mm});
            skArc(sketch, "E1365", {"start": v(515.5, 746.54) * mm, "mid": v(512.85, 747.64) * mm, "end": v(511.75, 750.29) * mm});
            skArc(sketch, "E1366", {"start": v(511.75, 750.29) * mm, "mid": v(512.85, 752.94) * mm, "end": v(515.5, 754.04) * mm});
            skArc(sketch, "E1367", {"start": v(515.5, 754.04) * mm, "mid": v(518.15, 752.94) * mm, "end": v(519.25, 750.29) * mm});
            skArc(sketch, "E1368", {"start": v(465.74, 750.29) * mm, "mid": v(464.64, 747.64) * mm, "end": v(462, 746.54) * mm});
            skArc(sketch, "E1369", {"start": v(462, 746.54) * mm, "mid": v(459.34, 747.64) * mm, "end": v(458.24, 750.29) * mm});
            skArc(sketch, "E1370", {"start": v(458.24, 750.29) * mm, "mid": v(459.34, 752.94) * mm, "end": v(462, 754.04) * mm});
            skArc(sketch, "E1371", {"start": v(462, 754.04) * mm, "mid": v(464.64, 752.94) * mm, "end": v(465.74, 750.29) * mm});
            skArc(sketch, "E1372", {"start": v(519.25, 870.29) * mm, "mid": v(518.15, 867.64) * mm, "end": v(515.5, 866.54) * mm});
            skArc(sketch, "E1373", {"start": v(515.5, 866.54) * mm, "mid": v(512.85, 867.64) * mm, "end": v(511.75, 870.29) * mm});
            skArc(sketch, "E1374", {"start": v(511.75, 870.29) * mm, "mid": v(512.85, 872.94) * mm, "end": v(515.5, 874.04) * mm});
            skArc(sketch, "E1375", {"start": v(515.5, 874.04) * mm, "mid": v(518.15, 872.94) * mm, "end": v(519.25, 870.29) * mm});
            skArc(sketch, "E1376", {"start": v(465.74, 870.29) * mm, "mid": v(464.64, 867.64) * mm, "end": v(462, 866.54) * mm});
            skArc(sketch, "E1377", {"start": v(462, 866.54) * mm, "mid": v(459.34, 867.64) * mm, "end": v(458.24, 870.29) * mm});
            skArc(sketch, "E1378", {"start": v(458.24, 870.29) * mm, "mid": v(459.34, 872.94) * mm, "end": v(462, 874.04) * mm});
            skArc(sketch, "E1379", {"start": v(462, 874.04) * mm, "mid": v(464.64, 872.94) * mm, "end": v(465.74, 870.29) * mm});
            skArc(sketch, "E1380", {"start": v(519.25, 1050.29) * mm, "mid": v(518.15, 1047.64) * mm, "end": v(515.5, 1046.54) * mm});
            skArc(sketch, "E1381", {"start": v(515.5, 1046.54) * mm, "mid": v(512.85, 1047.64) * mm, "end": v(511.75, 1050.29) * mm});
            skArc(sketch, "E1382", {"start": v(511.75, 1050.29) * mm, "mid": v(512.85, 1052.94) * mm, "end": v(515.5, 1054.04) * mm});
            skArc(sketch, "E1383", {"start": v(515.5, 1054.04) * mm, "mid": v(518.15, 1052.94) * mm, "end": v(519.25, 1050.29) * mm});
            skArc(sketch, "E1384", {"start": v(465.74, 1050.29) * mm, "mid": v(464.64, 1047.64) * mm, "end": v(462, 1046.54) * mm});
            skArc(sketch, "E1385", {"start": v(462, 1046.54) * mm, "mid": v(459.34, 1047.64) * mm, "end": v(458.24, 1050.29) * mm});
            skArc(sketch, "E1386", {"start": v(458.24, 1050.29) * mm, "mid": v(459.34, 1052.94) * mm, "end": v(462, 1054.04) * mm});
            skArc(sketch, "E1387", {"start": v(462, 1054.04) * mm, "mid": v(464.64, 1052.94) * mm, "end": v(465.74, 1050.29) * mm});
            skArc(sketch, "E1388", {"start": v(519.25, 1170.47) * mm, "mid": v(518.15, 1167.82) * mm, "end": v(515.5, 1166.72) * mm});
            skArc(sketch, "E1389", {"start": v(515.5, 1166.72) * mm, "mid": v(512.85, 1167.82) * mm, "end": v(511.75, 1170.47) * mm});
            skArc(sketch, "E1390", {"start": v(511.75, 1170.47) * mm, "mid": v(512.85, 1173.12) * mm, "end": v(515.5, 1174.22) * mm});
            skArc(sketch, "E1391", {"start": v(515.5, 1174.22) * mm, "mid": v(518.15, 1173.12) * mm, "end": v(519.25, 1170.47) * mm});
            skArc(sketch, "E1392", {"start": v(465.74, 1170.47) * mm, "mid": v(464.64, 1167.82) * mm, "end": v(462, 1166.72) * mm});
            skArc(sketch, "E1393", {"start": v(462, 1166.72) * mm, "mid": v(459.34, 1167.82) * mm, "end": v(458.24, 1170.47) * mm});
            skArc(sketch, "E1394", {"start": v(458.24, 1170.47) * mm, "mid": v(459.34, 1173.12) * mm, "end": v(462, 1174.22) * mm});
            skArc(sketch, "E1395", {"start": v(462, 1174.22) * mm, "mid": v(464.64, 1173.12) * mm, "end": v(465.74, 1170.47) * mm});
            skArc(sketch, "E1396", {"start": v(519.25, 930.29) * mm, "mid": v(518.15, 927.64) * mm, "end": v(515.5, 926.54) * mm});
            skArc(sketch, "E1397", {"start": v(515.5, 926.54) * mm, "mid": v(512.85, 927.64) * mm, "end": v(511.75, 930.29) * mm});
            skArc(sketch, "E1398", {"start": v(511.75, 930.29) * mm, "mid": v(512.85, 932.94) * mm, "end": v(515.5, 934.04) * mm});
            skArc(sketch, "E1399", {"start": v(515.5, 934.04) * mm, "mid": v(518.15, 932.94) * mm, "end": v(519.25, 930.29) * mm});
            skArc(sketch, "E1400", {"start": v(465.74, 930.29) * mm, "mid": v(464.64, 927.64) * mm, "end": v(462, 926.54) * mm});
            skArc(sketch, "E1401", {"start": v(462, 926.54) * mm, "mid": v(459.34, 927.64) * mm, "end": v(458.24, 930.29) * mm});
            skArc(sketch, "E1402", {"start": v(458.24, 930.29) * mm, "mid": v(459.34, 932.94) * mm, "end": v(462, 934.04) * mm});
            skArc(sketch, "E1403", {"start": v(462, 934.04) * mm, "mid": v(464.64, 932.94) * mm, "end": v(465.74, 930.29) * mm});
            skArc(sketch, "E1404", {"start": v(-569.72, -1058.02) * mm, "mid": v(-570.82, -1060.67) * mm, "end": v(-573.47, -1061.77) * mm});
            skArc(sketch, "E1405", {"start": v(-573.47, -1061.77) * mm, "mid": v(-576.12, -1060.67) * mm, "end": v(-577.22, -1058.02) * mm});
            skArc(sketch, "E1406", {"start": v(-577.22, -1058.02) * mm, "mid": v(-576.12, -1055.37) * mm, "end": v(-573.47, -1054.27) * mm});
            skArc(sketch, "E1407", {"start": v(-573.47, -1054.27) * mm, "mid": v(-570.82, -1055.37) * mm, "end": v(-569.72, -1058.02) * mm});
            skArc(sketch, "E1408", {"start": v(-569.72, -821.4) * mm, "mid": v(-570.82, -824.05) * mm, "end": v(-573.47, -825.15) * mm});
            skArc(sketch, "E1409", {"start": v(-573.47, -825.15) * mm, "mid": v(-576.12, -824.05) * mm, "end": v(-577.22, -821.4) * mm});
            skArc(sketch, "E1410", {"start": v(-577.22, -821.4) * mm, "mid": v(-576.12, -818.75) * mm, "end": v(-573.47, -817.65) * mm});
            skArc(sketch, "E1411", {"start": v(-573.47, -817.65) * mm, "mid": v(-570.82, -818.75) * mm, "end": v(-569.72, -821.4) * mm});
            skArc(sketch, "E1412", {"start": v(-569.72, -750.89) * mm, "mid": v(-570.82, -753.54) * mm, "end": v(-573.47, -754.64) * mm});
            skArc(sketch, "E1413", {"start": v(-573.47, -754.64) * mm, "mid": v(-576.12, -753.54) * mm, "end": v(-577.22, -750.89) * mm});
            skArc(sketch, "E1414", {"start": v(-577.22, -750.89) * mm, "mid": v(-576.12, -748.24) * mm, "end": v(-573.47, -747.14) * mm});
            skArc(sketch, "E1415", {"start": v(-573.47, -747.14) * mm, "mid": v(-570.82, -748.24) * mm, "end": v(-569.72, -750.89) * mm});
            skArc(sketch, "E1416", {"start": v(-569.72, -937.85) * mm, "mid": v(-570.82, -940.5) * mm, "end": v(-573.47, -941.6) * mm});
            skArc(sketch, "E1417", {"start": v(-573.47, -941.6) * mm, "mid": v(-576.12, -940.5) * mm, "end": v(-577.22, -937.85) * mm});
            skArc(sketch, "E1418", {"start": v(-577.22, -937.85) * mm, "mid": v(-576.12, -935.2) * mm, "end": v(-573.47, -934.1) * mm});
            skArc(sketch, "E1419", {"start": v(-573.47, -934.1) * mm, "mid": v(-570.82, -935.2) * mm, "end": v(-569.72, -937.85) * mm});
            skArc(sketch, "E1420", {"start": v(-569.72, -486.24) * mm, "mid": v(-570.82, -488.9) * mm, "end": v(-573.47, -490) * mm});
            skArc(sketch, "E1421", {"start": v(-573.47, -490) * mm, "mid": v(-576.12, -488.9) * mm, "end": v(-577.22, -486.24) * mm});
            skArc(sketch, "E1422", {"start": v(-577.22, -486.24) * mm, "mid": v(-576.12, -483.6) * mm, "end": v(-573.47, -482.5) * mm});
            skArc(sketch, "E1423", {"start": v(-573.47, -482.5) * mm, "mid": v(-570.82, -483.6) * mm, "end": v(-569.72, -486.24) * mm});
            skArc(sketch, "E1424", {"start": v(-569.72, -625.89) * mm, "mid": v(-570.82, -628.54) * mm, "end": v(-573.47, -629.64) * mm});
            skArc(sketch, "E1425", {"start": v(-573.47, -629.64) * mm, "mid": v(-576.12, -628.54) * mm, "end": v(-577.22, -625.89) * mm});
            skArc(sketch, "E1426", {"start": v(-577.22, -625.89) * mm, "mid": v(-576.12, -623.24) * mm, "end": v(-573.47, -622.14) * mm});
            skArc(sketch, "E1427", {"start": v(-573.47, -622.14) * mm, "mid": v(-570.82, -623.24) * mm, "end": v(-569.72, -625.89) * mm});
            skArc(sketch, "E1428", {"start": v(-569.72, -336.24) * mm, "mid": v(-570.82, -338.9) * mm, "end": v(-573.47, -340) * mm});
            skArc(sketch, "E1429", {"start": v(-573.47, -340) * mm, "mid": v(-576.12, -338.9) * mm, "end": v(-577.22, -336.24) * mm});
            skArc(sketch, "E1430", {"start": v(-577.22, -336.24) * mm, "mid": v(-576.12, -333.6) * mm, "end": v(-573.47, -332.5) * mm});
            skArc(sketch, "E1431", {"start": v(-573.47, -332.5) * mm, "mid": v(-570.82, -333.6) * mm, "end": v(-569.72, -336.24) * mm});
            skArc(sketch, "E1432", {"start": v(-569.72, -186.24) * mm, "mid": v(-570.82, -188.9) * mm, "end": v(-573.47, -190) * mm});
            skArc(sketch, "E1433", {"start": v(-573.47, -190) * mm, "mid": v(-576.12, -188.9) * mm, "end": v(-577.22, -186.24) * mm});
            skArc(sketch, "E1434", {"start": v(-577.22, -186.24) * mm, "mid": v(-576.12, -183.6) * mm, "end": v(-573.47, -182.5) * mm});
            skArc(sketch, "E1435", {"start": v(-573.47, -182.5) * mm, "mid": v(-570.82, -183.6) * mm, "end": v(-569.72, -186.24) * mm});
            skArc(sketch, "E1436", {"start": v(-569.72, -64.78) * mm, "mid": v(-570.82, -67.43) * mm, "end": v(-573.47, -68.53) * mm});
            skArc(sketch, "E1437", {"start": v(-573.47, -68.53) * mm, "mid": v(-576.12, -67.43) * mm, "end": v(-577.22, -64.78) * mm});
            skArc(sketch, "E1438", {"start": v(-577.22, -64.78) * mm, "mid": v(-576.12, -62.13) * mm, "end": v(-573.47, -61.03) * mm});
            skArc(sketch, "E1439", {"start": v(-573.47, -61.03) * mm, "mid": v(-570.82, -62.13) * mm, "end": v(-569.72, -64.78) * mm});
            skArc(sketch, "E1440", {"start": v(-569.72, 56.91) * mm, "mid": v(-570.82, 54.26) * mm, "end": v(-573.47, 53.16) * mm});
            skArc(sketch, "E1441", {"start": v(-573.47, 53.16) * mm, "mid": v(-576.12, 54.26) * mm, "end": v(-577.22, 56.91) * mm});
            skArc(sketch, "E1442", {"start": v(-577.22, 56.91) * mm, "mid": v(-576.12, 59.56) * mm, "end": v(-573.47, 60.66) * mm});
            skArc(sketch, "E1443", {"start": v(-573.47, 60.66) * mm, "mid": v(-570.82, 59.56) * mm, "end": v(-569.72, 56.91) * mm});
            skArc(sketch, "E1444", {"start": v(-569.72, 300.23) * mm, "mid": v(-570.82, 297.57) * mm, "end": v(-573.47, 296.48) * mm});
            skArc(sketch, "E1445", {"start": v(-573.47, 296.48) * mm, "mid": v(-576.12, 297.57) * mm, "end": v(-577.22, 300.23) * mm});
            skArc(sketch, "E1446", {"start": v(-577.22, 300.23) * mm, "mid": v(-576.12, 302.88) * mm, "end": v(-573.47, 303.98) * mm});
            skArc(sketch, "E1447", {"start": v(-573.47, 303.98) * mm, "mid": v(-570.82, 302.88) * mm, "end": v(-569.72, 300.23) * mm});
            skArc(sketch, "E1448", {"start": v(-569.72, 180.68) * mm, "mid": v(-570.82, 178.03) * mm, "end": v(-573.47, 176.93) * mm});
            skArc(sketch, "E1449", {"start": v(-573.47, 176.93) * mm, "mid": v(-576.12, 178.03) * mm, "end": v(-577.22, 180.68) * mm});
            skArc(sketch, "E1450", {"start": v(-577.22, 180.68) * mm, "mid": v(-576.12, 183.33) * mm, "end": v(-573.47, 184.43) * mm});
            skArc(sketch, "E1451", {"start": v(-573.47, 184.43) * mm, "mid": v(-570.82, 183.33) * mm, "end": v(-569.72, 180.68) * mm});
            skArc(sketch, "E1452", {"start": v(-569.72, 600.29) * mm, "mid": v(-570.82, 597.64) * mm, "end": v(-573.47, 596.54) * mm});
            skArc(sketch, "E1453", {"start": v(-573.47, 596.54) * mm, "mid": v(-576.12, 597.64) * mm, "end": v(-577.22, 600.29) * mm});
            skArc(sketch, "E1454", {"start": v(-577.22, 600.29) * mm, "mid": v(-576.12, 602.94) * mm, "end": v(-573.47, 604.04) * mm});
            skArc(sketch, "E1455", {"start": v(-573.47, 604.04) * mm, "mid": v(-570.82, 602.94) * mm, "end": v(-569.72, 600.29) * mm});
            skArc(sketch, "E1456", {"start": v(-569.72, 450.29) * mm, "mid": v(-570.82, 447.64) * mm, "end": v(-573.47, 446.54) * mm});
            skArc(sketch, "E1457", {"start": v(-573.47, 446.54) * mm, "mid": v(-576.12, 447.64) * mm, "end": v(-577.22, 450.29) * mm});
            skArc(sketch, "E1458", {"start": v(-577.22, 450.29) * mm, "mid": v(-576.12, 452.94) * mm, "end": v(-573.47, 454.04) * mm});
            skArc(sketch, "E1459", {"start": v(-573.47, 454.04) * mm, "mid": v(-570.82, 452.94) * mm, "end": v(-569.72, 450.29) * mm});
            skArc(sketch, "E1460", {"start": v(-569.72, 750.29) * mm, "mid": v(-570.82, 747.64) * mm, "end": v(-573.47, 746.54) * mm});
            skArc(sketch, "E1461", {"start": v(-573.47, 746.54) * mm, "mid": v(-576.12, 747.64) * mm, "end": v(-577.22, 750.29) * mm});
            skArc(sketch, "E1462", {"start": v(-577.22, 750.29) * mm, "mid": v(-576.12, 752.94) * mm, "end": v(-573.47, 754.04) * mm});
            skArc(sketch, "E1463", {"start": v(-573.47, 754.04) * mm, "mid": v(-570.82, 752.94) * mm, "end": v(-569.72, 750.29) * mm});
            skArc(sketch, "E1464", {"start": v(-569.72, 870.29) * mm, "mid": v(-570.82, 867.64) * mm, "end": v(-573.47, 866.54) * mm});
            skArc(sketch, "E1465", {"start": v(-573.47, 866.54) * mm, "mid": v(-576.12, 867.64) * mm, "end": v(-577.22, 870.29) * mm});
            skArc(sketch, "E1466", {"start": v(-577.22, 870.29) * mm, "mid": v(-576.12, 872.94) * mm, "end": v(-573.47, 874.04) * mm});
            skArc(sketch, "E1467", {"start": v(-573.47, 874.04) * mm, "mid": v(-570.82, 872.94) * mm, "end": v(-569.72, 870.29) * mm});
            skArc(sketch, "E1468", {"start": v(-569.72, 1050.29) * mm, "mid": v(-570.82, 1047.64) * mm, "end": v(-573.47, 1046.54) * mm});
            skArc(sketch, "E1469", {"start": v(-573.47, 1046.54) * mm, "mid": v(-576.12, 1047.64) * mm, "end": v(-577.22, 1050.29) * mm});
            skArc(sketch, "E1470", {"start": v(-577.22, 1050.29) * mm, "mid": v(-576.12, 1052.94) * mm, "end": v(-573.47, 1054.04) * mm});
            skArc(sketch, "E1471", {"start": v(-573.47, 1054.04) * mm, "mid": v(-570.82, 1052.94) * mm, "end": v(-569.72, 1050.29) * mm});
            skArc(sketch, "E1472", {"start": v(-569.72, 1170.47) * mm, "mid": v(-570.82, 1167.82) * mm, "end": v(-573.47, 1166.72) * mm});
            skArc(sketch, "E1473", {"start": v(-573.47, 1166.72) * mm, "mid": v(-576.12, 1167.82) * mm, "end": v(-577.22, 1170.47) * mm});
            skArc(sketch, "E1474", {"start": v(-577.22, 1170.47) * mm, "mid": v(-576.12, 1173.12) * mm, "end": v(-573.47, 1174.22) * mm});
            skArc(sketch, "E1475", {"start": v(-573.47, 1174.22) * mm, "mid": v(-570.82, 1173.12) * mm, "end": v(-569.72, 1170.47) * mm});
            skArc(sketch, "E1476", {"start": v(-569.72, 930.29) * mm, "mid": v(-570.82, 927.64) * mm, "end": v(-573.47, 926.54) * mm});
            skArc(sketch, "E1477", {"start": v(-573.47, 926.54) * mm, "mid": v(-576.12, 927.64) * mm, "end": v(-577.22, 930.29) * mm});
            skArc(sketch, "E1478", {"start": v(-577.22, 930.29) * mm, "mid": v(-576.12, 932.94) * mm, "end": v(-573.47, 934.04) * mm});
            skArc(sketch, "E1479", {"start": v(-573.47, 934.04) * mm, "mid": v(-570.82, 932.94) * mm, "end": v(-569.72, 930.29) * mm});
            skArc(sketch, "E1480", {"start": v(-543.62, -1140.44) * mm, "mid": v(-546.34, -1139.31) * mm, "end": v(-547.47, -1136.6) * mm});
            skArc(sketch, "E1481", {"start": v(-547.47, -1136.6) * mm, "mid": v(-546.34, -1133.88) * mm, "end": v(-543.62, -1132.75) * mm});
            skArc(sketch, "E1482", {"start": v(-543.62, -1132.75) * mm, "mid": v(-540.9, -1133.88) * mm, "end": v(-539.78, -1136.6) * mm});
            skArc(sketch, "E1483", {"start": v(-539.78, -1136.6) * mm, "mid": v(-540.9, -1139.31) * mm, "end": v(-543.62, -1140.44) * mm});
            skArc(sketch, "E1484", {"start": v(-56.91, -1146.45) * mm, "mid": v(-59.63, -1145.32) * mm, "end": v(-60.76, -1142.6) * mm});
            skArc(sketch, "E1485", {"start": v(-60.76, -1142.6) * mm, "mid": v(-59.63, -1139.88) * mm, "end": v(-56.91, -1138.76) * mm});
            skArc(sketch, "E1486", {"start": v(-56.91, -1138.76) * mm, "mid": v(-54.2, -1139.88) * mm, "end": v(-53.07, -1142.6) * mm});
            skArc(sketch, "E1487", {"start": v(-53.07, -1142.6) * mm, "mid": v(-54.2, -1145.32) * mm, "end": v(-56.91, -1146.45) * mm});
            skArc(sketch, "E1488", {"start": v(462.85, -1149.45) * mm, "mid": v(460.13, -1148.33) * mm, "end": v(459, -1145.6) * mm});
            skArc(sketch, "E1489", {"start": v(459, -1145.6) * mm, "mid": v(460.13, -1142.89) * mm, "end": v(462.85, -1141.76) * mm});
            skArc(sketch, "E1490", {"start": v(462.85, -1141.76) * mm, "mid": v(465.57, -1142.89) * mm, "end": v(466.7, -1145.6) * mm});
            skArc(sketch, "E1491", {"start": v(466.7, -1145.6) * mm, "mid": v(465.57, -1148.33) * mm, "end": v(462.85, -1149.45) * mm});
            skArc(sketch, "E1492", {"start": v(-243.18, -776.9) * mm, "mid": v(-245.9, -775.78) * mm, "end": v(-247.03, -773.06) * mm});
            skArc(sketch, "E1493", {"start": v(-247.03, -773.06) * mm, "mid": v(-245.9, -770.34) * mm, "end": v(-243.18, -769.22) * mm});
            skArc(sketch, "E1494", {"start": v(-243.18, -769.22) * mm, "mid": v(-240.46, -770.34) * mm, "end": v(-239.34, -773.06) * mm});
            skArc(sketch, "E1495", {"start": v(-239.34, -773.06) * mm, "mid": v(-240.46, -775.78) * mm, "end": v(-243.18, -776.9) * mm});
            skArc(sketch, "E1496", {"start": v(132.37, -776.9) * mm, "mid": v(129.65, -775.78) * mm, "end": v(128.52, -773.06) * mm});
            skArc(sketch, "E1497", {"start": v(128.52, -773.06) * mm, "mid": v(129.65, -770.34) * mm, "end": v(132.37, -769.22) * mm});
            skArc(sketch, "E1498", {"start": v(132.37, -769.22) * mm, "mid": v(135.08, -770.34) * mm, "end": v(136.21, -773.06) * mm});
            skArc(sketch, "E1499", {"start": v(136.21, -773.06) * mm, "mid": v(135.08, -775.78) * mm, "end": v(132.37, -776.9) * mm});
            skArc(sketch, "E1500", {"start": v(-267.22, -293.2) * mm, "mid": v(-269.94, -292.08) * mm, "end": v(-271.06, -289.36) * mm});
            skArc(sketch, "E1501", {"start": v(-271.06, -289.36) * mm, "mid": v(-269.94, -286.64) * mm, "end": v(-267.22, -285.51) * mm});
            skArc(sketch, "E1502", {"start": v(-267.22, -285.51) * mm, "mid": v(-264.5, -286.64) * mm, "end": v(-263.37, -289.36) * mm});
            skArc(sketch, "E1503", {"start": v(-263.37, -289.36) * mm, "mid": v(-264.5, -292.08) * mm, "end": v(-267.22, -293.2) * mm});
            skArc(sketch, "E1504", {"start": v(198.46, -314.23) * mm, "mid": v(195.74, -313.1) * mm, "end": v(194.62, -310.39) * mm});
            skArc(sketch, "E1505", {"start": v(194.62, -310.39) * mm, "mid": v(195.74, -307.67) * mm, "end": v(198.46, -306.54) * mm});
            skArc(sketch, "E1506", {"start": v(198.46, -306.54) * mm, "mid": v(201.18, -307.67) * mm, "end": v(202.3, -310.39) * mm});
            skArc(sketch, "E1507", {"start": v(202.3, -310.39) * mm, "mid": v(201.18, -313.1) * mm, "end": v(198.46, -314.23) * mm});
            skArc(sketch, "E1508", {"start": v(-273.23, 220.55) * mm, "mid": v(-275.95, 221.67) * mm, "end": v(-277.07, 224.4) * mm});
            skArc(sketch, "E1509", {"start": v(-277.07, 224.4) * mm, "mid": v(-275.95, 227.11) * mm, "end": v(-273.23, 228.24) * mm});
            skArc(sketch, "E1510", {"start": v(-273.23, 228.24) * mm, "mid": v(-270.5, 227.11) * mm, "end": v(-269.38, 224.4) * mm});
            skArc(sketch, "E1511", {"start": v(-269.38, 224.4) * mm, "mid": v(-270.5, 221.67) * mm, "end": v(-273.23, 220.55) * mm});
            skArc(sketch, "E1512", {"start": v(189.45, 241.58) * mm, "mid": v(186.73, 242.7) * mm, "end": v(185.6, 245.42) * mm});
            skArc(sketch, "E1513", {"start": v(185.6, 245.42) * mm, "mid": v(186.73, 248.14) * mm, "end": v(189.45, 249.27) * mm});
            skArc(sketch, "E1514", {"start": v(189.45, 249.27) * mm, "mid": v(192.17, 248.14) * mm, "end": v(193.3, 245.42) * mm});
            skArc(sketch, "E1515", {"start": v(193.3, 245.42) * mm, "mid": v(192.17, 242.7) * mm, "end": v(189.45, 241.58) * mm});
            skArc(sketch, "E1516", {"start": v(-267.22, 860.48) * mm, "mid": v(-269.94, 861.6) * mm, "end": v(-271.06, 864.33) * mm});
            skArc(sketch, "E1517", {"start": v(-271.06, 864.33) * mm, "mid": v(-269.94, 867.05) * mm, "end": v(-267.22, 868.17) * mm});
            skArc(sketch, "E1518", {"start": v(-267.22, 868.17) * mm, "mid": v(-264.5, 867.05) * mm, "end": v(-263.37, 864.33) * mm});
            skArc(sketch, "E1519", {"start": v(-263.37, 864.33) * mm, "mid": v(-264.5, 861.6) * mm, "end": v(-267.22, 860.48) * mm});
            skArc(sketch, "E1520", {"start": v(210.48, 851.47) * mm, "mid": v(207.76, 852.6) * mm, "end": v(206.63, 855.31) * mm});
            skArc(sketch, "E1521", {"start": v(206.63, 855.31) * mm, "mid": v(207.76, 858.03) * mm, "end": v(210.48, 859.16) * mm});
            skArc(sketch, "E1522", {"start": v(210.48, 859.16) * mm, "mid": v(213.2, 858.03) * mm, "end": v(214.32, 855.31) * mm});
            skArc(sketch, "E1523", {"start": v(214.32, 855.31) * mm, "mid": v(213.2, 852.6) * mm, "end": v(210.48, 851.47) * mm});
            skSolve(sketch);
        }
        {
            var Q0;
            {var subQ4=sQuery(id+"F0.wireOp",EDGE,"E4");Q0=makeQuery(id+"F0.imprint","IMPRINT",FACE,{"disambiguationData":[TD([[makeQuery(id+"F0.imprint","IMPRINT",EDGE,{"derivedFrom":subQ4}),1.0]])]});}
            var Q1;
            {var subQ0=sQuery(id+"F0.wireOp",EDGE,"E914");Q1=makeQuery(id+"F0.imprint","IMPRINT",FACE,{"disambiguationData":[TD([[makeQuery(id+"F0.imprint","IMPRINT",EDGE,{"derivedFrom":subQ0}),-1.0]])]});}
            var Q2;
            Q2=makeQuery(id+"F0.imprint","IMPRINT",FACE,{"disambiguationData":[TD([[makeQuery(id+"F0.imprint","IMPRINT",EDGE,{"derivedFrom":sQuery(id+"F0.wireOp",EDGE,"E657")}),-1.0]])]});
            var Q3;
            Q3=makeQuery(id+"F0.imprint","IMPRINT",FACE,{"disambiguationData":[TD([[makeQuery(id+"F0.imprint","IMPRINT",EDGE,{"derivedFrom":sQuery(id+"F0.wireOp",EDGE,"E401")}),-1.0]])]});
            extrude(context, id + "F1", {"entities" : qUnion([Q0, Q1, Q2, Q3]), "depth" : 18 * mm});
        }
    });
